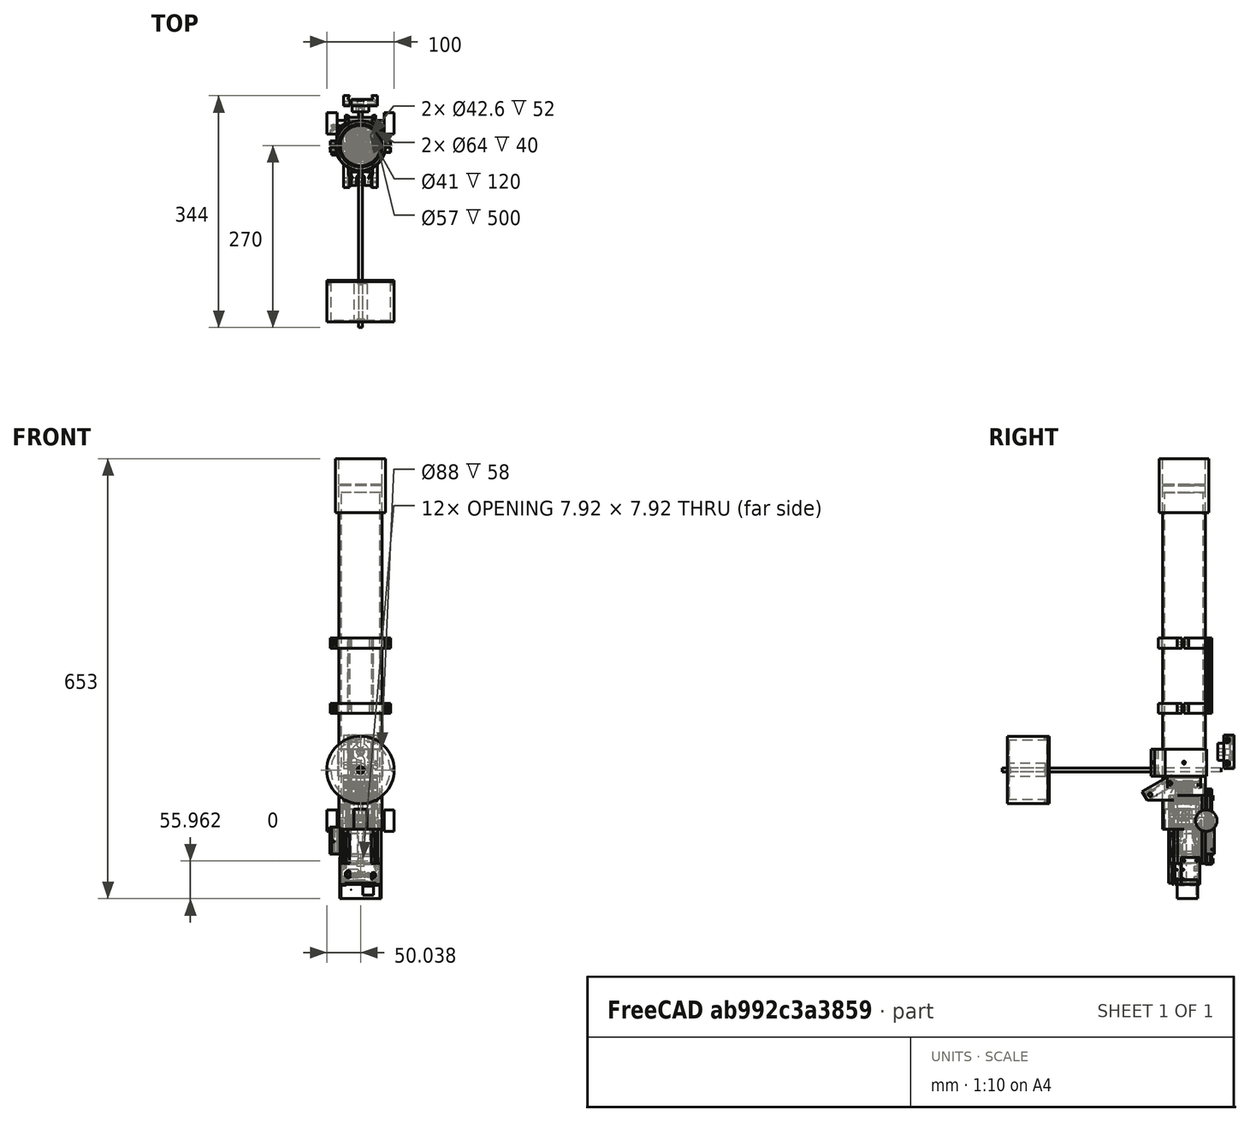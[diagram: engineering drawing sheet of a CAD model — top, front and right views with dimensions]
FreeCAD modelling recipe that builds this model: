
FCSTD DOCUMENT  (FreeCAD 0.17R13387 (Git))
Label: eq-mount-V1.5
License: All rights reserved
LicenseURL: http://en.wikipedia.org/wiki/All_rights_reserved
objects: Part::Cylinder×248, Part::MultiFuse×191, Part::Box×141, Part::Cut×137, Part::Feature×48, Part::Extrusion×34, Part::FeaturePython×21, Sketcher::SketchObject×16, Part::Part2DObjectPython×15, App::Part×13, Part::Chamfer×11, Part::Fillet×5, Part::RegularPolygon×3, Part::Wedge×1, Part::Cone×1
note: 872 computed .brp shape members not serialized (recipe doc carries the construction recipe); baked Part::Feature solids carry a one-line shape summary decoded from their .brp

FEATURE [Part::Box] Box010  label="Krychle009"
  AttacherType = Attacher::AttachEngine3D
  Height = 10
  Length = 43
  Placement = pos=(-21.5,-20.5,0) rot=(0,0,1;0rad)
  Width = 42
FEATURE [Part::Chamfer] Chamfer001
  Base = -> Box010
  Edges = 2 edges r=5: [Edge1,Edge5]
FEATURE [Part::Cylinder] Cylinder014005154  label="Válec151"
  Angle = 360
  AttacherType = Attacher::AttachEngine3D
  Height = 50
  Placement = pos=(-9.9,9.9,0) rot=(0,0,1;0rad)
  Radius = 1.6
FEATURE [Part::Cylinder] Cylinder014005155  label="Válec152"
  Angle = 360
  AttacherType = Attacher::AttachEngine3D
  Height = 50
  Placement = pos=(9.9,9.9,0) rot=(0,0,1;0rad)
  Radius = 1.6
FEATURE [Part::Cylinder] Cylinder014005156  label="dira stred001"
  Angle = 360
  AttacherType = Attacher::AttachEngine3D
  Height = 50
  Radius = 11
FEATURE [Part::Cylinder] Cylinder014005157  label="Válec153"
  Angle = 360
  AttacherType = Attacher::AttachEngine3D
  Height = 50
  Placement = pos=(-9.9,-9.9,0) rot=(0,0,1;0rad)
  Radius = 1.6
FEATURE [Part::Cylinder] Cylinder014005158  label="Válec154"
  Angle = 360
  AttacherType = Attacher::AttachEngine3D
  Height = 50
  Placement = pos=(9.9,-9.9,0) rot=(0,0,1;0rad)
  Radius = 1.6
FEATURE [Part::MultiFuse] Fusion092  label="diry001"
  Shapes = -> [Cylinder014005154,Cylinder014005155,Cylinder014005156,Cylinder014005157,Cylinder014005158]
FEATURE [Part::Cut] Cut061007  label="Horni ucjyt"
  Base = -> Chamfer001
  Placement = pos=(0,0,40.5) rot=(0,0,1;0rad)
  Tool = -> Fusion092
FEATURE [Part::Box] Box  label="deska"
  AttacherType = Attacher::AttachEngine3D
  Height = 102
  Length = 43
  Placement = pos=(-21.5,21.5,-51.5) rot=(0,0,1;0rad)
  Width = 10
FEATURE [Part::Box] Box012  label="deska001"
  AttacherType = Attacher::AttachEngine3D
  Height = 102
  Length = 9
  Placement = pos=(-30.5,-14.5,-51.5) rot=(0,0,1;0rad)
  Width = 46
FEATURE [Part::Box] Box013  label="deska002"
  AttacherType = Attacher::AttachEngine3D
  Height = 102
  Length = 9
  Placement = pos=(21.5,-14.5,-51.5) rot=(0,0,1;0rad)
  Width = 46
FEATURE [Part::Box] Box014  label="Krychle"
  AttacherType = Attacher::AttachEngine3D
  Height = 112
  Length = 38
  Placement = pos=(-19,32,-52) rot=(0,0,1;0rad)
  Width = 10
FEATURE [Part::Box] Box015  label="Krychle011"
  AttacherType = Attacher::AttachEngine3D
  Height = 112
  Length = 38
  Placement = pos=(-19,34,-52) rot=(0,0,1;0rad)
  Width = 6
FEATURE [Part::Cut] Cut061009
  Base = -> Box014
  Tool = -> Box015
FEATURE [Sketcher::SketchObject] Sketch
  MapMode = 5
  Placement = pos=(0,0,60) rot=(0,0,1;0rad)
  sketch-geometry (6):
    g0: LineSegment StartX=-18.9734 StartY=34.0308 StartZ=0 EndX=-16.0253 EndY=36.9748 EndZ=0
    g1: LineSegment StartX=18.996 StartY=34.0308 StartZ=0 EndX=16.044 EndY=36.9748 EndZ=0
    g2: LineSegment StartX=18.996 StartY=34.0308 StartZ=0 EndX=-18.9734 EndY=34.0308 EndZ=0
    g3: LineSegment StartX=-18.9734 StartY=40.0311 StartZ=0 EndX=-16.0253 EndY=36.9748 EndZ=0
    g4: LineSegment StartX=16.044 StartY=36.9748 StartZ=0 EndX=18.9109 EndY=40.0311 EndZ=0
    g5: LineSegment StartX=-18.9734 StartY=40.0311 StartZ=0 EndX=18.9109 EndY=40.0311 EndZ=0
  constraints (7):
    c: Coincident(g2,g1)
    c: Coincident(g2,g0)
    c: Horizontal(g2)
    c: Coincident(g3,g0)
    c: Coincident(g5,g3)
    c: Coincident(g5,g4)
    c: Horizontal(g5)
FEATURE [Part::Extrusion] Extrude009
  Base = -> Sketch
  Dir = (0,0,1)
  DirMode = 2
  FaceMakerClass = Part::FaceMakerBullseye
  LengthFwd = -112
  LengthRev = 0
  Solid = true
  Symmetric = false
FEATURE [Part::MultiFuse] Fusion095  label="Arca plate base"
  Placement = pos=(0,-0.5,0) rot=(0,0,1;0rad)
  Shapes = -> [Extrude009,Cut061009]
FEATURE [Part::Box] Box016  label="Krychle012"
  AttacherType = Attacher::AttachEngine3D
  Height = 112
  Length = 38
  Placement = pos=(-19,32,-52) rot=(0,0,1;0rad)
  Width = 10
FEATURE [Part::Box] Box017  label="Krychle013"
  AttacherType = Attacher::AttachEngine3D
  Height = 112
  Length = 38
  Placement = pos=(-19,34,-52) rot=(0,0,1;0rad)
  Width = 6
FEATURE [Part::Cut] Cut061010
  Base = -> Box016
  Tool = -> Box017
FEATURE [Sketcher::SketchObject] Sketch002
  MapMode = 5
  Placement = pos=(0,0,60) rot=(0,0,1;0rad)
  sketch-geometry (6):
    g0: LineSegment StartX=-18.9734 StartY=34.0308 StartZ=0 EndX=-16.0253 EndY=36.9748 EndZ=0
    g1: LineSegment StartX=18.996 StartY=34.0308 StartZ=0 EndX=16.044 EndY=36.9748 EndZ=0
    g2: LineSegment StartX=18.996 StartY=34.0308 StartZ=0 EndX=-18.9734 EndY=34.0308 EndZ=0
    g3: LineSegment StartX=-18.9734 StartY=40.0311 StartZ=0 EndX=-16.0253 EndY=36.9748 EndZ=0
    g4: LineSegment StartX=16.044 StartY=36.9748 StartZ=0 EndX=18.9109 EndY=40.0311 EndZ=0
    g5: LineSegment StartX=-18.9734 StartY=40.0311 StartZ=0 EndX=18.9109 EndY=40.0311 EndZ=0
  constraints (7):
    c: Coincident(g2,g1)
    c: Coincident(g2,g0)
    c: Horizontal(g2)
    c: Coincident(g3,g0)
    c: Coincident(g5,g3)
    c: Coincident(g5,g4)
    c: Horizontal(g5)
FEATURE [Part::Extrusion] Extrude010
  Base = -> Sketch002
  Dir = (0,0,1)
  DirMode = 2
  FaceMakerClass = Part::FaceMakerBullseye
  LengthFwd = -112
  LengthRev = 0
  Solid = true
  Symmetric = false
FEATURE [Part::MultiFuse] Fusion096  label="Arca plate base001"
  Placement = pos=(0,-0.6,0) rot=(0,0,1;0rad)
  Shapes = -> [Extrude010,Cut061010]
FEATURE [Part::Cylinder] Cylinder014005164  label="Válec159"
  Angle = 360
  AttacherType = Attacher::AttachEngine3D
  Height = 200
  Placement = pos=(0,27,-100) rot=(0,0,1;0rad)
  Radius = 3.2
FEATURE [Part::FeaturePython] Nut  label="M6-Nut"  # Fasteners workbench fastener (typed FeaturePython)
  Placement = pos=(0,27,46) rot=(0,0,1;0rad)
  diameter = 8
  invert = false
  matchOuter = false
  offset = 0
  thread = false
  type = 1
FEATURE [Part::FeaturePython] Nut001  label="M6-Nut001"  # Fasteners workbench fastener (typed FeaturePython)
  Placement = pos=(0,27,-52) rot=(0,0,1;0rad)
  diameter = 8
  invert = false
  matchOuter = false
  offset = 0
  thread = false
  type = 1
FEATURE [Part::MultiFuse] Fusion097  label="Dira zavazi"
  Shapes = -> [Cylinder014005164,Nut,Nut001]
FEATURE [Part::Cylinder] Cylinder014005165  label="Válec160"
  Angle = 360
  AttacherType = Attacher::AttachEngine3D
  Height = 10
  Placement = pos=(0,43,46.5) rot=(1,0,0;1.5708rad)
  Radius = 4
FEATURE [Part::Cylinder] Cylinder014005166  label="Válec161"
  Angle = 360
  AttacherType = Attacher::AttachEngine3D
  Height = 10
  Placement = pos=(0,43,-47) rot=(1,0,0;1.5708rad)
  Radius = 4
FEATURE [Part::RegularPolygon] RegularPolygon004  label="Pravidelný n-úhelník004"
  AttacherType = Attacher::AttachEngine3D
  Circumradius = 6
  Polygon = 6
FEATURE [Part::Extrusion] Extrude027
  Base = -> RegularPolygon004
  Dir = (0,0,1)
  DirMode = 2
  FaceMakerClass = Part::FaceMakerBullseye
  LengthFwd = 8
  LengthRev = 0
  Placement = pos=(0,0,13) rot=(0,0,1;0rad)
  Solid = true
  Symmetric = false
FEATURE [Part::FeaturePython] Nut007  label="M4-Nut002"  # Fasteners workbench fastener (typed FeaturePython)
  Placement = pos=(22,17,69) rot=(0,1,0;1.5708rad)
  diameter = 6
  invert = false
  matchOuter = false
  offset = 0
  thread = false
  type = 1
FEATURE [Part::FeaturePython] Nut008  label="M4-Nut003"  # Fasteners workbench fastener (typed FeaturePython)
  Placement = pos=(22,-17,69) rot=(0,1,0;1.5708rad)
  diameter = 6
  invert = false
  matchOuter = false
  offset = 0
  thread = false
  type = 1
FEATURE [Sketcher::SketchObject] Sketch009
  MapMode = 5
  Placement = pos=(0,0,60) rot=(0,0,1;0rad)
  sketch-geometry (6):
    g0: LineSegment StartX=-18.9734 StartY=34.0308 StartZ=0 EndX=-16.0253 EndY=36.9748 EndZ=0
    g1: LineSegment StartX=18.996 StartY=34.0308 StartZ=0 EndX=16.044 EndY=36.9748 EndZ=0
    g2: LineSegment StartX=18.996 StartY=34.0308 StartZ=0 EndX=-18.9734 EndY=34.0308 EndZ=0
    g3: LineSegment StartX=-18.9734 StartY=40.0311 StartZ=0 EndX=-16.0253 EndY=36.9748 EndZ=0
    g4: LineSegment StartX=16.044 StartY=36.9748 StartZ=0 EndX=18.9109 EndY=40.0311 EndZ=0
    g5: LineSegment StartX=-18.9734 StartY=40.0311 StartZ=0 EndX=18.9109 EndY=40.0311 EndZ=0
  constraints (7):
    c: Coincident(g2,g1)
    c: Coincident(g2,g0)
    c: Horizontal(g2)
    c: Coincident(g3,g0)
    c: Coincident(g5,g3)
    c: Coincident(g5,g4)
    c: Horizontal(g5)
FEATURE [Part::Extrusion] Extrude025
  Base = -> Sketch009
  Dir = (0,0,1)
  DirMode = 2
  FaceMakerClass = Part::FaceMakerBullseye
  LengthFwd = -112
  LengthRev = 0
  Solid = true
  Symmetric = false
FEATURE [Sketcher::SketchObject] Sketch010
  MapMode = 45
  Placement = pos=(44.88,21.011,5.40003) rot=(0.707106,0.001666,0.707106;3.13826rad)
  sketch-geometry (7):
    g0: LineSegment StartX=5.21891 StartY=0.0364138 StartZ=0 EndX=2.62121 EndY=4.46293 EndZ=0
    g1: LineSegment StartX=2.62121 StartY=4.46293 StartZ=0 EndX=-2.51111 EndY=4.42651 EndZ=0
    g2: LineSegment StartX=-2.51111 StartY=4.42651 StartZ=0 EndX=-5.04574 EndY=-0.0364138 EndZ=0
    g3: LineSegment StartX=-5.04574 StartY=-0.0364138 StartZ=0 EndX=-2.44804 EndY=-4.46293 EndZ=0
    g4: LineSegment StartX=-2.44804 StartY=-4.46293 StartZ=0 EndX=2.68428 EndY=-4.42651 EndZ=0
    g5: LineSegment StartX=2.68428 StartY=-4.42651 StartZ=0 EndX=5.21891 EndY=0.0364138 EndZ=0
    g6: Circle [constr] CenterX=0.0865834 CenterY=0 CenterZ=0 NormalX=0 NormalY=0 NormalZ=1 AngleXU=0 Radius=5.13245
  constraints (14):
    c: Coincident(g0,g1)
    c: Coincident(g1,g2)
    c: Coincident(g2,g3)
    c: Coincident(g3,g4)
    c: Coincident(g4,g5)
    c: Coincident(g5,g0)
    c: Equal(g0, g1-g5) x5
    c: PointOnObject(g0,g6)
    c: PointOnObject(g1,g6)
    c: PointOnObject(g2,g6)
    c: PointOnObject(g3,g6)
    c: PointOnObject(g4,g6)
    c: PointOnObject(g5,g6)
    c: PointOnObject(g6,g-1)
FEATURE [Part::Extrusion] Extrude026
  Base = -> Sketch010
  Dir = (1,0,0)
  DirMode = 2
  FaceMakerClass = Part::FaceMakerBullseye
  LengthFwd = 5
  LengthRev = 0
  Placement = pos=(0,0,0.25) rot=(0,0,1;0rad)
  Solid = true
  Symmetric = false
FEATURE [Part::Feature] Screw_solid087  label="M2x4-Screw (Solid)087"
  Placement = pos=(0,0,0) rot=(0,0,1;3.14159rad)
  shape: bbox 3.6 x 3.6 x 4 mm, 12 faces (baked)
FEATURE [Part::Feature] Cylinder014005326  label="Válec302"
  Placement = pos=(0,0,0) rot=(0,0,1;2.0944rad)
  shape: bbox 5 x 5 x 7 mm, 3 faces (baked)
FEATURE [Part::Feature] Cylinder014005327  label="Válec303"
  Placement = pos=(0,0,0) rot=(0,0,1;4.18879rad)
  shape: bbox 5 x 5 x 7 mm, 3 faces (baked)
FEATURE [Part::Feature] Screw_solid088  label="M2x4-Screw (Solid)088"
  Placement = pos=(0,0,0) rot=(0,0,1;1.0472rad)
  shape: bbox 3.6 x 3.6 x 4 mm, 12 faces (baked)
FEATURE [Part::Feature] Cylinder014005328  label="Válec304"
  shape: bbox 5 x 5 x 7 mm, 3 faces (baked)
FEATURE [Part::MultiFuse] Fusion196
  Shapes = -> [Cylinder014005327,Cylinder014005328,Cylinder014005326]
FEATURE [Part::Feature] Screw_solid089  label="M2x4-Screw (Solid)089"
  Placement = pos=(0,0,0) rot=(0,0,-1;1.0472rad)
  shape: bbox 3.6 x 3.6 x 4 mm, 12 faces (baked)
FEATURE [Part::MultiFuse] Fusion199  label="srouby030"
  Placement = pos=(0,0,0.5) rot=(0,0,1;0rad)
  Shapes = -> [Screw_solid088,Screw_solid089,Screw_solid087]
FEATURE [Part::Box] Box035  label="Krychle028"
  AttacherType = Attacher::AttachEngine3D
  Height = 112
  Length = 38
  Placement = pos=(-19,32,-52) rot=(0,0,1;0rad)
  Width = 10
FEATURE [Part::Box] Box036  label="Krychle029"
  AttacherType = Attacher::AttachEngine3D
  Height = 112
  Length = 38
  Placement = pos=(-19,34,-52) rot=(0,0,1;0rad)
  Width = 6
FEATURE [Part::Cylinder] Cylinder014005329  label="Válec305"
  Angle = 360
  AttacherType = Attacher::AttachEngine3D
  Height = 22
  Radius = 2.6
FEATURE [Part::MultiFuse] Fusion195
  Shapes = -> [Cylinder014005329,Extrude026]
FEATURE [Part::Cylinder] Cylinder014005330  label="Válec306"
  Angle = 360
  AttacherType = Attacher::AttachEngine3D
  Height = 7
  Radius = 2.6
FEATURE [Part::MultiFuse] Fusion198
  Placement = pos=(0,0,1) rot=(0,0,1;0rad)
  Shapes = -> [Fusion196,Cylinder014005330]
FEATURE [Part::Cylinder] Cylinder014005331  label="Válec307"
  Angle = 360
  AttacherType = Attacher::AttachEngine3D
  Height = 8
  Placement = pos=(0,0,66) rot=(0,0,1;0rad)
  Radius = 4.5
FEATURE [Part::Box] Box037  label="Krychle030"
  AttacherType = Attacher::AttachEngine3D
  Height = 15
  Length = 50
  Placement = pos=(-25,-25,64) rot=(0,0,1;0rad)
  Width = 50
FEATURE [Part::Cylinder] Cylinder014005332  label="Válec308"
  Angle = 360
  AttacherType = Attacher::AttachEngine3D
  Height = 6
  Placement = pos=(0,0,7) rot=(0,0,1;0rad)
  Radius = 6.5
FEATURE [Part::Box] Box038  label="Krychle031"
  AttacherType = Attacher::AttachEngine3D
  Height = 15
  Length = 2
  Placement = pos=(-15.5,-26,61) rot=(0,0,1;0rad)
  Width = 52
FEATURE [Part::Cylinder] Cylinder014005333  label="Unasec vrch017"
  Angle = 360
  AttacherType = Attacher::AttachEngine3D
  Height = 1.5
  Placement = pos=(0,0,5.5) rot=(0,0,1;0rad)
  Radius = 15.5
FEATURE [Part::Cylinder] Cylinder014005334  label="Válec309"
  Angle = 360
  AttacherType = Attacher::AttachEngine3D
  Height = 55
  Placement = pos=(0,0,35) rot=(0,0,1;0rad)
  Radius = 2.7
FEATURE [Part::Cylinder] Cylinder014005335  label="Válec310"
  Angle = 360
  AttacherType = Attacher::AttachEngine3D
  Height = 9
  Placement = pos=(0,0,55) rot=(0,0,1;0rad)
  Radius = 12.5
FEATURE [Part::Cut] Cut061079  label="unasec vrch017"
  Base = -> Cylinder014005333
  Tool = -> Fusion199
FEATURE [Part::Cut] Cut061080
  Base = -> Box035
  Tool = -> Box036
FEATURE [Part::MultiFuse] Fusion194  label="Arca plate base004"
  Placement = pos=(0,-6.5,115.5) rot=(-1,0,0;1.5708rad)
  Shapes = -> [Extrude025,Cut061080]
FEATURE [Part::Cut] Cut061077  label="Arca sw 002"
  Base = -> Box037
  Tool = -> Fusion194
FEATURE [Part::Cut] Cut061083
  Base = -> Cut061077
  Tool = -> Box038
FEATURE [Part::MultiFuse] Fusion192
  Shapes = -> [Cylinder014005335,Cut061083]
FEATURE [Part::Cut] Cut061084  label="Unasec Vrch zaklad017"
  Base = -> Cut061079
  Tool = -> Fusion198
FEATURE [Part::MultiFuse] Fusion197
  Shapes = -> [Cut061084,Cylinder014005332,Extrude027]
FEATURE [Part::Cut] Cut061081  label="unasec top004"
  Base = -> Fusion197
  Placement = pos=(0,0,42) rot=(0,0,1;0rad)
  Tool = -> Fusion195
FEATURE [Part::MultiFuse] Fusion191
  Shapes = -> [Cylinder014005334,Cut061081,Cylinder014005331]
FEATURE [Part::Cut] Cut061082
  Base = -> Fusion192
  Tool = -> Fusion191
FEATURE [Part::Cylinder] Cylinder014005336  label="Válec311"
  Angle = 360
  AttacherType = Attacher::AttachEngine3D
  Height = 60
  Placement = pos=(-30,17,69) rot=(0,1,0;1.5708rad)
  Radius = 2.1
FEATURE [Part::Cylinder] Cylinder014005337  label="Válec312"
  Angle = 360
  AttacherType = Attacher::AttachEngine3D
  Height = 60
  Placement = pos=(-30,-17,69) rot=(0,1,0;1.5708rad)
  Radius = 2.1
FEATURE [Part::MultiFuse] Fusion193
  Shapes = -> [Cylinder014005336,Cylinder014005337,Nut007,Nut008]
FEATURE [Part::Cut] Cut061078
  Base = -> Cut061082
  Tool = -> Fusion193
FEATURE [Part::Cylinder] Cylinder014005338  label="Válec313"
  Angle = 360
  AttacherType = Attacher::AttachEngine3D
  Height = 2.5
  Placement = pos=(0,-12,71) rot=(0,0,1;0rad)
  Radius = 6
FEATURE [Part::Box] Box039  label="Krychle032"
  AttacherType = Attacher::AttachEngine3D
  Height = 2.5
  Length = 12
  Placement = pos=(-6,-25,71) rot=(0,0,1;0rad)
  Width = 13
FEATURE [Part::MultiFuse] Fusion201
  Placement = pos=(0,0,1) rot=(0,0,1;3.14159rad)
  Shapes = -> [Box039,Cylinder014005338]
FEATURE [Part::Cylinder] Cylinder014005339  label="Válec314"
  Angle = 360
  AttacherType = Attacher::AttachEngine3D
  Height = 2.5
  Placement = pos=(0,-12,71) rot=(0,0,1;0rad)
  Radius = 6
FEATURE [Part::Box] Box040  label="Krychle033"
  AttacherType = Attacher::AttachEngine3D
  Height = 2.5
  Length = 12
  Placement = pos=(-6,-25,71) rot=(0,0,1;0rad)
  Width = 13
FEATURE [Part::MultiFuse] Fusion200
  Placement = pos=(0,0,1) rot=(0,0,1;0rad)
  Shapes = -> [Box040,Cylinder014005339]
FEATURE [Part::MultiFuse] Fusion202
  Shapes = -> [Fusion200,Fusion201]
FEATURE [Part::Cut] Cut061085  label="Swis Arca002"
  Base = -> Cut061078
  Placement = pos=(0,-5,115) rot=(-1,0,0;1.5708rad)
  Tool = -> Fusion202
FEATURE [Part::Box] Box041  label="Krychle034"
  AttacherType = Attacher::AttachEngine3D
  Height = 13
  Length = 80
  Placement = pos=(-40,-34,50.5) rot=(0,0,1;0rad)
  Width = 80
FEATURE [Part::Box] Box042  label="Krychle035"
  AttacherType = Attacher::AttachEngine3D
  Height = 2
  Length = 80
  Placement = pos=(-40,-36,-53) rot=(0,0,1;0rad)
  Width = 80
FEATURE [Part::MultiFuse] Fusion203  label="Oreze"
  Shapes = -> [Box041,Box042]
FEATURE [Part::Feature] Cut001001  label="polar finder"
  Placement = pos=(-9.5,-26.5,-25) rot=(0,0,-1;1.5708rad)
  shape: bbox 15 x 36 x 40 mm, 20 faces (baked)
FEATURE [Part::Cylinder] Cylinder014005345  label="M6 Rail"
  Angle = 360
  AttacherType = Attacher::AttachEngine3D
  Height = 325
  Placement = pos=(0,55,88) rot=(1,0,0;1.5708rad)
  Radius = 3
FEATURE [Part::Cylinder] Cylinder014005346  label="Válec317"
  Angle = 360
  AttacherType = Attacher::AttachEngine3D
  Height = 60
  Placement = pos=(0,-200,88) rot=(1,0,0;1.5708rad)
  Radius = 50
FEATURE [Part::Cylinder] Cylinder014005347  label="Válec318"
  Angle = 360
  AttacherType = Attacher::AttachEngine3D
  Height = 58
  Placement = pos=(0,-200,88) rot=(1,0,0;1.5708rad)
  Radius = 44
FEATURE [Part::Cut] Cut061093
  Base = -> Cylinder014005346
  Tool = -> Cylinder014005347
FEATURE [Part::Cylinder] Cylinder014005348  label="Válec319"
  Angle = 360
  AttacherType = Attacher::AttachEngine3D
  Height = 56
  Placement = pos=(0,-203.5,88) rot=(1,0,0;1.5708rad)
  Radius = 10
FEATURE [Part::MultiFuse] Fusion217  label="Zavazí dno"
  Placement = pos=(0,-2,0) rot=(0,0,1;0rad)
  Shapes = -> [Cut061093,Cylinder014005348]
FEATURE [Part::Cylinder] Cylinder014005349  label="Válec320"
  Angle = 360
  AttacherType = Attacher::AttachEngine3D
  Height = 2
  Placement = pos=(0,-200,88) rot=(1,0,0;1.5708rad)
  Radius = 50
FEATURE [Part::Cylinder] Cylinder014005350  label="Válec321"
  Angle = 360
  AttacherType = Attacher::AttachEngine3D
  Height = 3.5
  Placement = pos=(0,-200,88) rot=(1,0,0;1.5708rad)
  Radius = 44
FEATURE [Part::MultiFuse] Fusion218  label="zaazi vyko"
  Shapes = -> [Cylinder014005350,Cylinder014005349]
FEATURE [Part::Cylinder] Cylinder014005351  label="tyč závaží001"
  Angle = 360
  AttacherType = Attacher::AttachEngine3D
  Height = 350
  Placement = pos=(0,85,88) rot=(1,0,0;1.5708rad)
  Radius = 3
FEATURE [Part::FeaturePython] Nut013  label="M6-Nut006"  # Fasteners workbench fastener (typed FeaturePython)
  Placement = pos=(0,-258,88) rot=(1,0,0;1.5708rad)
  diameter = 8
  invert = false
  matchOuter = false
  offset = 0
  thread = false
  type = 1
FEATURE [Part::Feature] Screw006_solid  label="vyko M2.5x8"
  Placement = pos=(0,0,10) rot=(0,0,1;0rad)
  shape: bbox 4.5 x 8.524 x 4.5 mm, 11 faces (baked)
FEATURE [Part::Feature] Screw006_solid001  label="vyko M2.5x009"
  Placement = pos=(0,0,104) rot=(0,0,1;0rad)
  shape: bbox 4.5 x 8.524 x 4.5 mm, 11 faces (baked)
FEATURE [Part::Feature] Screw006_solid002  label="vyko M2.5x010"
  Placement = pos=(47,0,57) rot=(0,0,1;0rad)
  shape: bbox 4.5 x 8.524 x 4.5 mm, 11 faces (baked)
FEATURE [Part::Feature] Screw006_solid003  label="vyko M2.5x011"
  Placement = pos=(-47,0,57) rot=(0,0,1;0rad)
  shape: bbox 4.5 x 8.524 x 4.5 mm, 11 faces (baked)
FEATURE [Part::MultiFuse] Fusion219  label="srouby diry zavazi"
  Shapes = -> [Cylinder014005351,Screw006_solid,Screw006_solid001,Screw006_solid002,Screw006_solid003,Nut013]
FEATURE [Part::Cut] Cut061094  label="Weight  bottom"
  Base = -> Fusion217
  Tool = -> Fusion219
FEATURE [Part::FeaturePython] Nut014  label="M6-Nut005"  # Fasteners workbench fastener (typed FeaturePython)
  Placement = pos=(0,-238,88) rot=(1,0,0;1.5708rad)
  diameter = 8
  invert = false
  matchOuter = false
  offset = 0
  thread = false
  type = 1
FEATURE [Part::Cylinder] Cylinder014005352  label="tyč závaží002"
  Angle = 360
  AttacherType = Attacher::AttachEngine3D
  Height = 300
  Placement = pos=(0,55,88) rot=(1,0,0;1.5708rad)
  Radius = 3
FEATURE [Part::Feature] Screw006_solid004  label="vyko M2.5x012"
  Placement = pos=(0,0,104) rot=(0,0,1;0rad)
  shape: bbox 4.5 x 8.524 x 4.5 mm, 11 faces (baked)
FEATURE [Part::Feature] Screw006_solid005  label="vyko M2.5x013"
  Placement = pos=(47,0,57) rot=(0,0,1;0rad)
  shape: bbox 4.5 x 8.524 x 4.5 mm, 11 faces (baked)
FEATURE [Part::Feature] Screw006_solid006  label="vyko M2.5x014"
  Placement = pos=(-47,0,57) rot=(0,0,1;0rad)
  shape: bbox 4.5 x 8.524 x 4.5 mm, 11 faces (baked)
FEATURE [Part::Feature] Screw006_solid007  label="vyko M2.5x015"
  Placement = pos=(0,0,10) rot=(0,0,1;0rad)
  shape: bbox 4.5 x 8.524 x 4.5 mm, 11 faces (baked)
FEATURE [Part::MultiFuse] Fusion220  label="srouby diry zavazi001"
  Shapes = -> [Cylinder014005352,Screw006_solid007,Screw006_solid004,Screw006_solid005,Screw006_solid006,Nut014]
FEATURE [Part::Cut] Cut061095  label="Weight top"
  Base = -> Fusion218
  Tool = -> Fusion220
FEATURE [App::Part] Part019  label="Temp"
  Group = -> [Cut061009,Sketch,Box014,Box015,Extrude009,Fusion095,Sketch009,Fusion193,Fusion192,Fusion191,Fusion194,Fusion196,Fusion195,Fusion197,Fusion198,Nut007,Nut008,Extrude025,RegularPolygon004,Extrude026,Extrude027,Cut061078,Cut061080,Cut061082,Cut061083,Cut061081,Cut061084,Cut061079,Cut061077,Screw_solid088,Screw_solid087,Cylinder014005326,Cylinder014005328,Screw_solid089,Cylinder014005327,Sketch010,+22 more]
  License = CC BY 3.0
  LicenseURL = http://creativecommons.org/licenses/by/3.0/
  Origin = -> Origin019
FEATURE [Part::Feature] Cut061098  label="Motor PG100"
  Placement = pos=(0,0,2) rot=(0,0,1;0rad)
  shape: bbox 42.3 x 42.3 x 110 mm, 26 faces (baked)
FEATURE [Part::Cylinder] Cylinder014005356  label="Válec322"
  Angle = 360
  AttacherType = Attacher::AttachEngine3D
  Height = 3
  Placement = pos=(-9.9,9.9,47) rot=(0,0,1;0rad)
  Radius = 2.8
FEATURE [Part::Cylinder] Cylinder014005357  label="Válec323"
  Angle = 360
  AttacherType = Attacher::AttachEngine3D
  Height = 3
  Placement = pos=(9.9,9.9,47) rot=(0,0,1;0rad)
  Radius = 2.8
FEATURE [Part::Cylinder] Cylinder014005358  label="Válec324"
  Angle = 360
  AttacherType = Attacher::AttachEngine3D
  Height = 3
  Placement = pos=(-9.9,-9.9,47) rot=(0,0,1;0rad)
  Radius = 2.8
FEATURE [Part::Cylinder] Cylinder014005359  label="Válec325"
  Angle = 360
  AttacherType = Attacher::AttachEngine3D
  Height = 3
  Placement = pos=(9.9,-9.9,47) rot=(0,0,1;0rad)
  Radius = 2.8
FEATURE [Part::MultiFuse] Fusion221  label="Imbus diry"
  Shapes = -> [Cylinder014005356,Cylinder014005357,Cylinder014005358,Cylinder014005359]
FEATURE [Part::MultiFuse] Fusion222
  Shapes = -> [Cut061007,Cylinder014005165,Cylinder014005166,Box013,Box,Box012,Fusion096]
FEATURE [Part::MultiFuse] Fusion223
  Shapes = -> [Fusion221,Fusion203,Fusion097]
FEATURE [Part::Cut] Cut061099
  Base = -> Fusion222
  Tool = -> Fusion223
FEATURE [Part::Chamfer] Chamfer008  label="Zaklad"
  Base = -> Cut061099
  Edges = 4 edges r=5: [Edge130,Edge132,Edge145,Edge147]
FEATURE [App::Part] Part022  label="Zaklad002"
  Group = -> [Nut,Nut001,Fusion097,Fusion092,Fusion096,Cut061007,Cut061010,Chamfer001,Cylinder014005156,Box010,Cylinder014005157,Cylinder014005154,Cylinder014005158,Cylinder014005155,Box017,Box,Box016,Box012,Box013,Sketch002,Extrude010,Cylinder014005166,Cylinder014005164,Cylinder014005165,Fusion203,Box042,Box041,Cylinder014005359,Cylinder014005358,Cylinder014005356,Cylinder014005357,Cut061099,Fusion221,+4 more]
  License = CC BY 3.0
  LicenseURL = http://creativecommons.org/licenses/by/3.0/
  Origin = -> Origin022
FEATURE [Part::Box] Box008  label="Krychle043"
  AttacherType = Attacher::AttachEngine3D
  Height = 28
  Length = 62
  Placement = pos=(-2.5,-2,-5) rot=(0,0,1;0rad)
  Width = 31
FEATURE [Part::Box] Box054  label="Krychle003"
  AttacherType = Attacher::AttachEngine3D
  Height = 26
  Length = 58
  Placement = pos=(-0.5,0,-3) rot=(0,0,1;0rad)
  Width = 29
FEATURE [Part::Cylinder] Cylinder014005360  label="Válec326"
  Angle = 360
  AttacherType = Attacher::AttachEngine3D
  Height = 8
  Placement = pos=(53.5,21.25,0) rot=(0,0,1;0rad)
  Radius = 0.75
FEATURE [Part::Cylinder] Cylinder014005361  label="Válec010"
  Angle = 360
  AttacherType = Attacher::AttachEngine3D
  Height = 8
  Placement = pos=(53.5,6,0) rot=(0,0,1;0rad)
  Radius = 0.75
FEATURE [Part::Cylinder] Cylinder012  label="Válec327"
  Angle = 360
  AttacherType = Attacher::AttachEngine3D
  Height = 8
  Placement = pos=(3.5,21.25,0) rot=(0,0,1;0rad)
  Radius = 0.75
FEATURE [Part::Cylinder] Cylinder014005362  label="Válec012"
  Angle = 360
  AttacherType = Attacher::AttachEngine3D
  Height = 8
  Placement = pos=(3.5,6,0) rot=(0,0,1;0rad)
  Radius = 0.7
FEATURE [Part::Part2DObjectPython] ShapeString001  # Draft 2D object (typed FeaturePython)
  FontFile = <path>
  Placement = pos=(15.3452,-2,30.5072) rot=(1,0,0;1.5708rad)
  Size = 4
  String = RA
  Tracking = 0
FEATURE [Part::Extrusion] Extrude031  label="Text RA"
  Base = -> ShapeString001
  Dir = (0,-1,0)
  DirMode = 2
  FaceMakerClass = Part::FaceMakerBullseye
  LengthFwd = 1
  LengthRev = 0
  Placement = pos=(21,0.5,-33) rot=(0,0,1;0rad)
  Solid = false
  Symmetric = false
FEATURE [Part::Part2DObjectPython] ShapeString  # Draft 2D object (typed FeaturePython)
  FontFile = <path>
  Placement = pos=(15.3452,-2,30.5072) rot=(1,0,0;1.5708rad)
  Size = 4
  String = ON
  Tracking = 0
FEATURE [Part::Extrusion] Extrude030  label="Text TR"
  Base = -> ShapeString
  Dir = (0,-1,0)
  DirMode = 2
  FaceMakerClass = Part::FaceMakerBullseye
  LengthFwd = 1
  LengthRev = 0
  Placement = pos=(-6.75,0.5,-33) rot=(0,0,1;0rad)
  Solid = false
  Symmetric = false
FEATURE [Part::Cut] Cut061101  label="Základ"
  Base = -> Box008
  Tool = -> Box054
FEATURE [Part::Cylinder] Cylinder017  label="Válec016"
  Angle = 360
  AttacherType = Attacher::AttachEngine3D
  Height = 6.5
  Placement = pos=(3.5,6,0) rot=(0,0,1;0rad)
  Radius = 3.5
FEATURE [Part::Cylinder] Cylinder014  label="Válec333"
  Angle = 360
  AttacherType = Attacher::AttachEngine3D
  Height = 6.5
  Placement = pos=(53.5,6,0) rot=(0,0,1;0rad)
  Radius = 3.5
FEATURE [Part::Cylinder] Cylinder016  label="Válec015"
  Angle = 360
  AttacherType = Attacher::AttachEngine3D
  Height = 6.5
  Placement = pos=(3.5,21.25,0) rot=(0,0,1;0rad)
  Radius = 3.5
FEATURE [Part::Cylinder] Cylinder015  label="Válec334"
  Angle = 360
  AttacherType = Attacher::AttachEngine3D
  Height = 6.5
  Placement = pos=(53.5,21.25,0) rot=(0,0,1;0rad)
  Radius = 3.5
FEATURE [Part::Cylinder] Cylinder021  label="Válec020"
  Angle = 360
  AttacherType = Attacher::AttachEngine3D
  Height = 70
  Placement = pos=(-5,20,16.5) rot=(0,1,0;1.5708rad)
  Radius = 1
FEATURE [Part::Cylinder] Cylinder020  label="Válec019"
  Angle = 360
  AttacherType = Attacher::AttachEngine3D
  Height = 70
  Placement = pos=(-5,6,16.5) rot=(0,1,0;1.5708rad)
  Radius = 1
FEATURE [Part::Box] Box055  label="RJ051"
  AttacherType = Attacher::AttachEngine3D
  Height = 13
  Length = 16
  Placement = pos=(32,-5,4.5) rot=(0,0,1;0rad)
  Width = 18.5
FEATURE [Part::Cylinder] Cylinder038  label="Válec337"
  Angle = 360
  AttacherType = Attacher::AttachEngine3D
  Height = 5
  Placement = pos=(14.25,1,9.5) rot=(1,0,0;1.5708rad)
  Radius = 1.5
FEATURE [Part::MultiFuse] Fusion226  label="Horni diry"
  Placement = pos=(0,0,3) rot=(0,0,1;0rad)
  Shapes = -> [Cylinder021,Cylinder020]
FEATURE [Part::MultiFuse] Fusion228  label="RJ a LED"
  Shapes = -> [Box055,Cylinder038]
FEATURE [Part::MultiFuse] Fusion230  label="diry008"
  Placement = pos=(0,0,-4) rot=(0,0,1;0rad)
  Shapes = -> [Cylinder012,Cylinder014005362,Cylinder014005360,Cylinder014005361]
FEATURE [Part::MultiFuse] Fusion007  label="sloupky"
  Placement = pos=(0,0,-3.5) rot=(0,0,1;0rad)
  Shapes = -> [Cylinder016,Cylinder017,Cylinder015,Cylinder014]
FEATURE [Part::MultiFuse] Fusion243  label="bez der"
  Shapes = -> [Cut061101,Fusion007]
FEATURE [Part::MultiFuse] Fusion244
  Shapes = -> [Fusion230,Fusion228,Fusion226]
FEATURE [Part::Cut] Cut061109
  Base = -> Fusion243
  Tool = -> Fusion244
FEATURE [Part::MultiFuse] Fusion245
  Shapes = -> [Extrude030,Extrude031]
FEATURE [Part::Cut] Cut061110
  Base = -> Cut061109
  Placement = pos=(-28.5,18.5,-80) rot=(1,0,0;1.5708rad)
  Tool = -> Fusion245
FEATURE [Part::Feature] Cut061098001  label="RA Motor PG100"
  shape: bbox 42.3 x 42.3 x 110 mm, 26 faces (baked)
FEATURE [Part::Box] Box068  label="Krychle054"
  AttacherType = Attacher::AttachEngine3D
  Height = 13
  Length = 2
  Placement = pos=(29,-4.5,-55) rot=(0,0,1;0rad)
  Width = 28
FEATURE [Part::Box] Box069  label="Krychle055"
  AttacherType = Attacher::AttachEngine3D
  Height = 13
  Length = 2
  Placement = pos=(-31,-4.5,-55) rot=(0,0,1;0rad)
  Width = 28
FEATURE [Part::MultiFuse] Fusion250
  Shapes = -> [Box068,Box069]
FEATURE [Part::MultiFuse] Fusion252  label="RA pcb box"
  Shapes = -> [Cut061110,Fusion250]
FEATURE [Part::Cylinder] Cylinder014005370  label="Válec352"
  Angle = 360
  AttacherType = Attacher::AttachEngine3D
  Height = 74
  Placement = pos=(-40,0,-46.5) rot=(0,1,0;1.5708rad)
  Radius = 1.4
FEATURE [Part::Cylinder] Cylinder014005371  label="Válec353"
  Angle = 360
  AttacherType = Attacher::AttachEngine3D
  Height = 74
  Placement = pos=(-40,19,-46.5) rot=(0,1,0;1.5708rad)
  Radius = 1.4
FEATURE [Part::MultiFuse] Fusion253
  Shapes = -> [Cylinder014005370,Cylinder014005371]
FEATURE [Part::Cylinder] Cylinder014005376  label="Válec358"
  Angle = 360
  AttacherType = Attacher::AttachEngine3D
  Height = 20
  Placement = pos=(-40,16,-17.5) rot=(0,1,0;1.5708rad)
  Radius = 1.4
FEATURE [Part::Cylinder] Cylinder014005377  label="Válec359"
  Angle = 360
  AttacherType = Attacher::AttachEngine3D
  Height = 20
  Placement = pos=(-40,1,-17.5) rot=(0,1,0;1.5708rad)
  Radius = 1.4
FEATURE [Part::Cut] Cut061098005  label="RA PCB Box"
  Base = -> Fusion252
  Tool = -> Fusion253
FEATURE [Part::Box] Box077  label="Krychle062"
  AttacherType = Attacher::AttachEngine3D
  Height = 13
  Length = 2
  Placement = pos=(29,-4.5,-55) rot=(0,0,1;0rad)
  Width = 28
FEATURE [Part::Cylinder] Cylinder014005393  label="Válec375"
  Angle = 360
  AttacherType = Attacher::AttachEngine3D
  Height = 74
  Placement = pos=(-40,19,-46.5) rot=(0,1,0;1.5708rad)
  Radius = 1.4
FEATURE [Part::Cylinder] Cylinder014005394  label="Válec376"
  Angle = 360
  AttacherType = Attacher::AttachEngine3D
  Height = 74
  Placement = pos=(-40,0,-46.5) rot=(0,1,0;1.5708rad)
  Radius = 1.4
FEATURE [Part::Box] Box078  label="Krychle063"
  AttacherType = Attacher::AttachEngine3D
  Height = 13
  Length = 2
  Placement = pos=(-31,-4.5,-55) rot=(0,0,1;0rad)
  Width = 28
FEATURE [Part::MultiFuse] Fusion266
  Shapes = -> [Box077,Box078]
FEATURE [Part::Part2DObjectPython] ShapeString008  # Draft 2D object (typed FeaturePython)
  FontFile = <path>
  Placement = pos=(15.3452,-2,30.5072) rot=(1,0,0;1.5708rad)
  Size = 4
  String = Focuser
  Tracking = 0
FEATURE [Part::Part2DObjectPython] ShapeString009  # Draft 2D object (typed FeaturePython)
  FontFile = <path>
  Placement = pos=(15.3452,-2,30.5072) rot=(1,0,0;1.5708rad)
  Size = 4
  String = DEC
  Tracking = 0
FEATURE [Part::Box] Box079  label="RJ053"
  AttacherType = Attacher::AttachEngine3D
  Height = 13
  Length = 16
  Placement = pos=(34,-4,4.5) rot=(0,0,1;0rad)
  Width = 18.5
FEATURE [Part::Cylinder] Cylinder014005398  label="Válec380"
  Angle = 360
  AttacherType = Attacher::AttachEngine3D
  Height = 8
  Placement = pos=(3.6,21.25,0) rot=(0,0,1;0rad)
  Radius = 0.75
FEATURE [Part::Cylinder] Cylinder014005399  label="Válec381"
  Angle = 360
  AttacherType = Attacher::AttachEngine3D
  Height = 6.5
  Placement = pos=(53.5,21.25,0) rot=(0,0,1;0rad)
  Radius = 3.5
FEATURE [Part::Cylinder] Cylinder014005400  label="Válec382"
  Angle = 360
  AttacherType = Attacher::AttachEngine3D
  Height = 70
  Placement = pos=(-5,6,16.5) rot=(0,1,0;1.5708rad)
  Radius = 1
FEATURE [Part::Cylinder] Cylinder014005401  label="Válec383"
  Angle = 360
  AttacherType = Attacher::AttachEngine3D
  Height = 6.5
  Placement = pos=(3.5,6,0) rot=(0,0,1;0rad)
  Radius = 3.5
FEATURE [Part::Cylinder] Cylinder014005402  label="Válec384"
  Angle = 360
  AttacherType = Attacher::AttachEngine3D
  Height = 70
  Placement = pos=(-5,20,16.5) rot=(0,1,0;1.5708rad)
  Radius = 1
FEATURE [Part::Cylinder] Cylinder014005403  label="Válec385"
  Angle = 360
  AttacherType = Attacher::AttachEngine3D
  Height = 8
  Placement = pos=(53.5,6,0) rot=(0,0,1;0rad)
  Radius = 0.75
FEATURE [Part::Box] Box082  label="Krychle066"
  AttacherType = Attacher::AttachEngine3D
  Height = 26
  Length = 58
  Placement = pos=(-0.5,0,-3) rot=(0,0,1;0rad)
  Width = 29
FEATURE [Part::Cylinder] Cylinder014005404  label="Válec386"
  Angle = 360
  AttacherType = Attacher::AttachEngine3D
  Height = 6.5
  Placement = pos=(53.5,6,0) rot=(0,0,1;0rad)
  Radius = 3.5
FEATURE [Part::Cylinder] Cylinder014005405  label="Válec387"
  Angle = 360
  AttacherType = Attacher::AttachEngine3D
  Height = 8
  Placement = pos=(53.5,21.25,0) rot=(0,0,1;0rad)
  Radius = 0.75
FEATURE [Part::Cylinder] Cylinder014005406  label="Válec388"
  Angle = 360
  AttacherType = Attacher::AttachEngine3D
  Height = 8
  Placement = pos=(3.5,6,0) rot=(0,0,1;0rad)
  Radius = 0.7
FEATURE [Part::Box] Box083  label="RJ054"
  AttacherType = Attacher::AttachEngine3D
  Height = 14.5
  Length = 13
  Placement = pos=(7.5,-4,4.5) rot=(0,0,1;0rad)
  Width = 13
FEATURE [Part::Cylinder] Cylinder014005407  label="Válec389"
  Angle = 360
  AttacherType = Attacher::AttachEngine3D
  Height = 6.5
  Placement = pos=(3.5,21.25,0) rot=(0,0,1;0rad)
  Radius = 3.5
FEATURE [Part::Box] Box084  label="Krychle067"
  AttacherType = Attacher::AttachEngine3D
  Height = 28
  Length = 62
  Placement = pos=(-2.5,-2,-5) rot=(0,0,1;0rad)
  Width = 31
FEATURE [Part::Cut] Cut061098016
  Base = -> Box084
  Tool = -> Box082
FEATURE [Part::MultiFuse] Fusion272
  Shapes = -> [Box079,Box083]
FEATURE [Part::MultiFuse] Fusion274  label="diry010"
  Placement = pos=(0,0,-4) rot=(0,0,1;0rad)
  Shapes = -> [Cylinder014005398,Cylinder014005406,Cylinder014005405,Cylinder014005403]
FEATURE [Part::MultiFuse] Fusion278  label="Horni diry005"
  Placement = pos=(0,0,3) rot=(0,0,1;0rad)
  Shapes = -> [Cylinder014005402,Cylinder014005400]
FEATURE [Part::MultiFuse] Fusion280  label="sloupky003"
  Placement = pos=(0,0,-3.5) rot=(0,0,1;0rad)
  Shapes = -> [Cylinder014005407,Cylinder014005401,Cylinder014005399,Cylinder014005404]
FEATURE [Part::Extrusion] Extrude037  label="Text DEC002"
  Base = -> ShapeString009
  Dir = (0,-1,0)
  DirMode = 2
  FaceMakerClass = Part::FaceMakerBullseye
  LengthFwd = 1
  LengthRev = 0
  Placement = pos=(21,0.5,-35) rot=(0,0,1;0rad)
  Solid = false
  Symmetric = false
FEATURE [Part::Extrusion] Extrude038  label="Text Focuser002"
  Base = -> ShapeString008
  Dir = (0,-1,0)
  DirMode = 2
  FaceMakerClass = Part::FaceMakerBullseye
  LengthFwd = 1
  LengthRev = 0
  Placement = pos=(-11,0.5,-35) rot=(0,0,1;0rad)
  Solid = false
  Symmetric = false
FEATURE [Part::MultiFuse] Fusion275  label="Texty002"
  Placement = pos=(0,0.5,2.5) rot=(0,0,1;0rad)
  Shapes = -> [Extrude038,Extrude037]
FEATURE [Part::Cut] Cut061098018  label="RJ dirama002"
  Base = -> Cut061098016
  Tool = -> Fusion272
FEATURE [Part::MultiFuse] Fusion277
  Shapes = -> [Cut061098018,Fusion280]
FEATURE [Part::Cut] Cut061098015  label="Ze sloupky002"
  Base = -> Fusion277
  Tool = -> Fusion274
FEATURE [Part::MultiFuse] Fusion281
  Shapes = -> [Fusion275,Fusion278]
FEATURE [Part::Cut] Cut061098019  label="Dec zaklad"
  Base = -> Cut061098015
  Placement = pos=(-28.5,18.5,-80) rot=(1,0,0;1.5708rad)
  Tool = -> Fusion281
FEATURE [Part::MultiFuse] Fusion282
  Shapes = -> [Fusion266,Cut061098019]
FEATURE [Part::MultiFuse] Fusion283
  Shapes = -> [Cylinder014005394,Cylinder014005393]
FEATURE [Part::Cut] Cut061098020  label="DEC PCB Box"
  Base = -> Fusion282
  Tool = -> Fusion283
FEATURE [Part::Feature] Cut061098023  label="DEC Motor PG100"
  shape: bbox 42.3 x 42.3 x 110 mm, 26 faces (baked)
FEATURE [App::Part] Part026  label="Weigth"
  Group = -> [Cylinder014005345,Screw006_solid002,Screw006_solid003,Screw006_solid001,Screw006_solid,Cylinder014005351,Cylinder014005347,Cylinder014005348,Cylinder014005346,Fusion217,Fusion219,Cut061093,Nut013,Cut061094,Screw006_solid004,Screw006_solid005,Screw006_solid006,Cylinder014005350,Cylinder014005349,Cylinder014005352,Fusion218,Fusion220,Screw006_solid007,Nut014,Cut061095]
  License = CC BY 3.0
  LicenseURL = http://creativecommons.org/licenses/by/3.0/
  Origin = -> Origin026
  Placement = pos=(0,0,-3) rot=(0,0,1;0rad)
FEATURE [Sketcher::SketchObject] Sketch021
  MapMode = 5
  Placement = pos=(0,40,0) rot=(0,0.707107,0.707107;3.14159rad)
  sketch-geometry (6):
    g0: LineSegment StartX=0 StartY=0 StartZ=0 EndX=0 EndY=3 EndZ=0
    g1: LineSegment StartX=0 StartY=3 StartZ=0 EndX=-4 EndY=10 EndZ=0
    g2: LineSegment StartX=-4 StartY=10 StartZ=0 EndX=-26 EndY=10 EndZ=0
    g3: LineSegment StartX=-26 StartY=10 StartZ=0 EndX=-30 EndY=3 EndZ=0
    g4: LineSegment StartX=-30 StartY=3 StartZ=0 EndX=-30 EndY=0 EndZ=0
    g5: LineSegment StartX=-30 StartY=0 StartZ=0 EndX=0 EndY=0 EndZ=0
  constraints (11):
    c: Coincident(g-1,g0)
    c: PointOnObject(g0,g-2)
    c: Coincident(g0,g1)
    c: Coincident(g1,g2)
    c: Horizontal(g2)
    c: Coincident(g2,g3)
    c: Coincident(g3,g4)
    c: PointOnObject(g4,g-1)
    c: Vertical(g4)
    c: Coincident(g4,g5)
    c: Coincident(g5,g0)
FEATURE [Sketcher::SketchObject] Sketch022
  MapMode = 5
  Placement = pos=(0,0,60) rot=(0,0,1;0rad)
  sketch-geometry (6):
    g0: LineSegment StartX=-18.9734 StartY=34.0308 StartZ=0 EndX=-16.0253 EndY=36.9748 EndZ=0
    g1: LineSegment StartX=18.996 StartY=34.0308 StartZ=0 EndX=16.044 EndY=36.9748 EndZ=0
    g2: LineSegment StartX=18.996 StartY=34.0308 StartZ=0 EndX=-18.9734 EndY=34.0308 EndZ=0
    g3: LineSegment StartX=-18.9734 StartY=40.0311 StartZ=0 EndX=-16.0253 EndY=36.9748 EndZ=0
    g4: LineSegment StartX=16.044 StartY=36.9748 StartZ=0 EndX=18.9109 EndY=40.0311 EndZ=0
    g5: LineSegment StartX=-18.9734 StartY=40.0311 StartZ=0 EndX=18.9109 EndY=40.0311 EndZ=0
  constraints (7):
    c: Coincident(g2,g1)
    c: Coincident(g2,g0)
    c: Horizontal(g2)
    c: Coincident(g3,g0)
    c: Coincident(g5,g3)
    c: Coincident(g5,g4)
    c: Horizontal(g5)
FEATURE [Part::FeaturePython] Screw016  label="M2.5x8-Screw001"  # Fasteners workbench fastener (typed FeaturePython)
  Placement = pos=(-34,0,20) rot=(0,-1,0;1.5708rad)
  diameter = 3
  invert = false
  length = 3
  matchOuter = false
  offset = 0
  thread = false
  type = 12
FEATURE [Part::FeaturePython] Screw017  label="M2.5x8-Screw002"  # Fasteners workbench fastener (typed FeaturePython)
  Placement = pos=(34,0,20) rot=(0,1,0;1.5708rad)
  diameter = 3
  invert = false
  length = 3
  matchOuter = false
  offset = 0
  thread = false
  type = 12
FEATURE [Part::FeaturePython] Screw012  label="M4x20-Screw004"  # Fasteners workbench fastener (typed FeaturePython)
  Placement = pos=(-40.5,-9,53) rot=(1,0,0;1.5708rad)
  diameter = 4
  invert = false
  length = 5
  matchOuter = false
  offset = 0
  thread = false
  type = 5
FEATURE [Part::FeaturePython] Nut021  label="M4-Nut010"  # Fasteners workbench fastener (typed FeaturePython)
  Placement = pos=(-40.2,7,53) rot=(1,0,0;1.5708rad)
  diameter = 6
  invert = false
  matchOuter = false
  offset = 0
  thread = false
  type = 1
FEATURE [Part::FeaturePython] Screw013  label="M4x20-Screw005"  # Fasteners workbench fastener (typed FeaturePython)
  Placement = pos=(-40.5,-9,53) rot=(1,0,0;1.5708rad)
  diameter = 4
  invert = false
  length = 5
  matchOuter = false
  offset = 0
  thread = false
  type = 5
FEATURE [Part::FeaturePython] Screw015  label="M4x20-Screw007"  # Fasteners workbench fastener (typed FeaturePython)
  Placement = pos=(-40.5,-9,53) rot=(1,0,0;1.5708rad)
  diameter = 4
  invert = false
  length = 5
  matchOuter = false
  offset = 0
  thread = false
  type = 5
FEATURE [Part::FeaturePython] Nut022  label="M4-Nut011"  # Fasteners workbench fastener (typed FeaturePython)
  Placement = pos=(-40.2,7,53) rot=(1,0,0;1.5708rad)
  diameter = 6
  invert = false
  matchOuter = false
  offset = 0
  thread = false
  type = 1
FEATURE [Part::FeaturePython] Nut023  label="M4-Nut012"  # Fasteners workbench fastener (typed FeaturePython)
  Placement = pos=(-40.2,7,53) rot=(1,0,0;1.5708rad)
  diameter = 6
  invert = false
  matchOuter = false
  offset = 0
  thread = false
  type = 1
FEATURE [Part::FeaturePython] Nut024  label="M4-Nut013"  # Fasteners workbench fastener (typed FeaturePython)
  Placement = pos=(-40.2,7,53) rot=(1,0,0;1.5708rad)
  diameter = 6
  invert = false
  matchOuter = false
  offset = 0
  thread = false
  type = 1
FEATURE [Part::FeaturePython] Screw014  label="M4x20-Screw006"  # Fasteners workbench fastener (typed FeaturePython)
  Placement = pos=(-40.5,-9,53) rot=(1,0,0;1.5708rad)
  diameter = 4
  invert = false
  length = 5
  matchOuter = false
  offset = 0
  thread = false
  type = 5
FEATURE [Part::Extrusion] Extrude047
  Base = -> Sketch022
  Dir = (0,0,1)
  DirMode = 2
  FaceMakerClass = Part::FaceMakerBullseye
  LengthFwd = -112
  LengthRev = 0
  Solid = true
  Symmetric = false
FEATURE [Part::Extrusion] Extrude003
  Base = -> Sketch021
  Dir = (0,1,0)
  DirMode = 2
  FaceMakerClass = Part::FaceMakerBullseye
  LengthFwd = -40
  LengthRev = 0
  Placement = pos=(-15,0,0) rot=(0,0,1;0rad)
  Solid = true
  Symmetric = false
FEATURE [Part::MultiFuse] Fusion331  label="Srouby004"
  Placement = pos=(80.5,0,-97.5) rot=(0,0,1;0rad)
  Shapes = -> [Screw015,Nut024]
FEATURE [Part::MultiFuse] Fusion336  label="Srouby005"
  Placement = pos=(0,0,-0.5) rot=(0,0,1;0rad)
  Shapes = -> [Screw013,Nut022]
FEATURE [Part::MultiFuse] Fusion001030  label="Srouby006"
  Placement = pos=(80.5,0,-0.5) rot=(0,0,1;0rad)
  Shapes = -> [Screw012,Nut023]
FEATURE [Part::MultiFuse] Fusion100  label="Srouby007"
  Placement = pos=(0,0,-97.5) rot=(0,0,1;0rad)
  Shapes = -> [Screw014,Nut021]
FEATURE [Part::MultiFuse] Fusion332
  Shapes = -> [Fusion336,Fusion001030,Fusion100,Fusion331]
FEATURE [Part::MultiFuse] Fusion009
  Shapes = -> [Screw017,Screw016]
FEATURE [Part::Cylinder] Cylinder014005551  label="Válec481"
  Angle = 360
  AttacherType = Attacher::AttachEngine3D
  Height = 500
  Radius = 28.5
FEATURE [Part::Cylinder] Cylinder014005555  label="Válec484"
  Angle = 360
  AttacherType = Attacher::AttachEngine3D
  Height = 100
  Placement = pos=(-50,33,13) rot=(0,1,0;1.5708rad)
  Radius = 4
FEATURE [Part::Cylinder] Cylinder014005552  label="Válec482"
  Angle = 360
  AttacherType = Attacher::AttachEngine3D
  Height = 500
  Radius = 32
FEATURE [Part::Cut] Cut061176  label="tubus !"
  Base = -> Cylinder014005552
  Tool = -> Cylinder014005551
FEATURE [Part::Cylinder] Cylinder014005563  label="Válec489"
  Angle = 360
  AttacherType = Attacher::AttachEngine3D
  Height = 15
  Placement = pos=(35,33,13) rot=(0,1,0;1.5708rad)
  Radius = 16
FEATURE [Part::Cylinder] Cylinder014005558  label="Lens"
  Angle = 360
  AttacherType = Attacher::AttachEngine3D
  Height = 10
  Placement = pos=(0,0,500) rot=(0,0,1;0rad)
  Radius = 32
FEATURE [Part::Cylinder] Cylinder014005554  label="Válec490"
  Angle = 360
  AttacherType = Attacher::AttachEngine3D
  Height = 40
  Placement = pos=(0,0,0) rot=(0,0,1;3.83972rad)
  Radius = 33.5
FEATURE [Part::Cylinder] Cylinder014005556  label="Válec485"
  Angle = 360
  AttacherType = Attacher::AttachEngine3D
  Height = 15
  Placement = pos=(-50,33,13) rot=(0,1,0;1.5708rad)
  Radius = 16
FEATURE [Part::Box] Box099  label="Krychle082"
  AttacherType = Attacher::AttachEngine3D
  Height = 30
  Length = 24
  Placement = pos=(-12,25,0) rot=(0,0,1;0rad)
  Width = 12
FEATURE [Part::Cylinder] Cylinder014005565  label="Lens001"
  Angle = 360
  AttacherType = Attacher::AttachEngine3D
  Height = 2
  Placement = pos=(0,0,510) rot=(0,0,1;0rad)
  Radius = 32
FEATURE [Part::Box] Box074  label="Krychle061"
  AttacherType = Attacher::AttachEngine3D
  Height = 3
  Length = 13
  Placement = pos=(-6.5,0,-3) rot=(0,0,1;0rad)
  Width = 4
FEATURE [Part::MultiFuse] Fusion001029  label="Dovecot profile002"
  Shapes = -> [Extrude003,Box074]
FEATURE [Part::Cylinder] Cylinder014005564  label="Válec491"
  Angle = 360
  AttacherType = Attacher::AttachEngine3D
  Height = 120
  Placement = pos=(0,0,-80) rot=(0,0,1;0rad)
  Radius = 20.5
FEATURE [Part::Cylinder] Cylinder014005560  label="Válec487"
  Angle = 360
  AttacherType = Attacher::AttachEngine3D
  Height = 120
  Placement = pos=(0,0,-80) rot=(0,0,1;0rad)
  Radius = 23
FEATURE [Part::Cut] Cut061023
  Base = -> Cylinder014005560
  Tool = -> Cylinder014005564
FEATURE [Part::Cylinder] Cylinder014005561  label="Válec488"
  Angle = 360
  AttacherType = Attacher::AttachEngine3D
  Height = 30
  Radius = 23
FEATURE [Part::Cylinder] Cylinder014005559  label="Válec486"
  Angle = 360
  AttacherType = Attacher::AttachEngine3D
  Height = 30
  Radius = 28
FEATURE [Part::Box] Box100  label="Krychle064"
  AttacherType = Attacher::AttachEngine3D
  Height = 40
  Length = 36
  Placement = pos=(-18,-36,0) rot=(0,0,1;0rad)
  Width = 10
FEATURE [Part::Box] Box101  label="Krychle060"
  AttacherType = Attacher::AttachEngine3D
  Height = 15
  Length = 36
  Placement = pos=(-18,0,-5) rot=(0,0,1;0rad)
  Width = 40
FEATURE [Part::Cut] Cut061175
  Base = -> Box101
  Tool = -> Fusion001029
FEATURE [Part::Chamfer] Chamfer012
  Base = -> Cut061175
  Edges = 2 edges r=5: [Edge2,Edge29]
FEATURE [Part::Box] Box075  label="Krychle083"
  AttacherType = Attacher::AttachEngine3D
  Height = 30
  Length = 24
  Placement = pos=(-12,25,0) rot=(0,0,1;0rad)
  Width = 12
FEATURE [Part::Box] Box076  label="Krychle084"
  AttacherType = Attacher::AttachEngine3D
  Height = 30
  Length = 20
  Placement = pos=(-10,-32,0) rot=(0,0,1;0rad)
  Width = 5
FEATURE [Part::MultiFuse] Fusion121
  Shapes = -> [Box076,Box075]
FEATURE [Part::Cut] Cut061173  label="Tubus"
  Base = -> Cut061176
  Tool = -> Fusion121
FEATURE [Part::Cylinder] Cylinder014005553  label="Válec483"
  Angle = 360
  AttacherType = Attacher::AttachEngine3D
  Height = 40
  Placement = pos=(0,0,0) rot=(0,0,1;0.872665rad)
  Radius = 32
FEATURE [Part::Cylinder] Cylinder014005557  label="LensH001"
  Angle = 360
  AttacherType = Attacher::AttachEngine3D
  Height = 80
  Placement = pos=(0,0,500) rot=(0,0,1;0rad)
  Radius = 32
FEATURE [Part::Box] Box102  label="Krychle065"
  AttacherType = Attacher::AttachEngine3D
  Height = 30
  Length = 20
  Placement = pos=(-10,-32,0) rot=(0,0,1;0rad)
  Width = 5
FEATURE [Part::MultiFuse] Fusion122
  Shapes = -> [Box099,Box102,Cylinder014005559]
FEATURE [Part::Cut] Cut061177
  Base = -> Fusion122
  Tool = -> Cylinder014005561
FEATURE [Part::MultiFuse] Fusion123  label="Focuser"
  Shapes = -> [Cut061023,Cut061177,Cylinder014005555,Cylinder014005556,Cylinder014005563]
FEATURE [Part::Cylinder] Cylinder014005562  label="LensH"
  Angle = 360
  AttacherType = Attacher::AttachEngine3D
  Height = 80
  Placement = pos=(0,0,500) rot=(0,0,1;0rad)
  Radius = 37
FEATURE [Part::Cut] Cut061024
  Base = -> Cylinder014005562
  Placement = pos=(0,0,-30) rot=(0,0,1;0rad)
  Tool = -> Cylinder014005557
FEATURE [Part::Cylinder] Cylinder014005566  label="Lens002"
  Angle = 360
  AttacherType = Attacher::AttachEngine3D
  Height = 2
  Placement = pos=(0,0,510) rot=(0,0,1;0rad)
  Radius = 30
FEATURE [Part::Cut] Cut061025
  Base = -> Cylinder014005565
  Tool = -> Cylinder014005566
FEATURE [Part::MultiFuse] Fusion124
  Shapes = -> [Cut061025,Cut061024]
FEATURE [Part::Box] Box103  label="mezara002"
  AttacherType = Attacher::AttachEngine3D
  Height = 15
  Length = 90
  Placement = pos=(-45,-3,45) rot=(0,0,1;0rad)
  Width = 3
FEATURE [Part::Box] Box104  label="Krychle085"
  AttacherType = Attacher::AttachEngine3D
  Height = 15
  Length = 90
  Placement = pos=(-45,-10,45) rot=(0,0,1;0rad)
  Width = 17
FEATURE [Part::Cylinder] Cylinder014005546  label="tubus003"
  Angle = 360
  AttacherType = Attacher::AttachEngine3D
  Height = 112
  Placement = pos=(0,-1,-52) rot=(0,0,1;0rad)
  Radius = 32
FEATURE [Part::Cylinder] Cylinder014005547  label="tubus004"
  Angle = 360
  AttacherType = Attacher::AttachEngine3D
  Height = 15
  Placement = pos=(0,-1,-52) rot=(0,0,1;0rad)
  Radius = 37
FEATURE [Part::Box] Box105  label="Krychle086"
  AttacherType = Attacher::AttachEngine3D
  Height = 112
  Length = 38
  Placement = pos=(-19,32,-52) rot=(0,0,1;0rad)
  Width = 10
FEATURE [Part::Cylinder] Cylinder014005548  label="tubus005"
  Angle = 360
  AttacherType = Attacher::AttachEngine3D
  Height = 15
  Placement = pos=(0,-1,45) rot=(0,0,1;0rad)
  Radius = 37
FEATURE [Part::Box] Box106  label="Krychle087"
  AttacherType = Attacher::AttachEngine3D
  Height = 112
  Length = 38
  Placement = pos=(-19,34,-52) rot=(0,0,1;0rad)
  Width = 6
FEATURE [Part::Cut] Cut061179
  Base = -> Box105
  Tool = -> Box106
FEATURE [Part::MultiFuse] Fusion335  label="Arca plate base008"
  Placement = pos=(0,-0.5,0) rot=(0,0,1;0rad)
  Shapes = -> [Extrude047,Cut061179]
FEATURE [Part::Box] Box107  label="mezara003"
  AttacherType = Attacher::AttachEngine3D
  Height = 15
  Length = 90
  Placement = pos=(-45,-3,-52) rot=(0,0,1;0rad)
  Width = 3
FEATURE [Part::MultiFuse] Fusion001028
  Shapes = -> [Box103,Box107,Cylinder014005546]
FEATURE [Part::Cylinder] Cylinder014005550  label="Válec480"
  Angle = 360
  AttacherType = Attacher::AttachEngine3D
  Height = 10
  Placement = pos=(12,20,4) rot=(0,1,0;0.785398rad)
  Radius = 1.4
FEATURE [Part::Box] Box108  label="Krychle088"
  AttacherType = Attacher::AttachEngine3D
  Height = 15
  Length = 90
  Placement = pos=(-45,-10,-52) rot=(0,0,1;0rad)
  Width = 17
FEATURE [Part::MultiFuse] Fusion337
  Shapes = -> [Fusion335,Cylinder014005547,Cylinder014005548,Box104,Box108]
FEATURE [Part::Cut] Cut061178
  Base = -> Fusion337
  Tool = -> Fusion001028
FEATURE [Part::Cut] Cut061172  label="Swiss Arca holder"
  Base = -> Cut061178
  Placement = pos=(0,0,224) rot=(0,0,1;0rad)
  Tool = -> Fusion332
FEATURE [Part::Cylinder] Cylinder014005549  label="Válec479"
  Angle = 360
  AttacherType = Attacher::AttachEngine3D
  Height = 10
  Placement = pos=(-12,20,4) rot=(0,-1,0;0.785398rad)
  Radius = 1.4
FEATURE [Part::MultiFuse] Fusion334
  Shapes = -> [Cylinder014005550,Cylinder014005549]
FEATURE [Part::Cut] Cut005  label="Dov holder003"
  Base = -> Chamfer012
  Placement = pos=(0,-39,0) rot=(1,0,0;1.5708rad)
  Tool = -> Fusion334
FEATURE [Part::MultiFuse] Fusion333
  Shapes = -> [Cylinder014005554,Cut005,Box100]
FEATURE [Part::Cut] Cut061174
  Base = -> Fusion333
  Tool = -> Cylinder014005553
FEATURE [Part::Cut] Cut007  label="Telscop dovetail holder"
  Base = -> Cut061174
  Placement = pos=(0,0,79) rot=(0,0,1;0rad)
  Tool = -> Fusion009
FEATURE [App::Part] Part040  label="DIY telescope"
  Group = -> [Cut061176,Cylinder014005551,Cylinder014005552,Box076,Box075,Fusion121,Cut061173,Cylinder014005556,Cylinder014005561,Cylinder014005564,Cylinder014005563,Cylinder014005559,Cylinder014005555,Cylinder014005560,Box099,Cut061023,Cut061177,Box102,Fusion122,Fusion123,Cylinder014005558,Cylinder014005562,Cylinder014005565,Cylinder014005557,Cut061024,Cut061025,Cylinder014005566,Fusion124,Fusion001028,+49 more]
  License = CC BY 3.0
  LicenseURL = http://creativecommons.org/licenses/by/3.0/
  Origin = -> Origin040
  Placement = pos=(0,113,-118) rot=(0,0,1;3.14159rad)
FEATURE [Sketcher::SketchObject] Sketch039
  MapMode = 5
  Placement = pos=(0,0,60) rot=(0,0,1;0rad)
  sketch-geometry (6):
    g0: LineSegment StartX=-18.9734 StartY=34.0308 StartZ=0 EndX=-16.0253 EndY=36.9748 EndZ=0
    g1: LineSegment StartX=18.996 StartY=34.0308 StartZ=0 EndX=16.044 EndY=36.9748 EndZ=0
    g2: LineSegment StartX=18.996 StartY=34.0308 StartZ=0 EndX=-18.9734 EndY=34.0308 EndZ=0
    g3: LineSegment StartX=-18.9734 StartY=40.0311 StartZ=0 EndX=-16.0253 EndY=36.9748 EndZ=0
    g4: LineSegment StartX=16.044 StartY=36.9748 StartZ=0 EndX=18.9109 EndY=40.0311 EndZ=0
    g5: LineSegment StartX=-18.9734 StartY=40.0311 StartZ=0 EndX=18.9109 EndY=40.0311 EndZ=0
  constraints (7):
    c: Coincident(g2,g1)
    c: Coincident(g2,g0)
    c: Horizontal(g2)
    c: Coincident(g3,g0)
    c: Coincident(g5,g3)
    c: Coincident(g5,g4)
    c: Horizontal(g5)
FEATURE [Sketcher::SketchObject] Sketch040
  MapMode = 5
  Placement = pos=(0,0,60) rot=(0,0,1;0rad)
  sketch-geometry (6):
    g0: LineSegment StartX=-18.9734 StartY=34.0308 StartZ=0 EndX=-16.0253 EndY=36.9748 EndZ=0
    g1: LineSegment StartX=18.996 StartY=34.0308 StartZ=0 EndX=16.044 EndY=36.9748 EndZ=0
    g2: LineSegment StartX=18.996 StartY=34.0308 StartZ=0 EndX=-18.9734 EndY=34.0308 EndZ=0
    g3: LineSegment StartX=-18.9734 StartY=40.0311 StartZ=0 EndX=-16.0253 EndY=36.9748 EndZ=0
    g4: LineSegment StartX=16.044 StartY=36.9748 StartZ=0 EndX=18.9109 EndY=40.0311 EndZ=0
    g5: LineSegment StartX=-18.9734 StartY=40.0311 StartZ=0 EndX=18.9109 EndY=40.0311 EndZ=0
  constraints (7):
    c: Coincident(g2,g1)
    c: Coincident(g2,g0)
    c: Horizontal(g2)
    c: Coincident(g3,g0)
    c: Coincident(g5,g3)
    c: Coincident(g5,g4)
    c: Horizontal(g5)
FEATURE [Sketcher::SketchObject] Sketch041
  MapMode = 5
  Placement = pos=(0,0,60) rot=(0,0,1;0rad)
  sketch-geometry (6):
    g0: LineSegment StartX=-18.9734 StartY=34.0308 StartZ=0 EndX=-16.0253 EndY=36.9748 EndZ=0
    g1: LineSegment StartX=18.996 StartY=34.0308 StartZ=0 EndX=16.044 EndY=36.9748 EndZ=0
    g2: LineSegment StartX=18.996 StartY=34.0308 StartZ=0 EndX=-18.9734 EndY=34.0308 EndZ=0
    g3: LineSegment StartX=-18.9734 StartY=40.0311 StartZ=0 EndX=-16.0253 EndY=36.9748 EndZ=0
    g4: LineSegment StartX=16.044 StartY=36.9748 StartZ=0 EndX=18.9109 EndY=40.0311 EndZ=0
    g5: LineSegment StartX=-18.9734 StartY=40.0311 StartZ=0 EndX=18.9109 EndY=40.0311 EndZ=0
  constraints (7):
    c: Coincident(g2,g1)
    c: Coincident(g2,g0)
    c: Horizontal(g2)
    c: Coincident(g3,g0)
    c: Coincident(g5,g3)
    c: Coincident(g5,g4)
    c: Horizontal(g5)
FEATURE [Part::Box] Box109  label="Krychle091"
  AttacherType = Attacher::AttachEngine3D
  Height = 15
  Length = 50
  Placement = pos=(-25,-25,64) rot=(0,0,1;0rad)
  Width = 50
FEATURE [Part::Box] Box110  label="Krychle092"
  AttacherType = Attacher::AttachEngine3D
  Height = 20
  Length = 60
  Placement = pos=(-14,-30,62) rot=(0,0,1;0rad)
  Width = 60
FEATURE [Part::Box] Box111  label="Krychle096"
  AttacherType = Attacher::AttachEngine3D
  Height = 2.5
  Length = 12
  Placement = pos=(-6,-25,71) rot=(0,0,1;0rad)
  Width = 13
FEATURE [Part::Box] Box112  label="Krychle093"
  AttacherType = Attacher::AttachEngine3D
  Height = 15
  Length = 50
  Placement = pos=(-25,-25,64) rot=(0,0,1;0rad)
  Width = 50
FEATURE [Part::Cylinder] Cylinder014005644  label="Válec564"
  Angle = 360
  AttacherType = Attacher::AttachEngine3D
  Height = 60
  Placement = pos=(-30,17,69) rot=(0,1,0;1.5708rad)
  Radius = 2.7
FEATURE [Part::Box] Box113  label="Krychle099"
  AttacherType = Attacher::AttachEngine3D
  Height = 8
  Length = 50
  Placement = pos=(-25,0,3) rot=(0,0,1;0rad)
  Width = 82
FEATURE [Part::Cylinder] Cylinder014005353  label="Válec559"
  Angle = 360
  AttacherType = Attacher::AttachEngine3D
  Height = 60
  Placement = pos=(-30,17,69) rot=(0,1,0;1.5708rad)
  Radius = 2.7
FEATURE [Part::Box] Box114  label="Krychle089"
  AttacherType = Attacher::AttachEngine3D
  Height = 112
  Length = 38
  Placement = pos=(-19,32,-52) rot=(0,0,1;0rad)
  Width = 10
FEATURE [Part::Box] Box115  label="Krychle090"
  AttacherType = Attacher::AttachEngine3D
  Height = 112
  Length = 38
  Placement = pos=(-19,34,-52) rot=(0,0,1;0rad)
  Width = 6
FEATURE [Part::Cut] Cut061230
  Base = -> Box114
  Tool = -> Box115
FEATURE [Part::Cylinder] Cylinder014005640  label="Válec560"
  Angle = 360
  AttacherType = Attacher::AttachEngine3D
  Height = 2.5
  Placement = pos=(0,-12,71) rot=(0,0,1;0rad)
  Radius = 6
FEATURE [Part::Cylinder] Cylinder014005641  label="Válec561"
  Angle = 360
  AttacherType = Attacher::AttachEngine3D
  Height = 2.5
  Placement = pos=(0,-12,71) rot=(0,0,1;0rad)
  Radius = 6
FEATURE [Part::Cylinder] Cylinder014005642  label="Válec562"
  Angle = 360
  AttacherType = Attacher::AttachEngine3D
  Height = 2.5
  Placement = pos=(0,-12,71) rot=(0,0,1;0rad)
  Radius = 6
FEATURE [Part::Box] Box116  label="Krychle094"
  AttacherType = Attacher::AttachEngine3D
  Height = 112
  Length = 38
  Placement = pos=(-19,34,-52) rot=(0,0,1;0rad)
  Width = 6
FEATURE [Part::Box] Box117  label="Krychle095"
  AttacherType = Attacher::AttachEngine3D
  Height = 15
  Length = 2
  Placement = pos=(-15.5,-26,61) rot=(0,0,1;0rad)
  Width = 52
FEATURE [Part::Box] Box118  label="Krychle097"
  AttacherType = Attacher::AttachEngine3D
  Height = 2.5
  Length = 12
  Placement = pos=(-6,-25,71) rot=(0,0,1;0rad)
  Width = 13
FEATURE [Part::Cylinder] Cylinder014005643  label="Válec563"
  Angle = 360
  AttacherType = Attacher::AttachEngine3D
  Height = 18
  Placement = pos=(0,70,0) rot=(0,0,1;0rad)
  Radius = 3
FEATURE [Part::Box] Box119  label="Krychle098"
  AttacherType = Attacher::AttachEngine3D
  Height = 0.6
  Length = 15
  Placement = pos=(-28.5,-30,63.6) rot=(0,0,1;0rad)
  Width = 60
FEATURE [Part::Box] Box120  label="Krychle104"
  AttacherType = Attacher::AttachEngine3D
  Height = 15
  Length = 2
  Placement = pos=(-15.5,-26,61) rot=(0,0,1;0rad)
  Width = 52
FEATURE [Part::Box] Box121  label="Krychle105"
  AttacherType = Attacher::AttachEngine3D
  Height = 15
  Length = 50
  Placement = pos=(-25,-25,64) rot=(0,0,1;0rad)
  Width = 50
FEATURE [Part::Box] Box122  label="Krychle106"
  AttacherType = Attacher::AttachEngine3D
  Height = 112
  Length = 38
  Placement = pos=(-19,32,-52) rot=(0,0,1;0rad)
  Width = 10
FEATURE [Part::Cylinder] Cylinder014005650  label="Válec570"
  Angle = 360
  AttacherType = Attacher::AttachEngine3D
  Height = 2.5
  Placement = pos=(0,-12,71) rot=(0,0,1;0rad)
  Radius = 6
FEATURE [Part::Cylinder] Cylinder014005648  label="Válec568"
  Angle = 360
  AttacherType = Attacher::AttachEngine3D
  Height = 60
  Placement = pos=(-30,-17,69) rot=(0,1,0;1.5708rad)
  Radius = 2.7
FEATURE [Part::Box] Box123  label="Krychle107"
  AttacherType = Attacher::AttachEngine3D
  Height = 15
  Length = 2
  Placement = pos=(-15.5,-26,61) rot=(0,0,1;0rad)
  Width = 52
FEATURE [Part::Box] Box124  label="Krychle102"
  AttacherType = Attacher::AttachEngine3D
  Height = 112
  Length = 38
  Placement = pos=(-19,32,-52) rot=(0,0,1;0rad)
  Width = 10
FEATURE [Part::Cylinder] Cylinder014005646  label="Válec566"
  Angle = 360
  AttacherType = Attacher::AttachEngine3D
  Height = 18
  Placement = pos=(0,45,3) rot=(0,0,1;0rad)
  Radius = 4.35
FEATURE [Part::Box] Box125  label="Krychle100"
  AttacherType = Attacher::AttachEngine3D
  Height = 15
  Length = 2
  Placement = pos=(-15.5,-26,64) rot=(0,0,1;0rad)
  Width = 52
FEATURE [Part::Cylinder] Cylinder014005649  label="Válec569"
  Angle = 360
  AttacherType = Attacher::AttachEngine3D
  Height = 10
  Placement = pos=(0,15,48) rot=(0,0,1;0rad)
  Radius = 5.2
FEATURE [Part::Cylinder] Cylinder014005651  label="Válec571"
  Angle = 360
  AttacherType = Attacher::AttachEngine3D
  Height = 2.5
  Placement = pos=(0,-12,71) rot=(0,0,1;0rad)
  Radius = 6
FEATURE [Part::Cylinder] Cylinder014005647  label="Válec567"
  Angle = 360
  AttacherType = Attacher::AttachEngine3D
  Height = 2.5
  Placement = pos=(0,-12,71) rot=(0,0,1;0rad)
  Radius = 6
FEATURE [Part::Box] Box126  label="Krychle108"
  AttacherType = Attacher::AttachEngine3D
  Height = 112
  Length = 38
  Placement = pos=(-19,34,-52) rot=(0,0,1;0rad)
  Width = 6
FEATURE [Part::Box] Box045  label="Krychle038"
  AttacherType = Attacher::AttachEngine3D
  Height = 2.5
  Length = 12
  Placement = pos=(-6,-25,71) rot=(0,0,1;0rad)
  Width = 13
FEATURE [Part::Cylinder] Cylinder014005653  label="Válec573"
  Angle = 360
  AttacherType = Attacher::AttachEngine3D
  Height = 60
  Placement = pos=(-30,17,69) rot=(0,1,0;1.5708rad)
  Radius = 2.7
FEATURE [Part::Cylinder] Cylinder014005645  label="Válec565"
  Angle = 360
  AttacherType = Attacher::AttachEngine3D
  Height = 18
  Placement = pos=(0,45,6) rot=(0,0,1;0rad)
  Radius = 4.9
FEATURE [Part::Cylinder] Cylinder014005654  label="Válec574"
  Angle = 360
  AttacherType = Attacher::AttachEngine3D
  Height = 60
  Placement = pos=(-30,-17,69) rot=(0,1,0;1.5708rad)
  Radius = 2.7
FEATURE [Part::Box] Box127  label="Krychle103"
  AttacherType = Attacher::AttachEngine3D
  Height = 2.5
  Length = 12
  Placement = pos=(-6,-25,71) rot=(0,0,1;0rad)
  Width = 13
FEATURE [Part::Box] Box128  label="Krychle101"
  AttacherType = Attacher::AttachEngine3D
  Height = 20
  Length = 60
  Placement = pos=(-14,-30,62) rot=(0,0,1;0rad)
  Width = 60
FEATURE [Part::Cylinder] Cylinder014005652  label="Válec572"
  Angle = 360
  AttacherType = Attacher::AttachEngine3D
  Height = 60
  Placement = pos=(-30,-17,69) rot=(0,1,0;1.5708rad)
  Radius = 2.7
FEATURE [Part::Box] Box129  label="Krychle109"
  AttacherType = Attacher::AttachEngine3D
  Height = 2.5
  Length = 12
  Placement = pos=(-6,-25,71) rot=(0,0,1;0rad)
  Width = 13
FEATURE [Part::Box] Box130  label="Krychle110"
  AttacherType = Attacher::AttachEngine3D
  Height = 2.5
  Length = 12
  Placement = pos=(-6,-25,71) rot=(0,0,1;0rad)
  Width = 13
FEATURE [Part::Extrusion] Extrude066
  Base = -> Sketch040
  Dir = (0,0,1)
  DirMode = 2
  FaceMakerClass = Part::FaceMakerBullseye
  LengthFwd = -112
  LengthRev = 0
  Solid = true
  Symmetric = false
FEATURE [Part::Extrusion] Extrude067
  Base = -> Sketch041
  Dir = (0,0,1)
  DirMode = 2
  FaceMakerClass = Part::FaceMakerBullseye
  LengthFwd = -112
  LengthRev = 0
  Solid = true
  Symmetric = false
FEATURE [Part::Extrusion] Extrude065
  Base = -> Sketch039
  Dir = (0,0,1)
  DirMode = 2
  FaceMakerClass = Part::FaceMakerBullseye
  LengthFwd = -112
  LengthRev = 0
  Solid = true
  Symmetric = false
FEATURE [Part::MultiFuse] Fusion001032
  Placement = pos=(0,0,1) rot=(0,0,1;3.14159rad)
  Shapes = -> [Box118,Cylinder014005641]
FEATURE [Part::MultiFuse] Fusion001033
  Shapes = -> [Cylinder014005353,Cylinder014005654]
FEATURE [Part::MultiFuse] Fusion394
  Placement = pos=(0,0,1) rot=(0,0,1;3.14159rad)
  Shapes = -> [Box130,Cylinder014005640]
FEATURE [Part::MultiFuse] Fusion001034
  Shapes = -> [Cylinder014005653,Cylinder014005652]
FEATURE [Part::MultiFuse] Fusion391
  Shapes = -> [Box119,Box125]
FEATURE [Part::MultiFuse] Fusion001035
  Placement = pos=(0,0,1) rot=(0,0,1;3.14159rad)
  Shapes = -> [Box129,Cylinder014005651]
FEATURE [Part::MultiFuse] Fusion393  label="Arca plate base013"
  Placement = pos=(0,-6.5,115.5) rot=(-1,0,0;1.5708rad)
  Shapes = -> [Extrude065,Cut061230]
FEATURE [Part::Cut] Cut061231  label="Arca sw 006"
  Base = -> Box109
  Tool = -> Fusion393
FEATURE [Part::Cut] Cut061227
  Base = -> Cut061231
  Tool = -> Box120
FEATURE [Sketcher::SketchObject] Sketch038
  MapMode = 5
  Placement = pos=(25,0,0) rot=(0.57735,0.57735,0.57735;2.0944rad)
  Support = -> [Cut061227]
  sketch-geometry (3):
    g0: LineSegment StartX=-8.69466 StartY=63.7145 StartZ=0 EndX=24.7095 EndY=63.7145 EndZ=0
    g1: LineSegment StartX=24.7095 StartY=63.7145 StartZ=0 EndX=8 EndY=54 EndZ=0
    g2: LineSegment StartX=8 StartY=54 StartZ=0 EndX=-8.69466 EndY=63.7145 EndZ=0
  constraints (4):
    c: Horizontal(g0)
    c: Coincident(g0,g1)
    c: Coincident(g1,g2)
    c: Coincident(g2,g0)
FEATURE [Part::Extrusion] Extrude068
  Base = -> Sketch038
  Dir = (1,0,0)
  DirMode = 2
  FaceMakerClass = Part::FaceMakerBullseye
  LengthFwd = -50
  LengthRev = 0
  Placement = pos=(0,-0.5,0.5) rot=(0,0,1;0rad)
  Solid = true
  Symmetric = false
FEATURE [Part::MultiFuse] Fusion387
  Shapes = -> [Cylinder014005644,Cylinder014005648]
FEATURE [Part::MultiFuse] Fusion207
  Placement = pos=(0,0,1) rot=(0,0,1;0rad)
  Shapes = -> [Box045,Cylinder014005650,Fusion001035]
FEATURE [Part::MultiFuse] Fusion001037
  Placement = pos=(0,0,1) rot=(0,0,1;0rad)
  Shapes = -> [Box111,Cylinder014005642,Fusion001032]
FEATURE [Part::MultiFuse] Fusion001036  label="diry012"
  Shapes = -> [Fusion001033,Fusion001037]
FEATURE [Part::MultiFuse] Fusion001038  label="diry009"
  Shapes = -> [Fusion001034,Fusion207]
FEATURE [Part::MultiFuse] Fusion389
  Shapes = -> [Cylinder014005643,Cylinder014005645,Cylinder014005646]
FEATURE [Part::Cut] Cut061232  label="deska009"
  Base = -> Box113
  Placement = pos=(0,-26.5,61.5) rot=(-1,0,0;0.523599rad)
  Tool = -> Fusion389
FEATURE [Part::MultiFuse] Fusion388
  Shapes = -> [Cut061227,Extrude068,Cut061232]
FEATURE [Part::MultiFuse] Fusion392
  Placement = pos=(0,0,1) rot=(0,0,1;0rad)
  Shapes = -> [Box127,Cylinder014005647,Fusion394]
FEATURE [Part::MultiFuse] Fusion390  label="diry011"
  Shapes = -> [Fusion387,Fusion392]
FEATURE [Part::Cut] Cut061228
  Base = -> Fusion388
  Tool = -> Fusion390
FEATURE [Part::Cut] Cut061229  label="wood-tripod-plate"
  Base = -> Cut061228
  Placement = pos=(0,-1,0) rot=(1,0,0;0.523599rad)
  Tool = -> Fusion391
FEATURE [Part::Cut] Cut061237
  Base = -> Box124
  Tool = -> Box116
FEATURE [Part::MultiFuse] Fusion001031  label="Arca plate base011"
  Placement = pos=(0,-6.5,115.5) rot=(-1,0,0;1.5708rad)
  Shapes = -> [Extrude067,Cut061237]
FEATURE [Part::Cut] Cut061236  label="Arca sw 008"
  Base = -> Box112
  Tool = -> Fusion001031
FEATURE [Part::Cut] Cut061098037
  Base = -> Cut061236
  Tool = -> Box117
FEATURE [Part::Cut] Cut061086  label="wod-tripod-plate"
  Base = -> Cut061229
  Tool = -> Cylinder014005649
FEATURE [Part::Cut] Cut061098039
  Base = -> Box122
  Tool = -> Box126
FEATURE [Part::MultiFuse] Fusion208  label="Arca plate base012"
  Placement = pos=(0,-6.5,115.5) rot=(-1,0,0;1.5708rad)
  Shapes = -> [Extrude066,Cut061098039]
FEATURE [Part::Cut] Cut061234  label="Arca sw 007"
  Base = -> Box121
  Tool = -> Fusion208
FEATURE [Part::Cut] Cut061098038
  Base = -> Cut061234
  Tool = -> Box123
FEATURE [Part::Cut] Cut061098036
  Base = -> Cut061098038
  Tool = -> Fusion001038
FEATURE [Part::Cut] Cut061233  label="SwissAcaB"
  Base = -> Cut061098036
  Placement = pos=(0,-1,0) rot=(1,0,0;0.523599rad)
  Tool = -> Box128
FEATURE [Part::Cut] Cut061238  label="wood-tripod-arca"
  Base = -> Cut061086
  Tool = -> Cut061233
FEATURE [Part::Cut] Cut061235
  Base = -> Cut061098037
  Tool = -> Fusion001036
FEATURE [Part::Cut] Cut061096  label="SwissAcaB001"
  Base = -> Cut061235
  Placement = pos=(0,-1,0) rot=(1,0,0;0.523599rad)
  Tool = -> Box110
FEATURE [App::Part] Part
  Group = -> [Cylinder014005652,Box129,Box128,Box130,Box127,Cut061233,Cut061229,Cut061232,Cut061228,Cut061231,Cut061098036,Cut061227,Cut061230,Cut061098038,Cut061086,Cut061234,Cut061098039,Extrude068,Extrude065,Extrude066,Sketch038,Sketch039,Sketch040,Cylinder014005648,Box113,Box125,Box119,Cylinder014005640,Box115,Box121,Cylinder014005644,Box122,Cylinder014005650,Box109,Cylinder014005643,Box114,Box120,Box123,+45 more]
  License = CC BY 3.0
  LicenseURL = http://creativecommons.org/licenses/by/3.0/
  Origin = -> Origin
  Placement = pos=(0,0,0) rot=(0,1,0;3.14159rad)
FEATURE [App::Part] Part053  label="wood-tripod-plate001"
  Group = -> [Part]
  License = CC BY 3.0
  LicenseURL = http://creativecommons.org/licenses/by/3.0/
  Origin = -> Origin053
  Placement = pos=(0,-116,-2) rot=(1,0,0;2.0944rad)
FEATURE [Part::Feature] Cut061098044  label="Motor PG101"
  Placement = pos=(0,0,1) rot=(0,0,1;0rad)
  shape: bbox 42.3 x 42.3 x 110 mm, 26 faces (baked)
FEATURE [Part::Feature] Part__Feature  label="17HS15-1684S-PG100"
  shape: bbox 42.88 x 42.36 x 45 mm, 226 faces (baked)
FEATURE [Part::Feature] Part__Feature001  label="17HS15-1684S-PG101"
  shape: bbox 36 x 36 x 32.7 mm, 6 faces (baked)
FEATURE [Part::Feature] Part__Feature002  label="17HS15-1684S-PG102"
  shape: bbox 37.34 x 37.34 x 25 mm, 115 faces (baked)
FEATURE [App::Part] _7HS15_1684S_PG100
  Group = -> [Part__Feature,Part__Feature001,Part__Feature002,Cut061098044]
  License = CC BY 3.0
  LicenseURL = http://creativecommons.org/licenses/by/3.0/
  Origin = -> Origin055
  Placement = pos=(0,0,1) rot=(0,0,1;-1.5708rad)
FEATURE [Part::Cylinder] Cylinder014005671  label="Válec590"
  Angle = 360
  AttacherType = Attacher::AttachEngine3D
  Height = 59
  Placement = pos=(0,0,-18) rot=(0,0,1;0rad)
  Radius = 18.5
FEATURE [Part::Box] Box142  label="Krychle119"
  AttacherType = Attacher::AttachEngine3D
  Height = 49
  Length = 43
  Placement = pos=(-21.5,-20.5,1) rot=(0,0,1;0rad)
  Width = 42
FEATURE [Part::Feature] Chamfer008010  label="Zaklad007"
  shape: bbox 61 x 63.5 x 101.5 mm, 101 faces (baked)
FEATURE [Part::Cylinder] Cylinder014005674  label="Válec593"
  Angle = 360
  AttacherType = Attacher::AttachEngine3D
  Height = 40
  Placement = pos=(-40,1,-17.5) rot=(0,1,0;1.5708rad)
  Radius = 1.2
FEATURE [Part::Box] Box143  label="Krychle120"
  AttacherType = Attacher::AttachEngine3D
  Height = 13
  Length = 2
  Placement = pos=(29,-4.5,-55) rot=(0,0,1;0rad)
  Width = 28
FEATURE [Part::Cylinder] Cylinder014005675  label="Válec594"
  Angle = 360
  AttacherType = Attacher::AttachEngine3D
  Height = 74
  Placement = pos=(-40,19,-46.5) rot=(0,1,0;1.5708rad)
  Radius = 1.2
FEATURE [Part::Box] Box144  label="Krychle121"
  AttacherType = Attacher::AttachEngine3D
  Height = 13
  Length = 2
  Placement = pos=(-31,-4.5,-55) rot=(0,0,1;0rad)
  Width = 28
FEATURE [Part::Cylinder] Cylinder014005676  label="Válec595"
  Angle = 360
  AttacherType = Attacher::AttachEngine3D
  Height = 74
  Placement = pos=(-40,0,-46.5) rot=(0,1,0;1.5708rad)
  Radius = 1.2
FEATURE [Part::Cylinder] Cylinder014005677  label="Válec596"
  Angle = 360
  AttacherType = Attacher::AttachEngine3D
  Height = 40
  Placement = pos=(-40,16,-17.5) rot=(0,1,0;1.5708rad)
  Radius = 1.2
FEATURE [Part::MultiFuse] Fusion001052
  Shapes = -> [Cylinder014005676,Cylinder014005675]
FEATURE [Part::MultiFuse] Fusion001053
  Shapes = -> [Box143,Box144]
FEATURE [Part::MultiFuse] Fusion001051
  Shapes = -> [Fusion001053,Fusion001052]
FEATURE [Part::Cut] Cut061098047  label="Zaklad 002"
  Base = -> Chamfer008010
  Tool = -> Fusion001051
FEATURE [Part::MultiFuse] Fusion001054
  Shapes = -> [Cylinder014005674,Cylinder014005677]
FEATURE [Part::Cut] Cut061098046  label="RA Zaklad002"
  Base = -> Cut061098047
  Tool = -> Fusion001054
FEATURE [Part::Chamfer] Chamfer
  Base = -> Box142
  Edges = 2 edges r=5: [Edge1,Edge5]
FEATURE [Part::Box] Box145  label="Krychle122"
  AttacherType = Attacher::AttachEngine3D
  Height = 10
  Length = 43
  Placement = pos=(-21.5,-20.5,0) rot=(0,0,1;0rad)
  Width = 42
FEATURE [Part::Cylinder] Cylinder014005679  label="Válec598"
  Angle = 360
  AttacherType = Attacher::AttachEngine3D
  Height = 50
  Placement = pos=(9.9,9.9,0) rot=(0,0,1;0rad)
  Radius = 1.6
FEATURE [Part::Cylinder] Cylinder014005680  label="Válec599"
  Angle = 360
  AttacherType = Attacher::AttachEngine3D
  Height = 50
  Placement = pos=(-9.9,9.9,0) rot=(0,0,1;0rad)
  Radius = 1.6
FEATURE [Part::Cylinder] Cylinder014005681  label="Válec600"
  Angle = 360
  AttacherType = Attacher::AttachEngine3D
  Height = 50
  Placement = pos=(-9.9,-9.9,0) rot=(0,0,1;0rad)
  Radius = 1.6
FEATURE [Part::Cylinder] Cylinder014005682  label="Válec601"
  Angle = 360
  AttacherType = Attacher::AttachEngine3D
  Height = 50
  Placement = pos=(9.9,-9.9,0) rot=(0,0,1;0rad)
  Radius = 1.6
FEATURE [Part::Cylinder] Cylinder014005683  label="dira stred003"
  Angle = 360
  AttacherType = Attacher::AttachEngine3D
  Height = 50
  Radius = 11
FEATURE [Part::MultiFuse] Fusion001055  label="diry014"
  Shapes = -> [Cylinder014005680,Cylinder014005679,Cylinder014005683,Cylinder014005681,Cylinder014005682]
FEATURE [Part::Chamfer] Chamfer008011
  Base = -> Box145
  Edges = 2 edges r=5: [Edge1,Edge5]
FEATURE [Part::Cut] Cut061098048  label="Horni ucjyt002"
  Base = -> Chamfer008011
  Placement = pos=(0,0,40.5) rot=(0,0,1;0rad)
  Tool = -> Fusion001055
FEATURE [Part::Cylinder] Cylinder  label="Válec"
  Angle = 360
  AttacherType = Attacher::AttachEngine3D
  Height = 10
  Placement = pos=(0,0,40.5) rot=(0,0,1;0rad)
  Radius = 33
FEATURE [Part::Cylinder] Cylinder014005684  label="Válec602"
  Angle = 360
  AttacherType = Attacher::AttachEngine3D
  Height = 10
  Placement = pos=(0,0,40.5) rot=(0,0,1;0rad)
  Radius = 20
FEATURE [Part::Cut] Cut061098049
  Base = -> Cylinder
  Tool = -> Cylinder014005684
FEATURE [Part::Cut] Cut061098050  label="RA Motor Holder"
  Base = -> Cut061098048
  Tool = -> Cut061098049
FEATURE [Part::Cylinder] Cylinder014005685  label="Válec603"
  Angle = 360
  AttacherType = Attacher::AttachEngine3D
  Height = 10
  Placement = pos=(0,0,40.5) rot=(0,0,1;0rad)
  Radius = 20
FEATURE [Part::MultiFuse] Fusion001056
  Shapes = -> [Cut061098046,Chamfer]
FEATURE [Part::MultiFuse] Fusion001057
  Shapes = -> [Cylinder014005685,Cylinder014005671]
FEATURE [Part::Cut] Cut061098052  label="RA Base"
  Base = -> Fusion001056
  Tool = -> Fusion001057
FEATURE [Part::Feature] Chamfer008013  label="Zaklad008"
  shape: bbox 61 x 63.5 x 101.5 mm, 101 faces (baked)
FEATURE [Part::Box] Box146  label="Krychle123"
  AttacherType = Attacher::AttachEngine3D
  Height = 49
  Length = 43
  Placement = pos=(-21.5,-20.5,1) rot=(0,0,1;0rad)
  Width = 42
FEATURE [Part::Chamfer] Chamfer008012
  Base = -> Box146
  Edges = 2 edges r=5: [Edge1,Edge5]
FEATURE [Part::Cylinder] Cylinder014005686  label="Válec604"
  Angle = 360
  AttacherType = Attacher::AttachEngine3D
  Height = 40
  Placement = pos=(-40,1,-17.5) rot=(0,1,0;1.5708rad)
  Radius = 1.2
FEATURE [Part::Cylinder] Cylinder014005687  label="Válec605"
  Angle = 360
  AttacherType = Attacher::AttachEngine3D
  Height = 59
  Placement = pos=(0,0,-18) rot=(0,0,1;0rad)
  Radius = 18.5
FEATURE [Part::Box] Box147  label="Krychle124"
  AttacherType = Attacher::AttachEngine3D
  Height = 13
  Length = 2
  Placement = pos=(29,-4.5,-55) rot=(0,0,1;0rad)
  Width = 28
FEATURE [Part::Cylinder] Cylinder014005688  label="Válec606"
  Angle = 360
  AttacherType = Attacher::AttachEngine3D
  Height = 74
  Placement = pos=(-40,19,-46.5) rot=(0,1,0;1.5708rad)
  Radius = 1.2
FEATURE [Part::Box] Box148  label="Krychle125"
  AttacherType = Attacher::AttachEngine3D
  Height = 13
  Length = 2
  Placement = pos=(-31,-4.5,-55) rot=(0,0,1;0rad)
  Width = 28
FEATURE [Part::MultiFuse] Fusion001059
  Shapes = -> [Box147,Box148]
FEATURE [Part::Cylinder] Cylinder014005689  label="Válec607"
  Angle = 360
  AttacherType = Attacher::AttachEngine3D
  Height = 74
  Placement = pos=(-40,0,-46.5) rot=(0,1,0;1.5708rad)
  Radius = 1.2
FEATURE [Part::MultiFuse] Fusion001062
  Shapes = -> [Cylinder014005689,Cylinder014005688]
FEATURE [Part::MultiFuse] Fusion001058
  Shapes = -> [Fusion001059,Fusion001062]
FEATURE [Part::Cut] Cut061098055  label="Zaklad 003"
  Base = -> Chamfer008013
  Tool = -> Fusion001058
FEATURE [Part::Cylinder] Cylinder014005690  label="Válec608"
  Angle = 360
  AttacherType = Attacher::AttachEngine3D
  Height = 40
  Placement = pos=(-40,16,-17.5) rot=(0,1,0;1.5708rad)
  Radius = 1.2
FEATURE [Part::MultiFuse] Fusion001060
  Shapes = -> [Cylinder014005686,Cylinder014005690]
FEATURE [Part::Cut] Cut061098054  label="RA Zaklad003"
  Base = -> Cut061098055
  Tool = -> Fusion001060
FEATURE [Part::MultiFuse] Fusion001063
  Shapes = -> [Cut061098054,Chamfer008012]
FEATURE [Part::Cylinder] Cylinder014005691  label="Válec609"
  Angle = 360
  AttacherType = Attacher::AttachEngine3D
  Height = 10
  Placement = pos=(0,0,40.5) rot=(0,0,1;0rad)
  Radius = 20
FEATURE [Part::MultiFuse] Fusion001061
  Shapes = -> [Cylinder014005691,Cylinder014005687]
FEATURE [Part::Cut] Cut061098053  label="DEC Base"
  Base = -> Fusion001063
  Tool = -> Fusion001061
FEATURE [Part::Cylinder] Cylinder014005692  label="Válec610"
  Angle = 360
  AttacherType = Attacher::AttachEngine3D
  Height = 10
  Placement = pos=(0,0,40.5) rot=(0,0,1;0rad)
  Radius = 33
FEATURE [Part::Cylinder] Cylinder014005693  label="Válec611"
  Angle = 360
  AttacherType = Attacher::AttachEngine3D
  Height = 10
  Placement = pos=(0,0,40.5) rot=(0,0,1;0rad)
  Radius = 20
FEATURE [Part::Cut] Cut061098057
  Base = -> Cylinder014005692
  Tool = -> Cylinder014005693
FEATURE [Part::Box] Box149  label="Krychle126"
  AttacherType = Attacher::AttachEngine3D
  Height = 10
  Length = 43
  Placement = pos=(-21.5,-20.5,0) rot=(0,0,1;0rad)
  Width = 42
FEATURE [Part::Chamfer] Chamfer008014
  Base = -> Box149
  Edges = 2 edges r=5: [Edge1,Edge5]
FEATURE [Part::Cylinder] Cylinder014005694  label="Válec612"
  Angle = 360
  AttacherType = Attacher::AttachEngine3D
  Height = 50
  Placement = pos=(-9.9,9.9,0) rot=(0,0,1;0rad)
  Radius = 1.6
FEATURE [Part::Cylinder] Cylinder014005695  label="Válec613"
  Angle = 360
  AttacherType = Attacher::AttachEngine3D
  Height = 50
  Placement = pos=(-9.9,-9.9,0) rot=(0,0,1;0rad)
  Radius = 1.6
FEATURE [Part::Cylinder] Cylinder014005696  label="Válec614"
  Angle = 360
  AttacherType = Attacher::AttachEngine3D
  Height = 50
  Placement = pos=(9.9,-9.9,0) rot=(0,0,1;0rad)
  Radius = 1.6
FEATURE [Part::Cylinder] Cylinder014005697  label="dira stred004"
  Angle = 360
  AttacherType = Attacher::AttachEngine3D
  Height = 50
  Radius = 11
FEATURE [Part::Cylinder] Cylinder014005698  label="Válec615"
  Angle = 360
  AttacherType = Attacher::AttachEngine3D
  Height = 50
  Placement = pos=(9.9,9.9,0) rot=(0,0,1;0rad)
  Radius = 1.6
FEATURE [Part::MultiFuse] Fusion001064  label="diry015"
  Shapes = -> [Cylinder014005694,Cylinder014005698,Cylinder014005697,Cylinder014005695,Cylinder014005696]
FEATURE [Part::Cut] Cut061098056  label="Horni ucjyt003"
  Base = -> Chamfer008014
  Placement = pos=(0,0,40.5) rot=(0,0,1;0rad)
  Tool = -> Fusion001064
FEATURE [Part::Cut] Cut061098058  label="DEC Motor Holder"
  Base = -> Cut061098056
  Tool = -> Cut061098057
FEATURE [Part::Box] Box154  label="Krychle131"
  AttacherType = Attacher::AttachEngine3D
  Height = 4
  Length = 10
  Placement = pos=(-5,-8,-55) rot=(0,0,1;0rad)
  Width = 5
FEATURE [Part::Cylinder] Cylinder014005701  label="Válec618"
  Angle = 360
  AttacherType = Attacher::AttachEngine3D
  Height = 70
  Placement = pos=(-5,6,16.5) rot=(0,1,0;1.5708rad)
  Radius = 1
FEATURE [Part::Box] Box155  label="Krychle132"
  AttacherType = Attacher::AttachEngine3D
  Height = 2
  Length = 62
  Placement = pos=(-2.5,-2,23) rot=(0,0,1;0rad)
  Width = 31
FEATURE [Part::Cylinder] Cylinder014005702  label="Válec619"
  Angle = 360
  AttacherType = Attacher::AttachEngine3D
  Height = 70
  Placement = pos=(-5,20,16.5) rot=(0,1,0;1.5708rad)
  Radius = 1
FEATURE [Part::MultiFuse] Fusion001070  label="Horni diry008"
  Placement = pos=(0,0,3) rot=(0,0,1;0rad)
  Shapes = -> [Cylinder014005702,Cylinder014005701]
FEATURE [Part::Box] Box156  label="Krychle133"
  AttacherType = Attacher::AttachEngine3D
  Height = 8
  Length = 54
  Placement = pos=(1.5,0,15) rot=(0,0,1;0rad)
  Width = 29
FEATURE [Part::MultiFuse] Fusion001069
  Shapes = -> [Fusion001070,Box156]
FEATURE [Part::Box] Box157  label="Krychle134"
  AttacherType = Attacher::AttachEngine3D
  Height = 8
  Length = 58
  Placement = pos=(-0.5,0,15) rot=(0,0,1;0rad)
  Width = 29
FEATURE [Part::MultiFuse] Fusion001068
  Shapes = -> [Box155,Box157]
FEATURE [Part::Cut] Cut061098063
  Base = -> Fusion001068
  Tool = -> Fusion001069
FEATURE [Part::Part2DObjectPython] ShapeString012  # Draft 2D object (typed FeaturePython)
  FontFile = <path>
  Placement = pos=(15.3452,-2,30.5072) rot=(1,0,0;1.5708rad)
  Size = 10
  String = OnStep
  Tracking = 0
FEATURE [Part::Extrusion] Extrude070  label="OnStep004"
  Base = -> ShapeString012
  Dir = (0,-1,0)
  DirMode = 2
  FaceMakerClass = Part::FaceMakerBullseye
  LengthFwd = 1
  LengthRev = 0
  Placement = pos=(-10,-22,22) rot=(-1,0,0;1.5708rad)
  Solid = false
  Symmetric = false
FEATURE [Part::Cut] Cut061098064  label="viko s texty004"
  Base = -> Cut061098063
  Tool = -> Extrude070
FEATURE [Part::Chamfer] Chamfer008016
  Base = -> Cut061098064
  Edges = 2 edges r=2.5: [Edge355,Edge357]
FEATURE [Part::Fillet] Fillet008  label="DEC vicko002"
  Base = -> Chamfer008016
  Edges = 3 edges r=1: [Edge36,Edge38,Edge39]
  Placement = pos=(-28.5,19,-80) rot=(1,0,0;1.5708rad)
FEATURE [Part::Cut] Cut061098062  label="RA PCB Cap"
  Base = -> Fillet008
  Tool = -> Box154
FEATURE [Part::Box] Box158  label="Krychle135"
  AttacherType = Attacher::AttachEngine3D
  Height = 4
  Length = 10
  Placement = pos=(-5,-8,-55) rot=(0,0,1;0rad)
  Width = 5
FEATURE [Part::Cylinder] Cylinder014005703  label="Válec620"
  Angle = 360
  AttacherType = Attacher::AttachEngine3D
  Height = 70
  Placement = pos=(-5,6,16.5) rot=(0,1,0;1.5708rad)
  Radius = 1
FEATURE [Part::Box] Box159  label="Krychle136"
  AttacherType = Attacher::AttachEngine3D
  Height = 2
  Length = 62
  Placement = pos=(-2.5,-2,23) rot=(0,0,1;0rad)
  Width = 31
FEATURE [Part::Cylinder] Cylinder014005704  label="Válec621"
  Angle = 360
  AttacherType = Attacher::AttachEngine3D
  Height = 70
  Placement = pos=(-5,20,16.5) rot=(0,1,0;1.5708rad)
  Radius = 1
FEATURE [Part::MultiFuse] Fusion001073  label="Horni diry009"
  Placement = pos=(0,0,3) rot=(0,0,1;0rad)
  Shapes = -> [Cylinder014005704,Cylinder014005703]
FEATURE [Part::Box] Box160  label="Krychle137"
  AttacherType = Attacher::AttachEngine3D
  Height = 8
  Length = 54
  Placement = pos=(1.5,0,15) rot=(0,0,1;0rad)
  Width = 29
FEATURE [Part::MultiFuse] Fusion001072
  Shapes = -> [Fusion001073,Box160]
FEATURE [Part::Box] Box161  label="Krychle138"
  AttacherType = Attacher::AttachEngine3D
  Height = 8
  Length = 58
  Placement = pos=(-0.5,0,15) rot=(0,0,1;0rad)
  Width = 29
FEATURE [Part::MultiFuse] Fusion001071
  Shapes = -> [Box159,Box161]
FEATURE [Part::Cut] Cut061098066
  Base = -> Fusion001071
  Tool = -> Fusion001072
FEATURE [Part::Part2DObjectPython] ShapeString013  # Draft 2D object (typed FeaturePython)
  FontFile = <path>
  Placement = pos=(15.3452,-2,30.5072) rot=(1,0,0;1.5708rad)
  Size = 10
  String = OnStep
  Tracking = 0
FEATURE [Part::Extrusion] Extrude071  label="OnStep005"
  Base = -> ShapeString013
  Dir = (0,-1,0)
  DirMode = 2
  FaceMakerClass = Part::FaceMakerBullseye
  LengthFwd = 1
  LengthRev = 0
  Placement = pos=(-10,-22,22) rot=(-1,0,0;1.5708rad)
  Solid = false
  Symmetric = false
FEATURE [Part::Cut] Cut061098067  label="viko s texty005"
  Base = -> Cut061098066
  Tool = -> Extrude071
FEATURE [Part::Chamfer] Chamfer008017
  Base = -> Cut061098067
  Edges = 2 edges r=2.5: [Edge355,Edge357]
FEATURE [Part::Fillet] Fillet009  label="DEC vicko003"
  Base = -> Chamfer008017
  Edges = 3 edges r=1: [Edge36,Edge38,Edge39]
  Placement = pos=(-28.5,19,-80) rot=(1,0,0;1.5708rad)
FEATURE [Part::Cut] Cut061098065  label="DEC PCB Cap"
  Base = -> Fillet009
  Tool = -> Box158
FEATURE [Part::Cylinder] Cylinder014005740  label="Válec655"
  Angle = 360
  AttacherType = Attacher::AttachEngine3D
  Height = 7
  Placement = pos=(-40,1,-17.5) rot=(0,1,0;1.5708rad)
  Radius = 2.4
FEATURE [Part::Cylinder] Cylinder014005741  label="Válec656"
  Angle = 360
  AttacherType = Attacher::AttachEngine3D
  Height = 7
  Placement = pos=(-40,16,-17.5) rot=(0,1,0;1.5708rad)
  Radius = 2.4
FEATURE [Part::MultiFuse] Fusion
  Shapes = -> [Cylinder014005740,Cylinder014005741,Cylinder014005376,Cylinder014005377]
FEATURE [Part::Cut] Cut  label="RA Polar Finder Clamp"
  Base = -> Cut001001
  Tool = -> Fusion
FEATURE [Part::FeaturePython] Nut029  label="M5-Nut"  # Fasteners workbench fastener (typed FeaturePython)
  Placement = pos=(22,17,69) rot=(0,1,0;1.5708rad)
  diameter = 7
  invert = false
  matchOuter = false
  offset = 0
  thread = false
  type = 1
FEATURE [Part::FeaturePython] Nut030  label="M5-Nut001"  # Fasteners workbench fastener (typed FeaturePython)
  Placement = pos=(22,-17,69) rot=(0,1,0;1.5708rad)
  diameter = 7
  invert = false
  matchOuter = false
  offset = 0
  thread = false
  type = 1
FEATURE [Sketcher::SketchObject] Sketch046
  MapMode = 45
  Placement = pos=(44.88,21.011,5.40003) rot=(0.707106,0.001666,0.707106;3.13826rad)
  sketch-geometry (7):
    g0: LineSegment StartX=5.21891 StartY=0.0364138 StartZ=0 EndX=2.62121 EndY=4.46293 EndZ=0
    g1: LineSegment StartX=2.62121 StartY=4.46293 StartZ=0 EndX=-2.51111 EndY=4.42651 EndZ=0
    g2: LineSegment StartX=-2.51111 StartY=4.42651 StartZ=0 EndX=-5.04574 EndY=-0.0364138 EndZ=0
    g3: LineSegment StartX=-5.04574 StartY=-0.0364138 StartZ=0 EndX=-2.44804 EndY=-4.46293 EndZ=0
    g4: LineSegment StartX=-2.44804 StartY=-4.46293 StartZ=0 EndX=2.68428 EndY=-4.42651 EndZ=0
    g5: LineSegment StartX=2.68428 StartY=-4.42651 StartZ=0 EndX=5.21891 EndY=0.0364138 EndZ=0
    g6: Circle [constr] CenterX=0.0865834 CenterY=0 CenterZ=0 NormalX=0 NormalY=0 NormalZ=1 AngleXU=0 Radius=5.13245
  constraints (14):
    c: Coincident(g0,g1)
    c: Coincident(g1,g2)
    c: Coincident(g2,g3)
    c: Coincident(g3,g4)
    c: Coincident(g4,g5)
    c: Coincident(g5,g0)
    c: Equal(g0, g1-g5) x5
    c: PointOnObject(g0,g6)
    c: PointOnObject(g1,g6)
    c: PointOnObject(g2,g6)
    c: PointOnObject(g3,g6)
    c: PointOnObject(g4,g6)
    c: PointOnObject(g5,g6)
    c: PointOnObject(g6,g-1)
FEATURE [Sketcher::SketchObject] Sketch047
  MapMode = 5
  Placement = pos=(0,0,60) rot=(0,0,1;0rad)
  sketch-geometry (6):
    g0: LineSegment StartX=-18.9734 StartY=34.0308 StartZ=0 EndX=-16.0253 EndY=36.9748 EndZ=0
    g1: LineSegment StartX=18.996 StartY=34.0308 StartZ=0 EndX=16.044 EndY=36.9748 EndZ=0
    g2: LineSegment StartX=18.996 StartY=34.0308 StartZ=0 EndX=-18.9734 EndY=34.0308 EndZ=0
    g3: LineSegment StartX=-18.9734 StartY=40.0311 StartZ=0 EndX=-16.0253 EndY=36.9748 EndZ=0
    g4: LineSegment StartX=16.044 StartY=36.9748 StartZ=0 EndX=18.9109 EndY=40.0311 EndZ=0
    g5: LineSegment StartX=-18.9734 StartY=40.0311 StartZ=0 EndX=18.9109 EndY=40.0311 EndZ=0
  constraints (7):
    c: Coincident(g2,g1)
    c: Coincident(g2,g0)
    c: Horizontal(g2)
    c: Coincident(g3,g0)
    c: Coincident(g5,g3)
    c: Coincident(g5,g4)
    c: Horizontal(g5)
FEATURE [Part::Feature] Cylinder014005742  label="Válec657"
  Placement = pos=(0,0,0) rot=(0,0,1;2.0944rad)
  shape: bbox 5 x 5 x 7 mm, 3 faces (baked)
FEATURE [Part::Feature] Cylinder014005743  label="Válec658"
  shape: bbox 5 x 5 x 7 mm, 3 faces (baked)
FEATURE [Part::Feature] Fusion001089022  label="Pojistka011"
  Placement = pos=(0,0,0) rot=(0,0,1;2.0944rad)
  shape: bbox 9.944 x 13.82 x 16.54 mm, 27 faces (baked)
FEATURE [Part::Feature] Fusion001089023  label="Pojistka012"
  Placement = pos=(0,0,0) rot=(0,0,-1;2.05949rad)
  shape: bbox 9.575 x 13.96 x 16.54 mm, 27 faces (baked)
FEATURE [Part::Feature] Cylinder014005744  label="Válec659"
  Placement = pos=(0,0,0) rot=(0,0,1;4.18879rad)
  shape: bbox 5 x 5 x 7 mm, 3 faces (baked)
FEATURE [Part::Feature] union001_solid007  label="union001 (Solid)007"
  Placement = pos=(15,-7,-4) rot=(-1,0,0;1.5708rad)
  shape: bbox 10 x 5.7 x 11.54 mm, 33 faces (baked)
FEATURE [Part::Feature] Screw_solid099  label="M2x4-Screw (Solid)099"
  Placement = pos=(0,0,0) rot=(0,0,1;3.14159rad)
  shape: bbox 3.6 x 3.6 x 4 mm, 12 faces (baked)
FEATURE [Part::Feature] Screw_solid100  label="M2x4-Screw (Solid)100"
  Placement = pos=(0,0,0) rot=(0,0,-1;1.0472rad)
  shape: bbox 3.6 x 3.6 x 4 mm, 12 faces (baked)
FEATURE [Part::Feature] Screw_solid101  label="M2x4-Screw (Solid)101"
  Placement = pos=(0,0,0) rot=(0,0,1;1.0472rad)
  shape: bbox 3.6 x 3.6 x 4 mm, 12 faces (baked)
FEATURE [Part::MultiFuse] Fusion001089024  label="srouby034"
  Placement = pos=(0,0,0.5) rot=(0,0,1;0rad)
  Shapes = -> [Screw_solid101,Screw_solid100,Screw_solid099]
FEATURE [Part::MultiFuse] Fusion001089030
  Shapes = -> [Cylinder014005744,Cylinder014005743,Cylinder014005742]
FEATURE [Part::Cylinder] Cylinder014005745  label="Válec660"
  Angle = 360
  AttacherType = Attacher::AttachEngine3D
  Height = 2.5
  Placement = pos=(0,-12,71) rot=(0,0,1;0rad)
  Radius = 6
FEATURE [Part::Cylinder] Cylinder014005746  label="Válec661"
  Angle = 360
  AttacherType = Attacher::AttachEngine3D
  Height = 6
  Placement = pos=(0,0,7) rot=(0,0,1;0rad)
  Radius = 6.5
FEATURE [Part::Cylinder] Cylinder014005747  label="Válec662"
  Angle = 360
  AttacherType = Attacher::AttachEngine3D
  Height = 7
  Radius = 2.6
FEATURE [Part::MultiFuse] Fusion001089026
  Placement = pos=(0,0,1) rot=(0,0,1;0rad)
  Shapes = -> [Fusion001089030,Cylinder014005747]
FEATURE [Part::Box] Box179  label="Krychle156"
  AttacherType = Attacher::AttachEngine3D
  Height = 112
  Length = 38
  Placement = pos=(-19,32,-52) rot=(0,0,1;0rad)
  Width = 10
FEATURE [Part::Box] Box180  label="Krychle157"
  AttacherType = Attacher::AttachEngine3D
  Height = 112
  Length = 38
  Placement = pos=(-19,34,-52) rot=(0,0,1;0rad)
  Width = 6
FEATURE [Part::Cut] Cut061098092
  Base = -> Box179
  Tool = -> Box180
FEATURE [Part::Cylinder] Cylinder014005748  label="Válec663"
  Angle = 360
  AttacherType = Attacher::AttachEngine3D
  Height = 2.5
  Placement = pos=(0,-12,71) rot=(0,0,1;0rad)
  Radius = 6
FEATURE [Part::Cylinder] Cylinder014005749  label="Válec664"
  Angle = 360
  AttacherType = Attacher::AttachEngine3D
  Height = 8
  Placement = pos=(0,0,66) rot=(0,0,1;0rad)
  Radius = 4.5
FEATURE [Part::Box] Box181  label="Krychle158"
  AttacherType = Attacher::AttachEngine3D
  Height = 15
  Length = 50
  Placement = pos=(-25,-25,64) rot=(0,0,1;0rad)
  Width = 50
FEATURE [Part::Box] Box182  label="Krychle159"
  AttacherType = Attacher::AttachEngine3D
  Height = 15
  Length = 2
  Placement = pos=(-15.5,-26,61) rot=(0,0,1;0rad)
  Width = 52
FEATURE [Part::Cylinder] Cylinder014005750  label="Válec665"
  Angle = 360
  AttacherType = Attacher::AttachEngine3D
  Height = 60
  Placement = pos=(-30,-17,69) rot=(0,1,0;1.5708rad)
  Radius = 2.65
FEATURE [Part::Cylinder] Cylinder014005751  label="Válec666"
  Angle = 360
  AttacherType = Attacher::AttachEngine3D
  Height = 55
  Placement = pos=(0,0,35) rot=(0,0,1;0rad)
  Radius = 2.7
FEATURE [Part::Cylinder] Cylinder014005752  label="Válec667"
  Angle = 360
  AttacherType = Attacher::AttachEngine3D
  Height = 25
  Placement = pos=(0,0,43) rot=(0,0,1;0rad)
  Radius = 10.5
FEATURE [Part::Cylinder] Cylinder014005753  label="Válec668"
  Angle = 360
  AttacherType = Attacher::AttachEngine3D
  Height = 22
  Radius = 2.6
FEATURE [Part::Box] Box183  label="Krychle160"
  AttacherType = Attacher::AttachEngine3D
  Height = 2.5
  Length = 12
  Placement = pos=(-6,-25,71) rot=(0,0,1;0rad)
  Width = 13
FEATURE [Part::MultiFuse] Fusion001089029
  Placement = pos=(0,0,1) rot=(0,0,1;0rad)
  Shapes = -> [Box183,Cylinder014005745]
FEATURE [Part::Cylinder] Cylinder014005754  label="Válec669"
  Angle = 360
  AttacherType = Attacher::AttachEngine3D
  Height = 60
  Placement = pos=(-30,17,69) rot=(0,1,0;1.5708rad)
  Radius = 2.65
FEATURE [Part::MultiFuse] Fusion001089027
  Shapes = -> [Cylinder014005754,Cylinder014005750,Nut029,Nut030]
FEATURE [Part::Cylinder] Cylinder014005755  label="Unasec vrch021"
  Angle = 360
  AttacherType = Attacher::AttachEngine3D
  Height = 1.5
  Placement = pos=(0,0,5.5) rot=(0,0,1;0rad)
  Radius = 15.5
FEATURE [Part::Cut] Cut061098095  label="unasec vrch021"
  Base = -> Cylinder014005755
  Tool = -> Fusion001089024
FEATURE [Part::Cut] Cut061098098  label="Unasec Vrch zaklad021"
  Base = -> Cut061098095
  Tool = -> Fusion001089026
FEATURE [Part::Box] Box184  label="Krychle161"
  AttacherType = Attacher::AttachEngine3D
  Height = 17
  Length = 5
  Placement = pos=(3.3,-3.6,44.5) rot=(0,0,1;0rad)
  Width = 7.2
FEATURE [Part::Cylinder] Cylinder014005756  label="Válec670"
  Angle = 360
  AttacherType = Attacher::AttachEngine3D
  Height = 9
  Placement = pos=(0,0,55) rot=(0,0,1;0rad)
  Radius = 12.5
FEATURE [Part::Box] Box185  label="Krychle162"
  AttacherType = Attacher::AttachEngine3D
  Height = 12
  Length = 2.5
  Placement = pos=(18.5,-3,-3) rot=(0,0,1;0rad)
  Width = 6
FEATURE [Part::Cylinder] Cylinder014005757  label="Válec671"
  Angle = 360
  AttacherType = Attacher::AttachEngine3D
  Height = 14
  Placement = pos=(12,0,-4) rot=(0,1,0;1.5708rad)
  Radius = 1.7
FEATURE [Part::MultiFuse] Fusion001089032  label="Pojistka013"
  Placement = pos=(-11,0,61.5) rot=(0,0,1;0rad)
  Shapes = -> [Box185,union001_solid007,Cylinder014005757]
FEATURE [Part::MultiFuse] Fusion001089036
  Shapes = -> [Fusion001089032,Fusion001089022,Fusion001089023]
FEATURE [Part::Cylinder] Cylinder014005758  label="Válec672"
  Angle = 360
  AttacherType = Attacher::AttachEngine3D
  Height = 25
  Placement = pos=(0,0,43) rot=(0,0,1;0rad)
  Radius = 4.2
FEATURE [Part::Box] Box186  label="Krychle163"
  AttacherType = Attacher::AttachEngine3D
  Height = 2.5
  Length = 12
  Placement = pos=(-6,-25,71) rot=(0,0,1;0rad)
  Width = 13
FEATURE [Part::MultiFuse] Fusion001089037
  Placement = pos=(0,0,1) rot=(0,0,1;3.14159rad)
  Shapes = -> [Box186,Cylinder014005748]
FEATURE [Part::MultiFuse] Fusion001089034
  Shapes = -> [Fusion001089029,Fusion001089037]
FEATURE [Part::Extrusion] Extrude079
  Base = -> Sketch047
  Dir = (0,0,1)
  DirMode = 2
  FaceMakerClass = Part::FaceMakerBullseye
  LengthFwd = -112
  LengthRev = 0
  Solid = true
  Symmetric = false
FEATURE [Part::MultiFuse] Fusion001089025  label="Arca plate base016"
  Placement = pos=(0,-6.5,115.5) rot=(-1,0,0;1.5708rad)
  Shapes = -> [Extrude079,Cut061098092]
FEATURE [Part::Cut] Cut061098093  label="Arca sw 011"
  Base = -> Box181
  Tool = -> Fusion001089025
FEATURE [Part::Cut] Cut061098090
  Base = -> Cut061098093
  Tool = -> Box182
FEATURE [Part::MultiFuse] Fusion001089028
  Shapes = -> [Cylinder014005756,Cut061098090]
FEATURE [Part::RegularPolygon] RegularPolygon008  label="Pravidelný n-úhelník008"
  AttacherType = Attacher::AttachEngine3D
  Circumradius = 6
  Polygon = 6
FEATURE [Part::Extrusion] Extrude078
  Base = -> RegularPolygon008
  Dir = (0,0,1)
  DirMode = 2
  FaceMakerClass = Part::FaceMakerBullseye
  LengthFwd = 8
  LengthRev = 0
  Placement = pos=(0,0,13) rot=(0,0,1;0rad)
  Solid = true
  Symmetric = false
FEATURE [Part::MultiFuse] Fusion001089035
  Shapes = -> [Cut061098098,Cylinder014005746,Extrude078]
FEATURE [Part::Extrusion] Extrude080
  Base = -> Sketch046
  Dir = (1,0,0)
  DirMode = 2
  FaceMakerClass = Part::FaceMakerBullseye
  LengthFwd = 5
  LengthRev = 0
  Placement = pos=(0,0,0.25) rot=(0,0,1;0rad)
  Solid = true
  Symmetric = false
FEATURE [Part::MultiFuse] Fusion001089038
  Shapes = -> [Cylinder014005753,Extrude080]
FEATURE [Part::Cut] Cut061098097  label="unasec top008"
  Base = -> Fusion001089035
  Placement = pos=(0,0,42) rot=(0,0,1;0rad)
  Tool = -> Fusion001089038
FEATURE [Part::MultiFuse] Fusion001089031
  Shapes = -> [Cylinder014005751,Cut061098097,Cylinder014005749]
FEATURE [Part::Cut] Cut061098091
  Base = -> Fusion001089028
  Tool = -> Fusion001089031
FEATURE [Part::Cut] Cut061098099
  Base = -> Cut061098091
  Tool = -> Fusion001089027
FEATURE [Part::Cut] Cut061098094  label="Swis Arca006"
  Base = -> Cut061098099
  Placement = pos=(0,0,-3) rot=(0,0,1;0rad)
  Tool = -> Fusion001089034
FEATURE [Part::MultiFuse] Fusion001089033
  Shapes = -> [Cut061098094,Cylinder014005752]
FEATURE [Part::Cut] Cut061098096
  Base = -> Fusion001089033
  Tool = -> Cylinder014005758
FEATURE [Part::MultiFuse] Fusion001089039
  Shapes = -> [Cut061098096,Box184]
FEATURE [Part::Cut] Cut061098100  label="RA Clamp001"
  Base = -> Fusion001089039
  Tool = -> Fusion001089036
FEATURE [Part::Cylinder] Cylinder014005759  label="Válec673"
  Angle = 360
  AttacherType = Attacher::AttachEngine3D
  Height = 11
  Placement = pos=(0,0,38) rot=(0,0,1;0rad)
  Radius = 11
FEATURE [Part::Cut] Cut061098101  label="RA Clamp"
  Base = -> Cut061098100
  Tool = -> Cylinder014005759
FEATURE [Part::Feature] Screw_solid102  label="M2x4-Screw (Solid)102"
  Placement = pos=(0,0,0) rot=(0,0,-1;1.0472rad)
  shape: bbox 3.6 x 3.6 x 4 mm, 12 faces (baked)
FEATURE [Part::Feature] Screw_solid103  label="M2x4-Screw (Solid)103"
  Placement = pos=(0,0,0) rot=(0,0,1;3.14159rad)
  shape: bbox 3.6 x 3.6 x 4 mm, 12 faces (baked)
FEATURE [Part::Feature] Screw_solid104  label="M2x4-Screw (Solid)104"
  Placement = pos=(0,0,0) rot=(0,0,1;1.0472rad)
  shape: bbox 3.6 x 3.6 x 4 mm, 12 faces (baked)
FEATURE [Sketcher::SketchObject] Sketch048
  MapMode = 5
  Placement = pos=(0,0,60) rot=(0,0,1;0rad)
  sketch-geometry (6):
    g0: LineSegment StartX=-18.9734 StartY=34.0308 StartZ=0 EndX=-16.0253 EndY=36.9748 EndZ=0
    g1: LineSegment StartX=18.996 StartY=34.0308 StartZ=0 EndX=16.044 EndY=36.9748 EndZ=0
    g2: LineSegment StartX=18.996 StartY=34.0308 StartZ=0 EndX=-18.9734 EndY=34.0308 EndZ=0
    g3: LineSegment StartX=-18.9734 StartY=40.0311 StartZ=0 EndX=-16.0253 EndY=36.9748 EndZ=0
    g4: LineSegment StartX=16.044 StartY=36.9748 StartZ=0 EndX=18.9109 EndY=40.0311 EndZ=0
    g5: LineSegment StartX=-18.9734 StartY=40.0311 StartZ=0 EndX=18.9109 EndY=40.0311 EndZ=0
  constraints (7):
    c: Coincident(g2,g1)
    c: Coincident(g2,g0)
    c: Horizontal(g2)
    c: Coincident(g3,g0)
    c: Coincident(g5,g3)
    c: Coincident(g5,g4)
    c: Horizontal(g5)
FEATURE [Sketcher::SketchObject] Sketch049
  MapMode = 45
  Placement = pos=(44.88,21.011,5.40003) rot=(0.707106,0.001666,0.707106;3.13826rad)
  sketch-geometry (7):
    g0: LineSegment StartX=5.21891 StartY=0.0364138 StartZ=0 EndX=2.62121 EndY=4.46293 EndZ=0
    g1: LineSegment StartX=2.62121 StartY=4.46293 StartZ=0 EndX=-2.51111 EndY=4.42651 EndZ=0
    g2: LineSegment StartX=-2.51111 StartY=4.42651 StartZ=0 EndX=-5.04574 EndY=-0.0364138 EndZ=0
    g3: LineSegment StartX=-5.04574 StartY=-0.0364138 StartZ=0 EndX=-2.44804 EndY=-4.46293 EndZ=0
    g4: LineSegment StartX=-2.44804 StartY=-4.46293 StartZ=0 EndX=2.68428 EndY=-4.42651 EndZ=0
    g5: LineSegment StartX=2.68428 StartY=-4.42651 StartZ=0 EndX=5.21891 EndY=0.0364138 EndZ=0
    g6: Circle [constr] CenterX=0.0865834 CenterY=0 CenterZ=0 NormalX=0 NormalY=0 NormalZ=1 AngleXU=0 Radius=5.13245
  constraints (14):
    c: Coincident(g0,g1)
    c: Coincident(g1,g2)
    c: Coincident(g2,g3)
    c: Coincident(g3,g4)
    c: Coincident(g4,g5)
    c: Coincident(g5,g0)
    c: Equal(g0, g1-g5) x5
    c: PointOnObject(g0,g6)
    c: PointOnObject(g1,g6)
    c: PointOnObject(g2,g6)
    c: PointOnObject(g3,g6)
    c: PointOnObject(g4,g6)
    c: PointOnObject(g5,g6)
    c: PointOnObject(g6,g-1)
FEATURE [Part::Cylinder] Cylinder014005760  label="Válec674"
  Angle = 360
  AttacherType = Attacher::AttachEngine3D
  Height = 6
  Placement = pos=(0,0,7) rot=(0,0,1;0rad)
  Radius = 6.5
FEATURE [Part::Cylinder] Cylinder014005761  label="Válec675"
  Angle = 360
  AttacherType = Attacher::AttachEngine3D
  Height = 2.5
  Placement = pos=(0,-12,71) rot=(0,0,1;0rad)
  Radius = 6
FEATURE [Part::Cylinder] Cylinder014005762  label="Válec676"
  Angle = 360
  AttacherType = Attacher::AttachEngine3D
  Height = 7
  Radius = 2.6
FEATURE [Part::Box] Box187  label="Krychle164"
  AttacherType = Attacher::AttachEngine3D
  Height = 112
  Length = 38
  Placement = pos=(-19,32,-52) rot=(0,0,1;0rad)
  Width = 10
FEATURE [Part::Cylinder] Cylinder014005763  label="Válec677"
  Angle = 360
  AttacherType = Attacher::AttachEngine3D
  Height = 2.5
  Placement = pos=(0,-12,71) rot=(0,0,1;0rad)
  Radius = 6
FEATURE [Part::Cylinder] Cylinder014005764  label="Válec678"
  Angle = 360
  AttacherType = Attacher::AttachEngine3D
  Height = 60
  Placement = pos=(-30,-17,69) rot=(0,1,0;1.5708rad)
  Radius = 2.65
FEATURE [Part::Cylinder] Cylinder014005765  label="Válec679"
  Angle = 360
  AttacherType = Attacher::AttachEngine3D
  Height = 22
  Radius = 2.6
FEATURE [Part::Box] Box188  label="Krychle165"
  AttacherType = Attacher::AttachEngine3D
  Height = 112
  Length = 38
  Placement = pos=(-19,34,-52) rot=(0,0,1;0rad)
  Width = 6
FEATURE [Part::Cut] Cut061098109
  Base = -> Box187
  Tool = -> Box188
FEATURE [Part::Cylinder] Cylinder014005766  label="Válec680"
  Angle = 360
  AttacherType = Attacher::AttachEngine3D
  Height = 60
  Placement = pos=(-30,17,69) rot=(0,1,0;1.5708rad)
  Radius = 2.65
FEATURE [Part::Box] Box189  label="Krychle166"
  AttacherType = Attacher::AttachEngine3D
  Height = 15
  Length = 50
  Placement = pos=(-25,-25,64) rot=(0,0,1;0rad)
  Width = 50
FEATURE [Part::Box] Box190  label="Krychle167"
  AttacherType = Attacher::AttachEngine3D
  Height = 15
  Length = 2
  Placement = pos=(-15.5,-26,61) rot=(0,0,1;0rad)
  Width = 52
FEATURE [Part::Cylinder] Cylinder014005767  label="Válec681"
  Angle = 360
  AttacherType = Attacher::AttachEngine3D
  Height = 25
  Placement = pos=(0,0,43) rot=(0,0,1;0rad)
  Radius = 10.5
FEATURE [Part::Cylinder] Cylinder014005768  label="Válec682"
  Angle = 360
  AttacherType = Attacher::AttachEngine3D
  Height = 55
  Placement = pos=(0,0,35) rot=(0,0,1;0rad)
  Radius = 2.7
FEATURE [Part::Box] Box191  label="Krychle168"
  AttacherType = Attacher::AttachEngine3D
  Height = 2.5
  Length = 12
  Placement = pos=(-6,-25,71) rot=(0,0,1;0rad)
  Width = 13
FEATURE [Part::Box] Box192  label="Krychle169"
  AttacherType = Attacher::AttachEngine3D
  Height = 17
  Length = 5
  Placement = pos=(3.3,-3.6,44.5) rot=(0,0,1;0rad)
  Width = 7.2
FEATURE [Part::Cylinder] Cylinder014005769  label="Válec683"
  Angle = 360
  AttacherType = Attacher::AttachEngine3D
  Height = 9
  Placement = pos=(0,0,55) rot=(0,0,1;0rad)
  Radius = 12.5
FEATURE [Part::Box] Box193  label="Krychle170"
  AttacherType = Attacher::AttachEngine3D
  Height = 12
  Length = 2.5
  Placement = pos=(18.5,-3,-3) rot=(0,0,1;0rad)
  Width = 6
FEATURE [Part::Cylinder] Cylinder014005770  label="Unasec vrch022"
  Angle = 360
  AttacherType = Attacher::AttachEngine3D
  Height = 1.5
  Placement = pos=(0,0,5.5) rot=(0,0,1;0rad)
  Radius = 15.5
FEATURE [Part::Cylinder] Cylinder014005771  label="Válec684"
  Angle = 360
  AttacherType = Attacher::AttachEngine3D
  Height = 14
  Placement = pos=(12,0,-4) rot=(0,1,0;1.5708rad)
  Radius = 1.7
FEATURE [Part::Cylinder] Cylinder014005772  label="Válec685"
  Angle = 360
  AttacherType = Attacher::AttachEngine3D
  Height = 25
  Placement = pos=(0,0,43) rot=(0,0,1;0rad)
  Radius = 4.2
FEATURE [Part::Box] Box194  label="Krychle171"
  AttacherType = Attacher::AttachEngine3D
  Height = 2.5
  Length = 12
  Placement = pos=(-6,-25,71) rot=(0,0,1;0rad)
  Width = 13
FEATURE [Part::Cylinder] Cylinder014005773  label="Válec686"
  Angle = 360
  AttacherType = Attacher::AttachEngine3D
  Height = 8
  Placement = pos=(0,0,66) rot=(0,0,1;0rad)
  Radius = 4.5
FEATURE [Part::Extrusion] Extrude082
  Base = -> Sketch049
  Dir = (1,0,0)
  DirMode = 2
  FaceMakerClass = Part::FaceMakerBullseye
  LengthFwd = 5
  LengthRev = 0
  Placement = pos=(0,0,0.25) rot=(0,0,1;0rad)
  Solid = true
  Symmetric = false
FEATURE [Part::Extrusion] Extrude083
  Base = -> Sketch048
  Dir = (0,0,1)
  DirMode = 2
  FaceMakerClass = Part::FaceMakerBullseye
  LengthFwd = -112
  LengthRev = 0
  Solid = true
  Symmetric = false
FEATURE [Part::RegularPolygon] RegularPolygon009  label="Pravidelný n-úhelník009"
  AttacherType = Attacher::AttachEngine3D
  Circumradius = 6
  Polygon = 6
FEATURE [Part::Extrusion] Extrude081
  Base = -> RegularPolygon009
  Dir = (0,0,1)
  DirMode = 2
  FaceMakerClass = Part::FaceMakerBullseye
  LengthFwd = 8
  LengthRev = 0
  Placement = pos=(0,0,13) rot=(0,0,1;0rad)
  Solid = true
  Symmetric = false
FEATURE [Part::MultiFuse] Fusion001089041  label="Arca plate base017"
  Placement = pos=(0,-6.5,115.5) rot=(-1,0,0;1.5708rad)
  Shapes = -> [Extrude083,Cut061098109]
FEATURE [Part::Cut] Cut061098108  label="Arca sw 012"
  Base = -> Box189
  Tool = -> Fusion001089041
FEATURE [Part::Cut] Cut061098113
  Base = -> Cut061098108
  Tool = -> Box190
FEATURE [Part::MultiFuse] Fusion001089042
  Shapes = -> [Cylinder014005769,Cut061098113]
FEATURE [Part::MultiFuse] Fusion001089043
  Placement = pos=(0,0,1) rot=(0,0,1;0rad)
  Shapes = -> [Box191,Cylinder014005761]
FEATURE [Part::MultiFuse] Fusion001089045  label="srouby035"
  Placement = pos=(0,0,0.5) rot=(0,0,1;0rad)
  Shapes = -> [Screw_solid104,Screw_solid102,Screw_solid103]
FEATURE [Part::Cut] Cut061098111  label="unasec vrch022"
  Base = -> Cylinder014005770
  Tool = -> Fusion001089045
FEATURE [Part::FeaturePython] Nut031  label="M5-Nut002"  # Fasteners workbench fastener (typed FeaturePython)
  Placement = pos=(22,-17,69) rot=(0,1,0;1.5708rad)
  diameter = 7
  invert = false
  matchOuter = false
  offset = 0
  thread = false
  type = 1
FEATURE [Part::FeaturePython] Nut032  label="M5-Nut003"  # Fasteners workbench fastener (typed FeaturePython)
  Placement = pos=(22,17,69) rot=(0,1,0;1.5708rad)
  diameter = 7
  invert = false
  matchOuter = false
  offset = 0
  thread = false
  type = 1
FEATURE [Part::MultiFuse] Fusion001089047
  Shapes = -> [Cylinder014005766,Cylinder014005764,Nut032,Nut031]
FEATURE [Part::Feature] Cylinder014005774  label="Válec687"
  shape: bbox 5 x 5 x 7 mm, 3 faces (baked)
FEATURE [Part::Feature] Fusion001089049  label="Pojistka015"
  Placement = pos=(0,0,0) rot=(0,0,1;2.0944rad)
  shape: bbox 9.944 x 13.82 x 16.54 mm, 27 faces (baked)
FEATURE [Part::Feature] Fusion001089050  label="Pojistka016"
  Placement = pos=(0,0,0) rot=(0,0,-1;2.05949rad)
  shape: bbox 9.575 x 13.96 x 16.54 mm, 27 faces (baked)
FEATURE [Part::Feature] Cylinder014005775  label="Válec688"
  Placement = pos=(0,0,0) rot=(0,0,1;4.18879rad)
  shape: bbox 5 x 5 x 7 mm, 3 faces (baked)
FEATURE [Part::Feature] union001_solid008  label="union001 (Solid)008"
  Placement = pos=(15,-7,-4) rot=(-1,0,0;1.5708rad)
  shape: bbox 10 x 5.7 x 11.54 mm, 33 faces (baked)
FEATURE [Part::MultiFuse] Fusion001089048  label="Pojistka014"
  Placement = pos=(-11,0,61.5) rot=(0,0,1;0rad)
  Shapes = -> [Box193,union001_solid008,Cylinder014005771]
FEATURE [Part::Feature] Cylinder014005776  label="Válec689"
  Placement = pos=(0,0,0) rot=(0,0,1;2.0944rad)
  shape: bbox 5 x 5 x 7 mm, 3 faces (baked)
FEATURE [Part::MultiFuse] Fusion001089044
  Shapes = -> [Cylinder014005775,Cylinder014005774,Cylinder014005776]
FEATURE [Part::MultiFuse] Fusion001089040
  Placement = pos=(0,0,1) rot=(0,0,1;0rad)
  Shapes = -> [Fusion001089044,Cylinder014005762]
FEATURE [Part::Cut] Cut061098107  label="Unasec Vrch zaklad022"
  Base = -> Cut061098111
  Tool = -> Fusion001089040
FEATURE [Part::MultiFuse] Fusion001089051
  Shapes = -> [Cut061098107,Cylinder014005760,Extrude081]
FEATURE [Part::MultiFuse] Fusion001089052
  Shapes = -> [Fusion001089048,Fusion001089049,Fusion001089050]
FEATURE [Part::MultiFuse] Fusion001089053
  Shapes = -> [Cylinder014005765,Extrude082]
FEATURE [Part::Cut] Cut061098106  label="unasec top009"
  Base = -> Fusion001089051
  Placement = pos=(0,0,42) rot=(0,0,1;0rad)
  Tool = -> Fusion001089053
FEATURE [Part::MultiFuse] Fusion001089046
  Shapes = -> [Cylinder014005768,Cut061098106,Cylinder014005773]
FEATURE [Part::Cut] Cut061098112
  Base = -> Fusion001089042
  Tool = -> Fusion001089046
FEATURE [Part::Cut] Cut061098103
  Base = -> Cut061098112
  Tool = -> Fusion001089047
FEATURE [Part::MultiFuse] Fusion001089057
  Placement = pos=(0,0,1) rot=(0,0,1;3.14159rad)
  Shapes = -> [Box194,Cylinder014005763]
FEATURE [Part::MultiFuse] Fusion001089054
  Shapes = -> [Fusion001089043,Fusion001089057]
FEATURE [Part::Cut] Cut061098110  label="Swis Arca007"
  Base = -> Cut061098103
  Placement = pos=(0,0,-3) rot=(0,0,1;0rad)
  Tool = -> Fusion001089054
FEATURE [Part::MultiFuse] Fusion001089056
  Shapes = -> [Cut061098110,Cylinder014005767]
FEATURE [Part::Cut] Cut061098102
  Base = -> Fusion001089056
  Tool = -> Cylinder014005772
FEATURE [Part::MultiFuse] Fusion001089055
  Shapes = -> [Cut061098102,Box192]
FEATURE [Part::Cut] Cut061098105  label="RA Clamp002"
  Base = -> Fusion001089055
  Tool = -> Fusion001089052
FEATURE [Part::Cylinder] Cylinder014005777  label="Válec690"
  Angle = 360
  AttacherType = Attacher::AttachEngine3D
  Height = 11
  Placement = pos=(0,0,38) rot=(0,0,1;0rad)
  Radius = 11
FEATURE [Part::Cut] Cut061098104  label="DEC Clamp"
  Base = -> Cut061098105
  Tool = -> Cylinder014005777
FEATURE [Part::Part2DObjectPython] ShapeString014  # Draft 2D object (typed FeaturePython)
  FontFile = <path>
  Placement = pos=(15.3452,-2,30.5072) rot=(1,0,0;1.5708rad)
  Size = 4
  String = RA
  Tracking = 0
FEATURE [Part::Part2DObjectPython] ShapeString015  # Draft 2D object (typed FeaturePython)
  FontFile = <path>
  Placement = pos=(15.3452,-2,30.5072) rot=(1,0,0;1.5708rad)
  Size = 0.01
  String = .
  Tracking = 0
FEATURE [Part::Extrusion] Extrude084  label="Text RA001"
  Base = -> ShapeString014
  Dir = (0,-1,0)
  DirMode = 2
  FaceMakerClass = Part::FaceMakerBullseye
  LengthFwd = 1
  LengthRev = 0
  Placement = pos=(21,0.5,-33) rot=(0,0,1;0rad)
  Solid = false
  Symmetric = false
FEATURE [Part::Cylinder] Cylinder014005778  label="Válec691"
  Angle = 360
  AttacherType = Attacher::AttachEngine3D
  Height = 8
  Placement = pos=(3.5,6,0) rot=(0,0,1;0rad)
  Radius = 0.7
FEATURE [Part::Box] Box195  label="Krychle172"
  AttacherType = Attacher::AttachEngine3D
  Height = 26
  Length = 58
  Placement = pos=(-0.5,0,-3) rot=(0,0,1;0rad)
  Width = 29
FEATURE [Part::Cylinder] Cylinder014005779  label="Válec692"
  Angle = 360
  AttacherType = Attacher::AttachEngine3D
  Height = 8
  Placement = pos=(53.5,21.25,0) rot=(0,0,1;0rad)
  Radius = 0.75
FEATURE [Part::Cylinder] Cylinder014005780  label="Válec693"
  Angle = 360
  AttacherType = Attacher::AttachEngine3D
  Height = 6.5
  Placement = pos=(3.5,6,0) rot=(0,0,1;0rad)
  Radius = 3.5
FEATURE [Part::Cylinder] Cylinder014005781  label="Válec694"
  Angle = 360
  AttacherType = Attacher::AttachEngine3D
  Height = 6.5
  Placement = pos=(53.5,21.25,0) rot=(0,0,1;0rad)
  Radius = 3.5
FEATURE [Part::Cylinder] Cylinder014005782  label="Válec695"
  Angle = 360
  AttacherType = Attacher::AttachEngine3D
  Height = 8
  Placement = pos=(53.5,6,0) rot=(0,0,1;0rad)
  Radius = 0.75
FEATURE [Part::Cylinder] Cylinder014005783  label="Válec696"
  Angle = 360
  AttacherType = Attacher::AttachEngine3D
  Height = 70
  Placement = pos=(-5,20,16.5) rot=(0,1,0;1.5708rad)
  Radius = 1
FEATURE [Part::Cylinder] Cylinder014005784  label="Válec697"
  Angle = 360
  AttacherType = Attacher::AttachEngine3D
  Height = 70
  Placement = pos=(-5,6,16.5) rot=(0,1,0;1.5708rad)
  Radius = 1
FEATURE [Part::MultiFuse] Fusion001089059  label="Horni diry010"
  Placement = pos=(0,0,3) rot=(0,0,1;0rad)
  Shapes = -> [Cylinder014005783,Cylinder014005784]
FEATURE [Part::Box] Box196  label="RJ055"
  AttacherType = Attacher::AttachEngine3D
  Height = 13
  Length = 16
  Placement = pos=(32,-5,4.5) rot=(0,0,1;0rad)
  Width = 18.5
FEATURE [Part::Cylinder] Cylinder014005785  label="Válec698"
  Angle = 360
  AttacherType = Attacher::AttachEngine3D
  Height = 5
  Placement = pos=(14.25,1,9.5) rot=(1,0,0;1.5708rad)
  Radius = 0.01
FEATURE [Part::MultiFuse] Fusion001089058  label="RJ a LED001"
  Shapes = -> [Box196,Cylinder014005785]
FEATURE [Part::Cylinder] Cylinder014005786  label="Válec699"
  Angle = 360
  AttacherType = Attacher::AttachEngine3D
  Height = 8
  Placement = pos=(3.5,21.25,0) rot=(0,0,1;0rad)
  Radius = 0.75
FEATURE [Part::MultiFuse] Fusion001089060  label="diry016"
  Placement = pos=(0,0,-4) rot=(0,0,1;0rad)
  Shapes = -> [Cylinder014005786,Cylinder014005778,Cylinder014005779,Cylinder014005782]
FEATURE [Part::Cylinder] Cylinder014005787  label="Válec700"
  Angle = 360
  AttacherType = Attacher::AttachEngine3D
  Height = 6.5
  Placement = pos=(3.5,21.25,0) rot=(0,0,1;0rad)
  Radius = 3.5
FEATURE [Part::Box] Box197  label="Krychle173"
  AttacherType = Attacher::AttachEngine3D
  Height = 13
  Length = 2
  Placement = pos=(29,-4.5,-55) rot=(0,0,1;0rad)
  Width = 28
FEATURE [Part::Box] Box198  label="Krychle174"
  AttacherType = Attacher::AttachEngine3D
  Height = 13
  Length = 2
  Placement = pos=(-31,-4.5,-55) rot=(0,0,1;0rad)
  Width = 28
FEATURE [Part::Cylinder] Cylinder014005788  label="Válec701"
  Angle = 360
  AttacherType = Attacher::AttachEngine3D
  Height = 6.5
  Placement = pos=(53.5,6,0) rot=(0,0,1;0rad)
  Radius = 3.5
FEATURE [Part::MultiFuse] Fusion001089061  label="sloupky004"
  Placement = pos=(0,0,-3.5) rot=(0,0,1;0rad)
  Shapes = -> [Cylinder014005787,Cylinder014005780,Cylinder014005781,Cylinder014005788]
FEATURE [Part::Box] Box199  label="Krychle175"
  AttacherType = Attacher::AttachEngine3D
  Height = 28
  Length = 62
  Placement = pos=(-2.5,-2,-5) rot=(0,0,1;0rad)
  Width = 31
FEATURE [Part::Cut] Cut061098114  label="Základ001"
  Base = -> Box199
  Tool = -> Box195
FEATURE [Part::Extrusion] Extrude085  label="Text TR001"
  Base = -> ShapeString015
  Dir = (0,-1,0)
  DirMode = 2
  FaceMakerClass = Part::FaceMakerBullseye
  LengthFwd = 1
  LengthRev = 0
  Placement = pos=(-6.75,0.5,-33) rot=(0,0,1;0rad)
  Solid = false
  Symmetric = false
FEATURE [Part::MultiFuse] Fusion001089062
  Shapes = -> [Fusion001089060,Fusion001089058,Fusion001089059]
FEATURE [Part::MultiFuse] Fusion001089063
  Shapes = -> [Extrude085,Extrude084]
FEATURE [Part::MultiFuse] Fusion001089066
  Shapes = -> [Box197,Box198]
FEATURE [Part::MultiFuse] Fusion001089067  label="bez der001"
  Shapes = -> [Cut061098114,Fusion001089061]
FEATURE [Part::Cut] Cut061098117
  Base = -> Fusion001089067
  Tool = -> Fusion001089062
FEATURE [Part::Cut] Cut061098115
  Base = -> Cut061098117
  Placement = pos=(-28.5,18.5,-80) rot=(1,0,0;1.5708rad)
  Tool = -> Fusion001089063
FEATURE [Part::MultiFuse] Fusion001089065  label="RA pcb box001"
  Shapes = -> [Cut061098115,Fusion001089066]
FEATURE [Part::Cylinder] Cylinder014005789  label="Válec702"
  Angle = 360
  AttacherType = Attacher::AttachEngine3D
  Height = 74
  Placement = pos=(-40,19,-46.5) rot=(0,1,0;1.5708rad)
  Radius = 1.4
FEATURE [Part::Cylinder] Cylinder014005790  label="Válec703"
  Angle = 360
  AttacherType = Attacher::AttachEngine3D
  Height = 74
  Placement = pos=(-40,0,-46.5) rot=(0,1,0;1.5708rad)
  Radius = 1.4
FEATURE [Part::MultiFuse] Fusion001089064
  Shapes = -> [Cylinder014005790,Cylinder014005789]
FEATURE [Part::Cut] Cut061098116  label="RA PCB BOX For  MiniPCB2"
  Base = -> Fusion001089065
  Tool = -> Fusion001089064
FEATURE [App::Part] Part023  label="RA"
  Group = -> [Cut061098001,Cut061098046,Cut061098047,Fusion001051,Fusion001053,Fusion001054,Fusion001057,Fusion001052,Fusion001056,Chamfer,Chamfer008010,Box142,Cylinder014005674,Cylinder014005671,Box143,Cylinder014005675,Box144,Cylinder014005676,Cylinder014005677,Cylinder014005685,Cut061098052,Cut061098048,Fusion001055,Cut061098049,Chamfer008011,Cylinder,Cylinder014005684,Box145,Cylinder014005680,+168 more]
  License = CC BY 3.0
  LicenseURL = http://creativecommons.org/licenses/by/3.0/
  Origin = -> Origin023
  Placement = pos=(0,0,0) rot=(0,0,1;3.14159rad)
FEATURE [Part::Part2DObjectPython] ShapeString016  # Draft 2D object (typed FeaturePython)
  FontFile = <path>
  Placement = pos=(15.3452,-2,30.5072) rot=(1,0,0;1.5708rad)
  Size = 0.01
  String = .
  Tracking = 0
FEATURE [Part::Extrusion] Extrude087  label="Text TR002"
  Base = -> ShapeString016
  Dir = (0,-1,0)
  DirMode = 2
  FaceMakerClass = Part::FaceMakerBullseye
  LengthFwd = 1
  LengthRev = 0
  Placement = pos=(-6.75,0.5,-33) rot=(0,0,1;0rad)
  Solid = false
  Symmetric = false
FEATURE [Part::Part2DObjectPython] ShapeString017  # Draft 2D object (typed FeaturePython)
  FontFile = <path>
  Placement = pos=(15.3452,-2,30.5072) rot=(1,0,0;1.5708rad)
  Size = 4
  String = DEC
  Tracking = 0
FEATURE [Part::Extrusion] Extrude086  label="Text RA002"
  Base = -> ShapeString017
  Dir = (0,-1,0)
  DirMode = 2
  FaceMakerClass = Part::FaceMakerBullseye
  LengthFwd = 1
  LengthRev = 0
  Placement = pos=(18,0.5,-33) rot=(0,0,1;0rad)
  Solid = false
  Symmetric = false
FEATURE [Part::Cylinder] Cylinder014005791  label="Válec704"
  Angle = 360
  AttacherType = Attacher::AttachEngine3D
  Height = 70
  Placement = pos=(-5,6,16.5) rot=(0,1,0;1.5708rad)
  Radius = 1
FEATURE [Part::Box] Box200  label="Krychle176"
  AttacherType = Attacher::AttachEngine3D
  Height = 26
  Length = 58
  Placement = pos=(-0.5,0,-3) rot=(0,0,1;0rad)
  Width = 29
FEATURE [Part::Cylinder] Cylinder014005792  label="Válec705"
  Angle = 360
  AttacherType = Attacher::AttachEngine3D
  Height = 8
  Placement = pos=(53.5,21.25,0) rot=(0,0,1;0rad)
  Radius = 0.75
FEATURE [Part::Cylinder] Cylinder014005793  label="Válec706"
  Angle = 360
  AttacherType = Attacher::AttachEngine3D
  Height = 6.5
  Placement = pos=(3.5,21.25,0) rot=(0,0,1;0rad)
  Radius = 3.5
FEATURE [Part::Cylinder] Cylinder014005794  label="Válec707"
  Angle = 360
  AttacherType = Attacher::AttachEngine3D
  Height = 6.5
  Placement = pos=(3.5,6,0) rot=(0,0,1;0rad)
  Radius = 3.5
FEATURE [Part::Cylinder] Cylinder014005795  label="Válec708"
  Angle = 360
  AttacherType = Attacher::AttachEngine3D
  Height = 6.5
  Placement = pos=(53.5,6,0) rot=(0,0,1;0rad)
  Radius = 3.5
FEATURE [Part::Cylinder] Cylinder014005796  label="Válec709"
  Angle = 360
  AttacherType = Attacher::AttachEngine3D
  Height = 8
  Placement = pos=(53.5,6,0) rot=(0,0,1;0rad)
  Radius = 0.75
FEATURE [Part::Cylinder] Cylinder014005797  label="Válec710"
  Angle = 360
  AttacherType = Attacher::AttachEngine3D
  Height = 6.5
  Placement = pos=(53.5,21.25,0) rot=(0,0,1;0rad)
  Radius = 3.5
FEATURE [Part::MultiFuse] Fusion001089072  label="sloupky005"
  Placement = pos=(0,0,-3.5) rot=(0,0,1;0rad)
  Shapes = -> [Cylinder014005793,Cylinder014005794,Cylinder014005797,Cylinder014005795]
FEATURE [Part::Cylinder] Cylinder014005798  label="Válec711"
  Angle = 360
  AttacherType = Attacher::AttachEngine3D
  Height = 8
  Placement = pos=(3.5,6,0) rot=(0,0,1;0rad)
  Radius = 0.7
FEATURE [Part::Cylinder] Cylinder014005799  label="Válec712"
  Angle = 360
  AttacherType = Attacher::AttachEngine3D
  Height = 70
  Placement = pos=(-5,20,16.5) rot=(0,1,0;1.5708rad)
  Radius = 1
FEATURE [Part::MultiFuse] Fusion001089071  label="Horni diry011"
  Placement = pos=(0,0,3) rot=(0,0,1;0rad)
  Shapes = -> [Cylinder014005799,Cylinder014005791]
FEATURE [Part::Box] Box201  label="RJ056"
  AttacherType = Attacher::AttachEngine3D
  Height = 13
  Length = 16
  Placement = pos=(32,-5,4.5) rot=(0,0,1;0rad)
  Width = 18.5
FEATURE [Part::Cylinder] Cylinder014005800  label="Válec713"
  Angle = 360
  AttacherType = Attacher::AttachEngine3D
  Height = 8
  Placement = pos=(3.5,21.25,0) rot=(0,0,1;0rad)
  Radius = 0.75
FEATURE [Part::MultiFuse] Fusion001089068  label="diry017"
  Placement = pos=(0,0,-4) rot=(0,0,1;0rad)
  Shapes = -> [Cylinder014005800,Cylinder014005798,Cylinder014005792,Cylinder014005796]
FEATURE [Part::Box] Box202  label="Krychle177"
  AttacherType = Attacher::AttachEngine3D
  Height = 13
  Length = 2
  Placement = pos=(29,-4.5,-55) rot=(0,0,1;0rad)
  Width = 28
FEATURE [Part::Box] Box203  label="Krychle178"
  AttacherType = Attacher::AttachEngine3D
  Height = 13
  Length = 2
  Placement = pos=(-31,-4.5,-55) rot=(0,0,1;0rad)
  Width = 28
FEATURE [Part::Cylinder] Cylinder014005801  label="Válec714"
  Angle = 360
  AttacherType = Attacher::AttachEngine3D
  Height = 5
  Placement = pos=(14.25,1,9.5) rot=(1,0,0;1.5708rad)
  Radius = 0.01
FEATURE [Part::MultiFuse] Fusion001089070  label="RJ a LED002"
  Shapes = -> [Box201,Cylinder014005801]
FEATURE [Part::MultiFuse] Fusion001089069
  Shapes = -> [Fusion001089068,Fusion001089070,Fusion001089071]
FEATURE [Part::Cylinder] Cylinder014005802  label="Válec715"
  Angle = 360
  AttacherType = Attacher::AttachEngine3D
  Height = 74
  Placement = pos=(-40,19,-46.5) rot=(0,1,0;1.5708rad)
  Radius = 1.4
FEATURE [Part::Box] Box204  label="Krychle179"
  AttacherType = Attacher::AttachEngine3D
  Height = 28
  Length = 62
  Placement = pos=(-2.5,-2,-5) rot=(0,0,1;0rad)
  Width = 31
FEATURE [Part::Cut] Cut061098120  label="Základ002"
  Base = -> Box204
  Tool = -> Box200
FEATURE [Part::Cylinder] Cylinder014005803  label="Válec716"
  Angle = 360
  AttacherType = Attacher::AttachEngine3D
  Height = 74
  Placement = pos=(-40,0,-46.5) rot=(0,1,0;1.5708rad)
  Radius = 1.4
FEATURE [Part::MultiFuse] Fusion001089073
  Shapes = -> [Cylinder014005803,Cylinder014005802]
FEATURE [Part::MultiFuse] Fusion001089074  label="bez der002"
  Shapes = -> [Cut061098120,Fusion001089072]
FEATURE [Part::Cut] Cut061098121
  Base = -> Fusion001089074
  Tool = -> Fusion001089069
FEATURE [Part::MultiFuse] Fusion001089075
  Shapes = -> [Extrude087,Extrude086]
FEATURE [Part::Cut] Cut061098118
  Base = -> Cut061098121
  Placement = pos=(-28.5,18.5,-80) rot=(1,0,0;1.5708rad)
  Tool = -> Fusion001089075
FEATURE [Part::MultiFuse] Fusion001089077
  Shapes = -> [Box202,Box203]
FEATURE [Part::MultiFuse] Fusion001089076  label="RA pcb box002"
  Shapes = -> [Cut061098118,Fusion001089077]
FEATURE [Part::Cut] Cut061098119  label="DEC PCB BOX For MiniPCB2"
  Base = -> Fusion001089076
  Tool = -> Fusion001089073
FEATURE [App::Part] Part024  label="DEC"
  Group = -> [Cut061098023,Cut061098056,Cut061098057,Fusion001064,Chamfer008014,Box149,Cylinder014005693,Cylinder014005692,Cylinder014005695,Cylinder014005698,Cylinder014005696,Cylinder014005697,Cylinder014005694,Cut061098058,Fusion001063,Fusion001058,Fusion001059,Fusion001060,Fusion001061,Fusion001062,Cut061098054,Cut061098055,Chamfer008012,Chamfer008013,Box148,Cylinder014005691,Cylinder014005689,Box146,+163 more]
  License = CC BY 3.0
  LicenseURL = http://creativecommons.org/licenses/by/3.0/
  Origin = -> Origin024
  Placement = pos=(0,0,112) rot=(1,0,0;-1.5708rad)
FEATURE [Part::Feature] Chamfer008019  label="Zaklad009"
  shape: bbox 61 x 63.5 x 101.5 mm, 101 faces (baked)
FEATURE [Part::Cylinder] Cylinder014005804  label="Válec717"
  Angle = 360
  AttacherType = Attacher::AttachEngine3D
  Height = 52
  Placement = pos=(0,0,-6) rot=(0,0,1;0rad)
  Radius = 21.3
FEATURE [Part::Box] Box205  label="Krychle180"
  AttacherType = Attacher::AttachEngine3D
  Height = 56.5
  Length = 51
  Placement = pos=(-25.5,-22.5,-6) rot=(0,0,1;0rad)
  Width = 44
FEATURE [Part::Chamfer] Chamfer008018
  Base = -> Box205
  Edges = 2 edges r=7: [Edge1,Edge5]
FEATURE [Part::Cylinder] Cylinder014005805  label="Válec718"
  Angle = 360
  AttacherType = Attacher::AttachEngine3D
  Height = 40
  Placement = pos=(-40,1,-17.5) rot=(0,1,0;1.5708rad)
  Radius = 1.2
FEATURE [Part::Box] Box206  label="Krychle181"
  AttacherType = Attacher::AttachEngine3D
  Height = 13
  Length = 2
  Placement = pos=(29,-4.5,-55) rot=(0,0,1;0rad)
  Width = 28
FEATURE [Part::Cylinder] Cylinder014005806  label="Válec719"
  Angle = 360
  AttacherType = Attacher::AttachEngine3D
  Height = 74
  Placement = pos=(-40,19,-46.5) rot=(0,1,0;1.5708rad)
  Radius = 1.2
FEATURE [Part::Box] Box207  label="Krychle182"
  AttacherType = Attacher::AttachEngine3D
  Height = 13
  Length = 2
  Placement = pos=(-31,-4.5,-55) rot=(0,0,1;0rad)
  Width = 28
FEATURE [Part::Cylinder] Cylinder014005807  label="Válec720"
  Angle = 360
  AttacherType = Attacher::AttachEngine3D
  Height = 74
  Placement = pos=(-40,0,-46.5) rot=(0,1,0;1.5708rad)
  Radius = 1.2
FEATURE [Part::MultiFuse] Fusion001089082
  Shapes = -> [Cylinder014005807,Cylinder014005806]
FEATURE [Part::MultiFuse] Fusion001089083
  Shapes = -> [Box206,Box207]
FEATURE [Part::MultiFuse] Fusion001089078
  Shapes = -> [Fusion001089083,Fusion001089082]
FEATURE [Part::Cut] Cut061098124  label="Zaklad 004"
  Base = -> Chamfer008019
  Tool = -> Fusion001089078
FEATURE [Part::Cylinder] Cylinder014005808  label="Válec721"
  Angle = 360
  AttacherType = Attacher::AttachEngine3D
  Height = 40
  Placement = pos=(-40,16,-17.5) rot=(0,1,0;1.5708rad)
  Radius = 1.2
FEATURE [Part::MultiFuse] Fusion001089079
  Shapes = -> [Cylinder014005805,Cylinder014005808]
FEATURE [Part::Cut] Cut061098123  label="RA Zaklad004"
  Base = -> Cut061098124
  Tool = -> Fusion001089079
FEATURE [Part::MultiFuse] Fusion001089081
  Shapes = -> [Cut061098123,Chamfer008018]
FEATURE [Part::Cylinder] Cylinder014005809  label="Válec722"
  Angle = 360
  AttacherType = Attacher::AttachEngine3D
  Height = 8
  Placement = pos=(0,0,46) rot=(0,0,1;0rad)
  Radius = 13
FEATURE [Part::Cylinder] Cylinder014005810  label="Válec723"
  Angle = 360
  AttacherType = Attacher::AttachEngine3D
  Height = 10
  Placement = pos=(17.5,0,43) rot=(0,0,1;0rad)
  Radius = 2.15
FEATURE [Part::Cylinder] Cylinder014005811  label="Válec724"
  Angle = 360
  AttacherType = Attacher::AttachEngine3D
  Height = 10
  Placement = pos=(0,-17.5,43) rot=(0,0,1;0rad)
  Radius = 2.15
FEATURE [Part::Cylinder] Cylinder014005812  label="Válec725"
  Angle = 360
  AttacherType = Attacher::AttachEngine3D
  Height = 10
  Placement = pos=(-17.5,0,43) rot=(0,0,1;0rad)
  Radius = 2.15
FEATURE [Part::Cylinder] Cylinder014005813  label="Válec726"
  Angle = 360
  AttacherType = Attacher::AttachEngine3D
  Height = 10
  Placement = pos=(0,17.5,43) rot=(0,0,1;0rad)
  Radius = 2.15
FEATURE [Part::MultiFuse] Fusion001089080
  Shapes = -> [Cylinder014005809,Cylinder014005804,Cylinder014005810,Cylinder014005811,Cylinder014005812,Cylinder014005813]
FEATURE [Part::Cut] Cut061098122  label="RA Base001"
  Base = -> Fusion001089081
  Tool = -> Fusion001089080
FEATURE [Part::Feature] Cut061098122001  label="RA Base002"
  shape: bbox 61 x 65.5 x 101.5 mm, 101 faces (baked)
FEATURE [Part::Cylinder] Cylinder014005814  label="Válec727"
  Angle = 360
  AttacherType = Attacher::AttachEngine3D
  Height = 7
  Radius = 14
FEATURE [Part::Cylinder] Cylinder014005815  label="Válec728"
  Angle = 360
  AttacherType = Attacher::AttachEngine3D
  Height = 5
  Radius = 22
FEATURE [Part::Cylinder] Cylinder014005816  label="Válec729"
  Angle = 360
  AttacherType = Attacher::AttachEngine3D
  Height = 5
  Placement = pos=(0,0,16) rot=(0,0,1;0rad)
  Radius = 22
FEATURE [Part::Cylinder] Cylinder014005817  label="Válec730"
  Angle = 360
  AttacherType = Attacher::AttachEngine3D
  Height = 30
  Radius = 3.4
FEATURE [Part::Cylinder] Cylinder014005818  label="Válec731"
  Angle = 360
  AttacherType = Attacher::AttachEngine3D
  Height = 13
  Placement = pos=(0,0,8) rot=(0,0,1;0rad)
  Radius = 14
FEATURE [Part::Cylinder] Cylinder014005819  label="Válec732"
  Angle = 360
  AttacherType = Attacher::AttachEngine3D
  Height = 30
  Radius = 3.4
FEATURE [Part::MultiFuse] Fusion001089085
  Shapes = -> [Cylinder014005818,Cylinder014005816]
FEATURE [Part::Cut] Cut061098122002
  Base = -> Fusion001089085
  Tool = -> Cylinder014005819
FEATURE [Part::FeaturePython] Nut033  label="M6-Nut007"  # Fasteners workbench fastener (typed FeaturePython)
  Placement = pos=(0,0,12) rot=(0,0,1;0rad)
  diameter = 8
  invert = false
  matchOuter = false
  offset = 0
  thread = false
  type = 1
FEATURE [Part::Cylinder] Cylinder014005820  label="Válec733"
  Angle = 360
  AttacherType = Attacher::AttachEngine3D
  Height = 13
  Placement = pos=(0,0,1) rot=(0,0,1;0rad)
  Radius = 8
FEATURE [Part::MultiFuse] Fusion001089084
  Shapes = -> [Cylinder014005815,Cylinder014005814,Cylinder014005820]
FEATURE [Part::Cut] Cut061098122003
  Base = -> Fusion001089084
  Tool = -> Cylinder014005817
FEATURE [Part::Cylinder] Cylinder014005821  label="Válec734"
  Angle = 360
  AttacherType = Attacher::AttachEngine3D
  Height = 13
  Radius = 8
FEATURE [Part::MultiFuse] Fusion001089086
  Shapes = -> [Nut033,Cylinder014005821]
FEATURE [Part::Cut] Cut061098122004
  Base = -> Cut061098122002
  Tool = -> Fusion001089086
FEATURE [Part::Fillet] Fillet
  Base = -> Cut061098122004
  Edges = 1 edges r=4: [Edge14]
FEATURE [Part::Fillet] Fillet010
  Base = -> Cut061098122003
  Edges = 2 edges: [Edge3 r=4,Edge13 r=1.5]
FEATURE [App::Part] Part055  label="Metalweght"
  Group = -> [Cut061098122003,Cylinder014005817,Cylinder014005814,Cylinder014005815,Cylinder014005820,Fusion001089084,Fillet010,Nut033,Cut061098122002,Cut061098122004,Cylinder014005819,Cylinder014005821,Cylinder014005818,Cylinder014005816,Fusion001089086,Fusion001089085,Fillet]
  License = CC BY 3.0
  LicenseURL = http://creativecommons.org/licenses/by/3.0/
  Origin = -> Origin057
FEATURE [Part::Part2DObjectPython] ShapeString018  # Draft 2D object (typed FeaturePython)
  FontFile = <path>
  Placement = pos=(15.3452,-2,30.5072) rot=(1,0,0;1.5708rad)
  Size = 4
  String = DEC
  Tracking = 0
FEATURE [Part::Part2DObjectPython] ShapeString019  # Draft 2D object (typed FeaturePython)
  FontFile = <path>
  Placement = pos=(15.3452,-2,30.5072) rot=(1,0,0;1.5708rad)
  Size = 0.01
  String = .
  Tracking = 0
FEATURE [Part::Extrusion] Extrude088  label="Text TR003"
  Base = -> ShapeString019
  Dir = (0,-1,0)
  DirMode = 2
  FaceMakerClass = Part::FaceMakerBullseye
  LengthFwd = 1
  LengthRev = 0
  Placement = pos=(-6.75,0.5,-33) rot=(0,0,1;0rad)
  Solid = false
  Symmetric = false
FEATURE [Part::Extrusion] Extrude089  label="Text RA003"
  Base = -> ShapeString018
  Dir = (0,-1,0)
  DirMode = 2
  FaceMakerClass = Part::FaceMakerBullseye
  LengthFwd = 1
  LengthRev = 0
  Placement = pos=(18,0.5,-33) rot=(0,0,1;0rad)
  Solid = false
  Symmetric = false
FEATURE [Part::MultiFuse] Fusion001089092
  Shapes = -> [Extrude088,Extrude089]
FEATURE [Part::Cylinder] Cylinder014005822  label="Válec735"
  Angle = 360
  AttacherType = Attacher::AttachEngine3D
  Height = 6.5
  Placement = pos=(3.5,21.25,0) rot=(0,0,1;0rad)
  Radius = 3.5
FEATURE [Part::Cylinder] Cylinder014005823  label="Válec736"
  Angle = 360
  AttacherType = Attacher::AttachEngine3D
  Height = 6.5
  Placement = pos=(53.5,6,0) rot=(0,0,1;0rad)
  Radius = 3.5
FEATURE [Part::Cylinder] Cylinder014005824  label="Válec737"
  Angle = 360
  AttacherType = Attacher::AttachEngine3D
  Height = 70
  Placement = pos=(-5,20,16.5) rot=(0,1,0;1.5708rad)
  Radius = 1
FEATURE [Part::Cylinder] Cylinder014005825  label="Válec738"
  Angle = 360
  AttacherType = Attacher::AttachEngine3D
  Height = 6.5
  Placement = pos=(53.5,21.25,0) rot=(0,0,1;0rad)
  Radius = 3.5
FEATURE [Part::Cylinder] Cylinder014005826  label="Válec739"
  Angle = 360
  AttacherType = Attacher::AttachEngine3D
  Height = 8
  Placement = pos=(3.5,6,0) rot=(0,0,1;0rad)
  Radius = 0.7
FEATURE [Part::Cylinder] Cylinder014005827  label="Válec740"
  Angle = 360
  AttacherType = Attacher::AttachEngine3D
  Height = 8
  Placement = pos=(53.5,21.25,0) rot=(0,0,1;0rad)
  Radius = 0.75
FEATURE [Part::Cylinder] Cylinder014005828  label="Válec741"
  Angle = 360
  AttacherType = Attacher::AttachEngine3D
  Height = 8
  Placement = pos=(3.5,21.25,0) rot=(0,0,1;0rad)
  Radius = 0.75
FEATURE [Part::Cylinder] Cylinder014005829  label="Válec742"
  Angle = 360
  AttacherType = Attacher::AttachEngine3D
  Height = 8
  Placement = pos=(53.5,6,0) rot=(0,0,1;0rad)
  Radius = 0.75
FEATURE [Part::MultiFuse] Fusion001089094  label="diry018"
  Placement = pos=(0,0,-4) rot=(0,0,1;0rad)
  Shapes = -> [Cylinder014005828,Cylinder014005826,Cylinder014005827,Cylinder014005829]
FEATURE [Part::Box] Box208  label="RJ057"
  AttacherType = Attacher::AttachEngine3D
  Height = 13
  Length = 16
  Placement = pos=(32,-5,4.5) rot=(0,0,1;0rad)
  Width = 18.5
FEATURE [Part::Cylinder] Cylinder014005830  label="Válec743"
  Angle = 360
  AttacherType = Attacher::AttachEngine3D
  Height = 6.5
  Placement = pos=(3.5,6,0) rot=(0,0,1;0rad)
  Radius = 3.5
FEATURE [Part::MultiFuse] Fusion001089091  label="sloupky006"
  Placement = pos=(0,0,-3.5) rot=(0,0,1;0rad)
  Shapes = -> [Cylinder014005822,Cylinder014005830,Cylinder014005825,Cylinder014005823]
FEATURE [Part::Box] Box209  label="Krychle183"
  AttacherType = Attacher::AttachEngine3D
  Height = 13
  Length = 2
  Placement = pos=(-31,-4.5,-55) rot=(0,0,1;0rad)
  Width = 28
FEATURE [Part::Cylinder] Cylinder014005831  label="Válec744"
  Angle = 360
  AttacherType = Attacher::AttachEngine3D
  Height = 5
  Placement = pos=(14.25,1,9.5) rot=(1,0,0;1.5708rad)
  Radius = 0.01
FEATURE [Part::MultiFuse] Fusion001089089  label="RJ a LED003"
  Shapes = -> [Box208,Cylinder014005831]
FEATURE [Part::Box] Box210  label="Krychle184"
  AttacherType = Attacher::AttachEngine3D
  Height = 13
  Length = 2
  Placement = pos=(29,-4.5,-55) rot=(0,0,1;0rad)
  Width = 28
FEATURE [Part::MultiFuse] Fusion001089095
  Shapes = -> [Box210,Box209]
FEATURE [Part::Box] Box211  label="Krychle185"
  AttacherType = Attacher::AttachEngine3D
  Height = 26
  Length = 58
  Placement = pos=(-0.5,0,-3) rot=(0,0,1;0rad)
  Width = 29
FEATURE [Part::Cylinder] Cylinder014005832  label="Válec745"
  Angle = 360
  AttacherType = Attacher::AttachEngine3D
  Height = 74
  Placement = pos=(-40,19,-46.5) rot=(0,1,0;1.5708rad)
  Radius = 1.4
FEATURE [Part::Box] Box212  label="Krychle186"
  AttacherType = Attacher::AttachEngine3D
  Height = 28
  Length = 62
  Placement = pos=(-2.5,-2,-5) rot=(0,0,1;0rad)
  Width = 31
FEATURE [Part::Cut] Cut061098122005  label="Základ003"
  Base = -> Box212
  Tool = -> Box211
FEATURE [Part::MultiFuse] Fusion001089096  label="bez der003"
  Shapes = -> [Cut061098122005,Fusion001089091]
FEATURE [Part::Cylinder] Cylinder014005833  label="Válec746"
  Angle = 360
  AttacherType = Attacher::AttachEngine3D
  Height = 70
  Placement = pos=(-5,6,16.5) rot=(0,1,0;1.5708rad)
  Radius = 1
FEATURE [Part::MultiFuse] Fusion001089087  label="Horni diry012"
  Placement = pos=(0,0,3) rot=(0,0,1;0rad)
  Shapes = -> [Cylinder014005824,Cylinder014005833]
FEATURE [Part::MultiFuse] Fusion001089090
  Shapes = -> [Fusion001089094,Fusion001089089,Fusion001089087]
FEATURE [Part::Cut] Cut061098122008
  Base = -> Fusion001089096
  Tool = -> Fusion001089090
FEATURE [Part::Cut] Cut061098122006
  Base = -> Cut061098122008
  Placement = pos=(-28.5,18.5,-80) rot=(1,0,0;1.5708rad)
  Tool = -> Fusion001089092
FEATURE [Part::MultiFuse] Fusion001089093  label="RA pcb box003"
  Shapes = -> [Cut061098122006,Fusion001089095]
FEATURE [Part::Cylinder] Cylinder014005834  label="Válec747"
  Angle = 360
  AttacherType = Attacher::AttachEngine3D
  Height = 74
  Placement = pos=(-40,0,-46.5) rot=(0,1,0;1.5708rad)
  Radius = 1.4
FEATURE [Part::MultiFuse] Fusion001089088
  Shapes = -> [Cylinder014005834,Cylinder014005832]
FEATURE [Part::Cut] Cut061098122007  label="DEC PCB BOX For MiniPCB003"
  Base = -> Fusion001089093
  Tool = -> Fusion001089088
FEATURE [Part::Part2DObjectPython] ShapeString020  # Draft 2D object (typed FeaturePython)
  FontFile = <path>
  Placement = pos=(15.3452,-2,30.5072) rot=(1,0,0;1.5708rad)
  Size = 0.01
  String = .
  Tracking = 0
FEATURE [Part::Extrusion] Extrude091  label="Text TR004"
  Base = -> ShapeString020
  Dir = (0,-1,0)
  DirMode = 2
  FaceMakerClass = Part::FaceMakerBullseye
  LengthFwd = 1
  LengthRev = 0
  Placement = pos=(-6.75,0.5,-33) rot=(0,0,1;0rad)
  Solid = false
  Symmetric = false
FEATURE [Part::Part2DObjectPython] ShapeString021  # Draft 2D object (typed FeaturePython)
  FontFile = <path>
  Placement = pos=(15.3452,-2,30.5072) rot=(1,0,0;1.5708rad)
  Size = 4
  String = DEC
  Tracking = 0
FEATURE [Part::Extrusion] Extrude090  label="Text RA004"
  Base = -> ShapeString021
  Dir = (0,-1,0)
  DirMode = 2
  FaceMakerClass = Part::FaceMakerBullseye
  LengthFwd = 1
  LengthRev = 0
  Placement = pos=(18,0.5,-33) rot=(0,0,1;0rad)
  Solid = false
  Symmetric = false
FEATURE [Part::MultiFuse] Fusion001089097
  Shapes = -> [Extrude091,Extrude090]
FEATURE [Part::Cylinder] Cylinder014005835  label="Válec748"
  Angle = 360
  AttacherType = Attacher::AttachEngine3D
  Height = 6.5
  Placement = pos=(53.5,6,0) rot=(0,0,1;0rad)
  Radius = 3.5
FEATURE [Part::Cylinder] Cylinder014005836  label="Válec749"
  Angle = 360
  AttacherType = Attacher::AttachEngine3D
  Height = 8
  Placement = pos=(3.5,6,0) rot=(0,0,1;0rad)
  Radius = 0.7
FEATURE [Part::Cylinder] Cylinder014005837  label="Válec750"
  Angle = 360
  AttacherType = Attacher::AttachEngine3D
  Height = 6.5
  Placement = pos=(3.5,21.25,0) rot=(0,0,1;0rad)
  Radius = 3.5
FEATURE [Part::Cylinder] Cylinder014005839  label="Válec752"
  Angle = 360
  AttacherType = Attacher::AttachEngine3D
  Height = 6.5
  Placement = pos=(53.5,21.25,0) rot=(0,0,1;0rad)
  Radius = 3.5
FEATURE [Part::Cylinder] Cylinder014005840  label="Válec753"
  Angle = 360
  AttacherType = Attacher::AttachEngine3D
  Height = 6.5
  Placement = pos=(3.5,6,0) rot=(0,0,1;0rad)
  Radius = 3.5
FEATURE [Part::MultiFuse] Fusion001089101  label="sloupky007"
  Placement = pos=(0,0,-3.5) rot=(0,0,1;0rad)
  Shapes = -> [Cylinder014005837,Cylinder014005840,Cylinder014005839,Cylinder014005835]
FEATURE [Part::Cylinder] Cylinder014005841  label="Válec754"
  Angle = 360
  AttacherType = Attacher::AttachEngine3D
  Height = 8
  Placement = pos=(3.5,21.25,0) rot=(0,0,1;0rad)
  Radius = 0.75
FEATURE [Part::Box] Box213  label="Krychle187"
  AttacherType = Attacher::AttachEngine3D
  Height = 28
  Length = 62
  Placement = pos=(-2.5,-2,-5) rot=(0,0,1;0rad)
  Width = 31
FEATURE [Part::Cylinder] Cylinder014005842  label="Válec755"
  Angle = 360
  AttacherType = Attacher::AttachEngine3D
  Height = 8
  Placement = pos=(53.5,6,0) rot=(0,0,1;0rad)
  Radius = 0.75
FEATURE [Part::Cylinder] Cylinder014005843  label="Válec756"
  Angle = 360
  AttacherType = Attacher::AttachEngine3D
  Height = 8
  Placement = pos=(53.5,21.25,0) rot=(0,0,1;0rad)
  Radius = 0.75
FEATURE [Part::MultiFuse] Fusion001089103  label="diry019"
  Placement = pos=(0,0,-4) rot=(0,0,1;0rad)
  Shapes = -> [Cylinder014005841,Cylinder014005836,Cylinder014005843,Cylinder014005842]
FEATURE [Part::Box] Box214  label="RJ058"
  AttacherType = Attacher::AttachEngine3D
  Height = 13
  Length = 16
  Placement = pos=(32,-5,4.5) rot=(0,0,1;0rad)
  Width = 18.5
FEATURE [Part::Cylinder] Cylinder014005844  label="Válec757"
  Angle = 360
  AttacherType = Attacher::AttachEngine3D
  Height = 5
  Placement = pos=(14.25,1,9.5) rot=(1,0,0;1.5708rad)
  Radius = 0.01
FEATURE [Part::MultiFuse] Fusion001089099  label="RJ a LED004"
  Shapes = -> [Box214,Cylinder014005844]
FEATURE [Part::MultiFuse] Fusion001089100
  Shapes = -> [Fusion001089103,Fusion001089099]
FEATURE [Part::Box] Box215  label="Krychle188"
  AttacherType = Attacher::AttachEngine3D
  Height = 26
  Length = 58
  Placement = pos=(-0.5,0,-3) rot=(0,0,1;0rad)
  Width = 29
FEATURE [Part::Cut] Cut061098122010  label="Základ004"
  Base = -> Box213
  Tool = -> Box215
FEATURE [Part::MultiFuse] Fusion001089098  label="bez der004"
  Shapes = -> [Cut061098122010,Fusion001089101]
FEATURE [Part::Cut] Cut061098122009
  Base = -> Fusion001089098
  Tool = -> Fusion001089100
FEATURE [Part::Cut] Cut061098122011
  Base = -> Cut061098122009
  Placement = pos=(-28.5,18.5,-80) rot=(1,0,0;3.14159rad)
  Tool = -> Fusion001089097
FEATURE [Part::Feature] Cut061098122011001  label="Cut061098122012"
  Placement = pos=(0,3,-157) rot=(0,1,0;3.14159rad)
  shape: bbox 62 x 31 x 28 mm, 92 faces (baked)
FEATURE [Part::Box] Box216  label="Krychle189"
  AttacherType = Attacher::AttachEngine3D
  Height = 29
  Length = 58
  Placement = pos=(-29,0,-80) rot=(0,0,1;0rad)
  Width = 24
FEATURE [App::Part] Part056
  Group = -> [Fusion001089097,Cut061098122010,Cut061098122009,ShapeString021,ShapeString020,Fusion001089100,Fusion001089101,Fusion001089103,Fusion001089099,Fusion001089098,Extrude091,Extrude090,Cylinder014005844,Cylinder014005837,Cylinder014005839,Box213,Cylinder014005842,Box214,Cylinder014005835,Cylinder014005840,Cylinder014005836,Cylinder014005841,Cylinder014005843,Box215,Cut061098122011]
  License = CC BY 3.0
  LicenseURL = http://creativecommons.org/licenses/by/3.0/
  Origin = -> Origin058
FEATURE [Part::Cut] Cut061098122011002
  Base = -> Cut061098122007
  Tool = -> Box216
FEATURE [Part::MultiFuse] Fusion001089104
  Shapes = -> [Cut061098122011001,Cut061098122011002]
FEATURE [Part::Box] Box217  label="Krychle190"
  AttacherType = Attacher::AttachEngine3D
  Height = 31
  Length = 2
  Placement = pos=(-31,-13.5,-82) rot=(0,0,1;0rad)
  Width = 37
FEATURE [Part::Box] Box218  label="Krychle191"
  AttacherType = Attacher::AttachEngine3D
  Height = 31
  Length = 2
  Placement = pos=(29,-13.5,-82) rot=(0,0,1;0rad)
  Width = 37
FEATURE [Part::Box] Box219  label="Krychle192"
  AttacherType = Attacher::AttachEngine3D
  Height = 7
  Length = 62
  Placement = pos=(-31,21.5,-58) rot=(0,0,1;0rad)
  Width = 2
FEATURE [Part::Part2DObjectPython] ShapeString022  # Draft 2D object (typed FeaturePython)
  FontFile = <path>
  Placement = pos=(15.3452,-2,30.5072) rot=(1,0,0;1.5708rad)
  Size = 10
  String = OnStep
  Tracking = 0
FEATURE [Part::Extrusion] Extrude092  label="OnStep006"
  Base = -> ShapeString022
  Dir = (0,-1,0)
  DirMode = 2
  FaceMakerClass = Part::FaceMakerBullseye
  LengthFwd = 1
  LengthRev = 0
  Placement = pos=(-10,-22,22) rot=(-1,0,0;1.5708rad)
  Solid = false
  Symmetric = false
FEATURE [Part::Cylinder] Cylinder014005845  label="Válec758"
  Angle = 360
  AttacherType = Attacher::AttachEngine3D
  Height = 70
  Placement = pos=(-5,20,16.5) rot=(0,1,0;1.5708rad)
  Radius = 1
FEATURE [Part::Box] Box220  label="Krychle193"
  AttacherType = Attacher::AttachEngine3D
  Height = 2
  Length = 62
  Placement = pos=(-2.5,-2,23) rot=(0,0,1;0rad)
  Width = 31
FEATURE [Part::Box] Box221  label="Krychle194"
  AttacherType = Attacher::AttachEngine3D
  Height = 4
  Length = 10
  Placement = pos=(-5,-8,-55) rot=(0,0,1;0rad)
  Width = 5
FEATURE [Part::Box] Box222  label="Krychle195"
  AttacherType = Attacher::AttachEngine3D
  Height = 8
  Length = 54
  Placement = pos=(1.5,0,15) rot=(0,0,1;0rad)
  Width = 29
FEATURE [Part::Cylinder] Cylinder014005846  label="Válec759"
  Angle = 360
  AttacherType = Attacher::AttachEngine3D
  Height = 70
  Placement = pos=(-5,6,16.5) rot=(0,1,0;1.5708rad)
  Radius = 1
FEATURE [Part::Box] Box223  label="Krychle196"
  AttacherType = Attacher::AttachEngine3D
  Height = 8
  Length = 58
  Placement = pos=(-0.5,0,15) rot=(0,0,1;0rad)
  Width = 29
FEATURE [Part::MultiFuse] Fusion001089105002
  Shapes = -> [Box220,Box223]
FEATURE [Part::MultiFuse] Fusion001089105004  label="Horni diry013"
  Placement = pos=(0,0,3) rot=(0,0,1;0rad)
  Shapes = -> [Cylinder014005845,Cylinder014005846]
FEATURE [Part::MultiFuse] Fusion001089105003
  Shapes = -> [Fusion001089105004,Box222]
FEATURE [Part::Cut] Cut061098122011005
  Base = -> Fusion001089105002
  Tool = -> Fusion001089105003
FEATURE [Part::Cut] Cut061098122011003  label="viko s texty006"
  Base = -> Cut061098122011005
  Tool = -> Extrude092
FEATURE [Part::Chamfer] Chamfer008020
  Base = -> Cut061098122011003
  Edges = 2 edges r=2.5: [Edge355,Edge357]
FEATURE [Part::Fillet] Fillet011  label="DEC vicko004"
  Base = -> Chamfer008020
  Edges = 3 edges r=1: [Edge36,Edge38,Edge39]
  Placement = pos=(-28.5,19,-80) rot=(1,0,0;1.5708rad)
FEATURE [Part::Cut] Cut061098122011004  label="DEC PCB Cap001"
  Base = -> Fillet011
  Placement = pos=(0,-11.5,0) rot=(0,0,1;0rad)
  Tool = -> Box221
FEATURE [Part::Box] Box224  label="Krychle197"
  AttacherType = Attacher::AttachEngine3D
  Height = 2
  Length = 62
  Placement = pos=(-31,-13.5,-82) rot=(0,0,1;0rad)
  Width = 7
FEATURE [Part::MultiFuse] Fusion001089105
  Shapes = -> [Box219,Fusion001089104,Box217,Box218,Box224]
FEATURE [Part::Cylinder] Cylinder014005847  label="Válec760"
  Angle = 360
  AttacherType = Attacher::AttachEngine3D
  Height = 70
  Placement = pos=(-5,20,16.5) rot=(0,1,0;1.5708rad)
  Radius = 0.7
FEATURE [Part::Cylinder] Cylinder014005848  label="Válec761"
  Angle = 360
  AttacherType = Attacher::AttachEngine3D
  Height = 70
  Placement = pos=(-5,6,16.5) rot=(0,1,0;1.5708rad)
  Radius = 0.7
FEATURE [Part::MultiFuse] Fusion001089105006  label="Horni diry014"
  Placement = pos=(-30,6.5,-80) rot=(1,0,0;1.5708rad)
  Shapes = -> [Cylinder014005847,Cylinder014005848]
FEATURE [Part::Cut] Cut061098122011006
  Base = -> Fusion001089105
  Tool = -> Fusion001089105006
FEATURE [Part::Feature] Cut061098122011006001  label="DECV2"
  shape: bbox 62 x 37 x 40 mm, 106 faces (baked)
FEATURE [Part::Feature] Cut061098122011006002  label="polar finder001"
  Placement = pos=(-9.5,-26.5,-25) rot=(0,0,-1;1.5708rad)
  shape: bbox 15 x 36 x 40 mm, 20 faces (baked)
FEATURE [Part::Cylinder] Cylinder014005849  label="Válec762"
  Angle = 360
  AttacherType = Attacher::AttachEngine3D
  Height = 20
  Placement = pos=(-40,16,-17.5) rot=(0,1,0;1.5708rad)
  Radius = 1.4
FEATURE [Part::Cylinder] Cylinder014005850  label="Válec763"
  Angle = 360
  AttacherType = Attacher::AttachEngine3D
  Height = 20
  Placement = pos=(-40,1,-17.5) rot=(0,1,0;1.5708rad)
  Radius = 1.4
FEATURE [Part::Cylinder] Cylinder014005851  label="Válec764"
  Angle = 360
  AttacherType = Attacher::AttachEngine3D
  Height = 7
  Placement = pos=(-40,16,-17.5) rot=(0,1,0;1.5708rad)
  Radius = 2.4
FEATURE [Part::Cylinder] Cylinder014005852  label="Válec765"
  Angle = 360
  AttacherType = Attacher::AttachEngine3D
  Height = 7
  Placement = pos=(-40,1,-17.5) rot=(0,1,0;1.5708rad)
  Radius = 2.4
FEATURE [Part::MultiFuse] Fusion001089105007
  Shapes = -> [Cylinder014005852,Cylinder014005851,Cylinder014005849,Cylinder014005850]
FEATURE [Part::Cut] Cut061098122011006003  label="RA Polar Finder Clamp001"
  Base = -> Cut061098122011006002
  Tool = -> Fusion001089105007
FEATURE [Part::Box] Box225  label="Krychle198"
  AttacherType = Attacher::AttachEngine3D
  Height = 112
  Length = 38
  Placement = pos=(-19,32,-52) rot=(0,0,1;0rad)
  Width = 10
FEATURE [Part::Box] Box226  label="Krychle199"
  AttacherType = Attacher::AttachEngine3D
  Height = 112
  Length = 38
  Placement = pos=(-19,34,-52) rot=(0,0,1;0rad)
  Width = 6
FEATURE [Part::Cut] Cut061098122011006004
  Base = -> Box225
  Tool = -> Box226
FEATURE [Sketcher::SketchObject] Sketch050
  MapMode = 5
  Placement = pos=(0,0,60) rot=(0,0,1;0rad)
  sketch-geometry (6):
    g0: LineSegment StartX=-18.9734 StartY=34.0308 StartZ=0 EndX=-16.0253 EndY=36.9748 EndZ=0
    g1: LineSegment StartX=18.996 StartY=34.0308 StartZ=0 EndX=16.044 EndY=36.9748 EndZ=0
    g2: LineSegment StartX=18.996 StartY=34.0308 StartZ=0 EndX=-18.9734 EndY=34.0308 EndZ=0
    g3: LineSegment StartX=-18.9734 StartY=40.0311 StartZ=0 EndX=-16.0253 EndY=36.9748 EndZ=0
    g4: LineSegment StartX=16.044 StartY=36.9748 StartZ=0 EndX=18.9109 EndY=40.0311 EndZ=0
    g5: LineSegment StartX=-18.9734 StartY=40.0311 StartZ=0 EndX=18.9109 EndY=40.0311 EndZ=0
  constraints (7):
    c: Coincident(g2,g1)
    c: Coincident(g2,g0)
    c: Horizontal(g2)
    c: Coincident(g3,g0)
    c: Coincident(g5,g3)
    c: Coincident(g5,g4)
    c: Horizontal(g5)
FEATURE [Part::Extrusion] Extrude093
  Base = -> Sketch050
  Dir = (0,0,1)
  DirMode = 2
  FaceMakerClass = Part::FaceMakerBullseye
  LengthFwd = -112
  LengthRev = 0
  Solid = true
  Symmetric = false
FEATURE [Part::Box] Box227  label="Krychle200"
  AttacherType = Attacher::AttachEngine3D
  Height = 40
  Length = 13
  Placement = pos=(-43,-14,-37) rot=(0,0,1;0rad)
  Width = 45
FEATURE [Part::MultiFuse] Fusion001089105008  label="Arca plate base018"
  Placement = pos=(-3,8.5,0) rot=(0,0,1;1.5708rad)
  Shapes = -> [Extrude093,Cut061098122011006004]
FEATURE [Part::Cut] Cut061098122011006005
  Base = -> Box227
  Tool = -> Fusion001089105008
FEATURE [Part::Box] Box228  label="Krychle201"
  AttacherType = Attacher::AttachEngine3D
  Height = 40
  Length = 2.5
  Placement = pos=(-35,4,-37) rot=(0,0,1;0rad)
  Width = 9
FEATURE [Part::Cut] Cut061098122011006006
  Base = -> Cut061098122011006005
  Tool = -> Box228
FEATURE [Part::Cylinder] Cylinder014005853  label="Válec766"
  Angle = 360
  AttacherType = Attacher::AttachEngine3D
  Height = 20
  Placement = pos=(-40,1,-17.5) rot=(0,1,0;1.5708rad)
  Radius = 1.4
FEATURE [Part::Cylinder] Cylinder014005854  label="Válec767"
  Angle = 360
  AttacherType = Attacher::AttachEngine3D
  Height = 20
  Placement = pos=(-40,16,-17.5) rot=(0,1,0;1.5708rad)
  Radius = 1.4
FEATURE [Part::Cylinder] Cylinder014005855  label="Válec768"
  Angle = 360
  AttacherType = Attacher::AttachEngine3D
  Height = 7
  Placement = pos=(-40,16,-17.5) rot=(0,1,0;1.5708rad)
  Radius = 2.4
FEATURE [Part::Cylinder] Cylinder014005856  label="Válec769"
  Angle = 360
  AttacherType = Attacher::AttachEngine3D
  Height = 7
  Placement = pos=(-40,1,-17.5) rot=(0,1,0;1.5708rad)
  Radius = 2.4
FEATURE [Part::Box] Box229  label="Krychle202"
  AttacherType = Attacher::AttachEngine3D
  Height = 40
  Length = 3.5
  Placement = pos=(-38.5,-11,-37) rot=(0,0,1;0rad)
  Width = 39
FEATURE [Part::Cylinder] Cylinder014005857  label="Válec770"
  Angle = 360
  AttacherType = Attacher::AttachEngine3D
  Height = 45
  Placement = pos=(-40,31,-18) rot=(1,0,0;1.5708rad)
  Radius = 1.2
FEATURE [Part::Box] Box230  label="Krychle203"
  AttacherType = Attacher::AttachEngine3D
  Height = 40
  Length = 3
  Placement = pos=(-42,-8,-37) rot=(0,0,1;0rad)
  Width = 33
FEATURE [Part::Box] Box231  label="Krychle204"
  AttacherType = Attacher::AttachEngine3D
  Height = 40
  Length = 3
  Placement = pos=(-46,-13,-37) rot=(0,0,1;0rad)
  Width = 43
FEATURE [Part::MultiFuse] Fusion001089105009
  Shapes = -> [Cylinder014005856,Cylinder014005855,Cylinder014005854,Cylinder014005853,Box229,Cylinder014005857,Box231,Box230]
FEATURE [Part::Cut] Cut061098122011006007  label="For polar"
  Base = -> Cut061098122011006006
  Tool = -> Fusion001089105009
FEATURE [App::Part] Part057  label="Work"
  Group = -> [Fusion001089105008,Fusion001089105009,Cut061098122011006004,Cut061098122011006005,Cut061098122011006006,Extrude093,Cylinder014005853,Box231,Cylinder014005854,Box225,Box229,Box226,Cylinder014005856,Box230,Box228,Box227,Cylinder014005855,Cylinder014005857,Sketch050,Cut061098122011006007,Fusion001089105007,Cut061098122011006002,Cylinder014005849,Cylinder014005850,Cylinder014005851,Cylinder014005852,+67 more]
  License = CC BY 3.0
  LicenseURL = http://creativecommons.org/licenses/by/3.0/
  Origin = -> Origin059
FEATURE [Part::Cylinder] Cylinder112024025003003006010005  label="Válec187"
  Angle = 360
  AttacherType = Attacher::AttachEngine3D
  Height = 10
  Placement = pos=(-19,0,18.5) rot=(0,1,0;1.5708rad)
  Radius = 3.7
FEATURE [Part::Cylinder] Cylinder112024025003003006010007  label="Válec189"
  Angle = 360
  AttacherType = Attacher::AttachEngine3D
  Height = 27
  Placement = pos=(0,0,-3.5) rot=(0,0,1;0rad)
  Radius = 7.2
FEATURE [Part::Cylinder] Cylinder112024025003003006010008  label="Válec190"
  Angle = 360
  AttacherType = Attacher::AttachEngine3D
  Height = 25
  Placement = pos=(0,-7.5,5.5) rot=(0,0,1;0rad)
  Radius = 2.5
FEATURE [Part::Cylinder] Cylinder112024025003003006010003  label="Válec185"
  Angle = 360
  AttacherType = Attacher::AttachEngine3D
  Height = 10
  Placement = pos=(9,0,18.5) rot=(0,1,0;1.5708rad)
  Radius = 3.7
FEATURE [Part::Cylinder] Cylinder112024025003003006010006  label="Válec188"
  Angle = 360
  AttacherType = Attacher::AttachEngine3D
  Height = 40
  Placement = pos=(0,0,-5) rot=(0,0,1;0rad)
  Radius = 3.55
FEATURE [Part::Cylinder] Cylinder112024025003003006010004  label="Válec186"
  Angle = 360
  AttacherType = Attacher::AttachEngine3D
  Height = 40
  Placement = pos=(-20,0,18.5) rot=(0,1,0;1.5708rad)
  Radius = 2.15
FEATURE [Part::Cylinder] Cylinder112024025003003006010009  label="Válec771"
  Angle = 360
  AttacherType = Attacher::AttachEngine3D
  Height = 28
  Placement = pos=(0,0,-16) rot=(0,0,1;0rad)
  Radius = 20
FEATURE [Part::Cylinder] Cylinder112024025003003006010010  label="Válec191"
  Angle = 360
  AttacherType = Attacher::AttachEngine3D
  Height = 25
  Placement = pos=(0,7.5,5.5) rot=(0,0,1;0rad)
  Radius = 2.5
FEATURE [Part::Feature] Part__Feature003  label="Spojka"
  Placement = pos=(-39,22,-6) rot=(0,0,1;0rad)
  shape: bbox 24 x 24 x 36.5 mm, 15 faces (baked)
FEATURE [Part::MultiFuse] Fusion001089105010
  Shapes = -> [Cylinder112024025003003006010008,Cylinder112024025003003006010010,Part__Feature003]
FEATURE [Part::MultiFuse] Fusion005043005007
  Placement = pos=(0,0,4.5) rot=(0,0,1;0rad)
  Shapes = -> [Cylinder112024025003003006010005,Cylinder112024025003003006010003,Cylinder112024025003003006010006,Cylinder112024025003003006010004,Cylinder112024025003003006010007,Cylinder112024025003003006010009]
FEATURE [Part::Cut] Cut061098122011006008  label="Kluc"
  Base = -> Fusion001089105010
  Tool = -> Fusion005043005007
FEATURE [App::Part] Part054  label="V2019 B"
  Group = -> [Cut061098122001,Chamfer008019,Fusion001089078,Fusion001089082,Fusion001089083,Fusion001089079,Fusion001089080,Fusion001089081,Cylinder014005806,Cylinder014005811,Box207,Cylinder014005805,Cylinder014005804,Box206,Cylinder014005807,Cylinder014005808,Box205,Cylinder014005809,Cylinder014005810,Cylinder014005812,Cylinder014005813,Cut061098123,Cut061098124,Chamfer008018,Cut061098122,Part__Feature003,+11 more]
  License = CC BY 3.0
  LicenseURL = http://creativecommons.org/licenses/by/3.0/
  Origin = -> Origin056
FEATURE [Sketcher::SketchObject] Sketch051
  MapMode = 5
  Placement = pos=(0,0,60) rot=(0,0,1;0rad)
  sketch-geometry (6):
    g0: LineSegment StartX=-18.9734 StartY=34.0308 StartZ=0 EndX=-16.0253 EndY=36.9748 EndZ=0
    g1: LineSegment StartX=18.996 StartY=34.0308 StartZ=0 EndX=16.044 EndY=36.9748 EndZ=0
    g2: LineSegment StartX=18.996 StartY=34.0308 StartZ=0 EndX=-18.9734 EndY=34.0308 EndZ=0
    g3: LineSegment StartX=-18.9734 StartY=40.0311 StartZ=0 EndX=-16.0253 EndY=36.9748 EndZ=0
    g4: LineSegment StartX=16.044 StartY=36.9748 StartZ=0 EndX=18.9109 EndY=40.0311 EndZ=0
    g5: LineSegment StartX=-18.9734 StartY=40.0311 StartZ=0 EndX=18.9109 EndY=40.0311 EndZ=0
  constraints (7):
    c: Coincident(g2,g1)
    c: Coincident(g2,g0)
    c: Horizontal(g2)
    c: Coincident(g3,g0)
    c: Coincident(g5,g3)
    c: Coincident(g5,g4)
    c: Horizontal(g5)
FEATURE [Part::Extrusion] Extrude094
  Base = -> Sketch051
  Dir = (0,0,1)
  DirMode = 2
  FaceMakerClass = Part::FaceMakerBullseye
  LengthFwd = -112
  LengthRev = 0
  Solid = true
  Symmetric = false
FEATURE [Part::Box] Box232  label="Krychle205"
  AttacherType = Attacher::AttachEngine3D
  Height = 55
  Length = 3
  Placement = pos=(-42,-8,-37) rot=(0,0,1;0rad)
  Width = 33
FEATURE [Part::Box] Box233  label="Krychle206"
  AttacherType = Attacher::AttachEngine3D
  Height = 55
  Length = 3
  Placement = pos=(-46,-13,-37) rot=(0,0,1;0rad)
  Width = 43
FEATURE [Part::Box] Box234  label="Krychle207"
  AttacherType = Attacher::AttachEngine3D
  Height = 112
  Length = 38
  Placement = pos=(-19,34,-52) rot=(0,0,1;0rad)
  Width = 6
FEATURE [Part::Box] Box235  label="Krychle208"
  AttacherType = Attacher::AttachEngine3D
  Height = 55
  Length = 2.5
  Placement = pos=(-35,4,-37) rot=(0,0,1;0rad)
  Width = 9
FEATURE [Part::Box] Box236  label="Krychle209"
  AttacherType = Attacher::AttachEngine3D
  Height = 55
  Length = 3.5
  Placement = pos=(-38.5,-11,-37) rot=(0,0,1;0rad)
  Width = 39
FEATURE [Part::Box] Box237  label="Krychle210"
  AttacherType = Attacher::AttachEngine3D
  Height = 112
  Length = 38
  Placement = pos=(-19,32,-52) rot=(0,0,1;0rad)
  Width = 10
FEATURE [Part::Cut] Cut061098122011006011
  Base = -> Box237
  Tool = -> Box234
FEATURE [Part::Box] Box238  label="Krychle211"
  AttacherType = Attacher::AttachEngine3D
  Height = 55
  Length = 13
  Placement = pos=(-43,-14,-37) rot=(0,0,1;0rad)
  Width = 45
FEATURE [Part::Cylinder] Cylinder112024025003003006010015  label="Válec776"
  Angle = 360
  AttacherType = Attacher::AttachEngine3D
  Height = 45
  Placement = pos=(-40,31,-30) rot=(1,0,0;1.5708rad)
  Radius = 1.2
FEATURE [Part::MultiFuse] Fusion005043005009  label="Arca plate base019"
  Placement = pos=(-3,8.5,0) rot=(0,0,1;1.5708rad)
  Shapes = -> [Extrude094,Cut061098122011006011]
FEATURE [Part::Cut] Cut061098122011006012
  Base = -> Box238
  Tool = -> Fusion005043005009
FEATURE [Part::Cut] Cut061098122011006009
  Base = -> Cut061098122011006012
  Tool = -> Box235
FEATURE [Part::Wedge] Wedge003  label="Klín003"
  AttacherType = Attacher::AttachEngine3D
  Placement = pos=(0,18,-37) rot=(0,0,1;0rad)
  X2max = 19
  X2min = -19
  Xmax = 21.5
  Xmin = -21.5
  Ymax = 12
  Ymin = 0
  Z2max = 55
  Z2min = 0
  Zmax = 55
  Zmin = 0
FEATURE [Part::Box] Box239  label="Krychle212"
  AttacherType = Attacher::AttachEngine3D
  Height = 55
  Length = 38
  Placement = pos=(-19,30,-37) rot=(0,0,1;0rad)
  Width = 4
FEATURE [Part::Cylinder] Cylinder112024025003003006010016  label="Válec777"
  Angle = 360
  AttacherType = Attacher::AttachEngine3D
  Height = 45
  Placement = pos=(-40,31,11) rot=(1,0,0;1.5708rad)
  Radius = 1.2
FEATURE [Part::MultiFuse] Fusion005043005008
  Shapes = -> [Box236,Cylinder112024025003003006010015,Box233,Box232,Cylinder112024025003003006010016]
FEATURE [Part::Cut] Cut061098122011006010  label="For polar001"
  Base = -> Cut061098122011006009
  Placement = pos=(-8.5,2,0) rot=(0,0,1;-1.5708rad)
  Tool = -> Fusion005043005008
FEATURE [Part::MultiFuse] Fusion005043005010  label="for skw"
  Shapes = -> [Wedge003,Cut061098122011006010,Box239]
FEATURE [Part::Box] Box240  label="Krychle213"
  AttacherType = Attacher::AttachEngine3D
  Height = 6
  Length = 20
  Placement = pos=(-10,-10,0) rot=(0,0,1;0rad)
  Width = 15
FEATURE [Part::Cylinder] Cylinder112024025003003006010017  label="Válec778"
  Angle = 360
  AttacherType = Attacher::AttachEngine3D
  Height = 10
  Radius = 2.7
FEATURE [Part::Cone] Cone  label="Kužel"
  Angle = 360
  AttacherType = Attacher::AttachEngine3D
  Height = 10
  Radius1 = 2
  Radius2 = 4
FEATURE [Part::Cylinder] Cylinder112024025003003006010018  label="Válec779"
  Angle = 360
  AttacherType = Attacher::AttachEngine3D
  Height = 10
  Radius = 2.7
FEATURE [Part::Cut] Cut061098122011006013
  Base = -> Cone
  Tool = -> Cylinder112024025003003006010018
FEATURE [Part::MultiFuse] Fusion005043005011
  Placement = pos=(0,0,3) rot=(0,0,1;0rad)
  Shapes = -> [Cylinder112024025003003006010017,Cut061098122011006013]
FEATURE [Part::Cut] Cut061098122011006014
  Base = -> Box240
  Tool = -> Fusion005043005011
note: 15 file-system paths scrubbed to <path> (originals preserved in the JSON sidecar)
